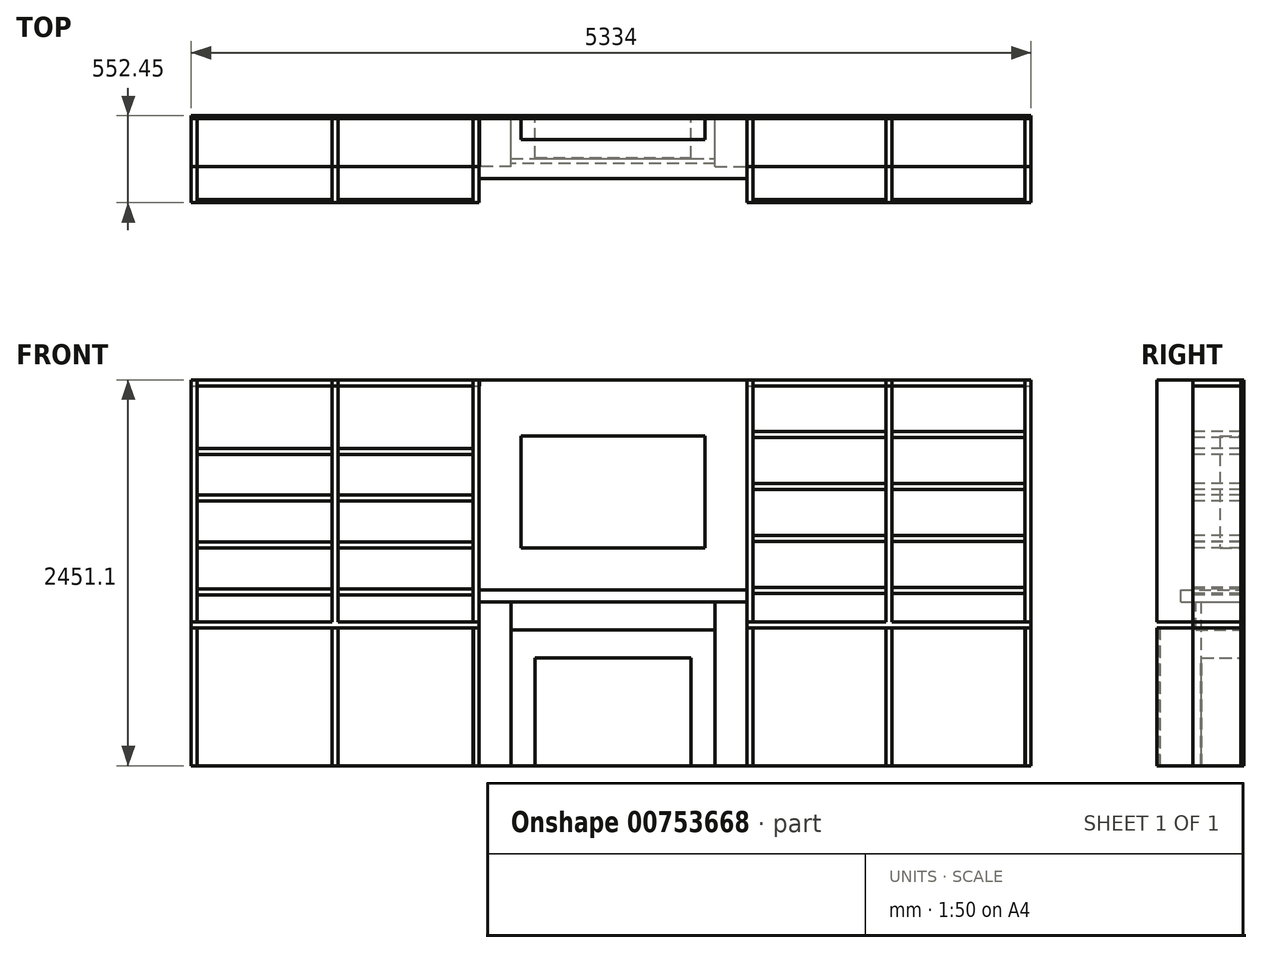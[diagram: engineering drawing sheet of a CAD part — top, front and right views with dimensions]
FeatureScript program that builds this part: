
annotation { "Feature Type Name" : "Feature", "Feature Type Description" : "" }
export const myFeature = defineFeature(function(context is Context, id is Id, definition is map)
    precondition{}
    {
        {
            var Q0;
            Q0=qCreatedBy(makeId("Front.planeOp"),FACE);
            var sketch = newSketch(context, id + "F0", { "sketchPlane" : qUnion([Q0])});
            skLineSegment(sketch, "E0.bottom", {"start": v(0, 0) * mm, "end": v(5334, 0) * mm});
            skLineSegment(sketch, "E0.top", {"start": v(0, 2451.1) * mm, "end": v(5334, 2451.1) * mm});
            skLineSegment(sketch, "E0.left", {"start": v(0, 0) * mm, "end": v(0, 2451.1) * mm});
            skLineSegment(sketch, "E0.right", {"start": v(5334, 0) * mm, "end": v(5334, 2451.1) * mm});
            skSolve(sketch);
        }
        {
            var Q0;
            Q0=makeQuery(id+"F0.imprint","IMPRINT",FACE,{"disambiguationData":[TD([[makeQuery(id+"F0.imprint","IMPRINT",EDGE,{"derivedFrom":sQuery(id+"F0.wireOp",EDGE,"E0.bottom")}),1.0]])]});
            extrude(context, id + "F1", {"entities" : qUnion([Q0]), "oppositeDirection" : true, "depth" : 19.05 * mm, "offsetDistance" : 25.4 * mm});
        }
        {
            var Q0;
            Q0=makeQuery(id+"F1.opExtrude","CAP_FACE",FACE,{"disambiguationData":[OSD([sQuery(id+"F0.wireOp",EDGE,"E0.bottom"),sQuery(id+"F0.wireOp",EDGE,"E0.top"),sQuery(id+"F0.wireOp",EDGE,"E0.left"),sQuery(id+"F0.wireOp",EDGE,"E0.right")])],"isStart":true});
            var sketch = newSketch(context, id + "F2", { "sketchPlane" : qUnion([Q0])});
            skLineSegment(sketch, "E1.bottom", {"start": v(2184.4, 0) * mm, "end": v(3175, 0) * mm});
            skLineSegment(sketch, "E1.top", {"start": v(2184.4, 685.8) * mm, "end": v(3175, 685.8) * mm});
            skLineSegment(sketch, "E1.left", {"start": v(2184.4, 0) * mm, "end": v(2184.4, 685.8) * mm});
            skLineSegment(sketch, "E1.right", {"start": v(3175, 0) * mm, "end": v(3175, 685.8) * mm});
            skSolve(sketch);
        }
        {
            var Q0;
            {var subQ0=sQuery(id+"F5.wireOp",EDGE,"E16.left");Q0=makeQuery(id+"FFi4yrvcJES0MtN_1.boolean.opBoolean","MERGE",FACE,{"derivedFrom":[makeQuery(id+"F11.boolean.opBoolean","MERGE",FACE,{"derivedFrom":[makeQuery(id+"F1.opExtrude","SWEPT_FACE",FACE,{"disambiguationData":[OSD([sQuery(id+"F0.wireOp",EDGE,"E0.left")])]}),makeQuery(id+"F11.opExtrude","SWEPT_FACE",FACE,{"disambiguationData":[OSD([subQ0])]})]}),makeQuery(id+"FFi4yrvcJES0MtN_1.opExtrude","SWEPT_FACE",FACE,{"disambiguationData":[OSD([subQ0])]})]});}
            var sketch = newSketch(context, id + "F3", { "sketchPlane" : qUnion([Q0])});
            skLineSegment(sketch, "E2", {"start": v(0, 2324.1) * mm, "end": v(-6.35, 2317.75) * mm});
            skLineSegment(sketch, "E3", {"start": v(-6.35, 2317.75) * mm, "end": v(0, 2311.4) * mm});
            skLineSegment(sketch, "E4", {"start": v(0, 2311.4) * mm, "end": v(0, 2324.1) * mm});
            skLineSegment(sketch, "E5.1.0.0", {"start": v(0, 2197.1) * mm, "end": v(-6.35, 2190.75) * mm});
            skLineSegment(sketch, "E5.1.0.1", {"start": v(0, 2184.4) * mm, "end": v(0, 2197.1) * mm});
            skLineSegment(sketch, "E5.1.0.2", {"start": v(-6.35, 2190.75) * mm, "end": v(0, 2184.4) * mm});
            skLineSegment(sketch, "E5.2.0.0", {"start": v(0, 2070.1) * mm, "end": v(-6.35, 2063.75) * mm});
            skLineSegment(sketch, "E5.2.0.1", {"start": v(0, 2057.4) * mm, "end": v(0, 2070.1) * mm});
            skLineSegment(sketch, "E5.2.0.2", {"start": v(-6.35, 2063.75) * mm, "end": v(0, 2057.4) * mm});
            skLineSegment(sketch, "E5.3.0.0", {"start": v(0, 1943.1) * mm, "end": v(-6.35, 1936.75) * mm});
            skLineSegment(sketch, "E5.3.0.1", {"start": v(0, 1930.4) * mm, "end": v(0, 1943.1) * mm});
            skLineSegment(sketch, "E5.3.0.2", {"start": v(-6.35, 1936.75) * mm, "end": v(0, 1930.4) * mm});
            skLineSegment(sketch, "E5.4.0.0", {"start": v(0, 1816.1) * mm, "end": v(-6.35, 1809.75) * mm});
            skLineSegment(sketch, "E5.4.0.1", {"start": v(0, 1803.4) * mm, "end": v(0, 1816.1) * mm});
            skLineSegment(sketch, "E5.4.0.2", {"start": v(-6.35, 1809.75) * mm, "end": v(0, 1803.4) * mm});
            skLineSegment(sketch, "E5.5.0.0", {"start": v(0, 1689.1) * mm, "end": v(-6.35, 1682.75) * mm});
            skLineSegment(sketch, "E5.5.0.1", {"start": v(0, 1676.4) * mm, "end": v(0, 1689.1) * mm});
            skLineSegment(sketch, "E5.5.0.2", {"start": v(-6.35, 1682.75) * mm, "end": v(0, 1676.4) * mm});
            skLineSegment(sketch, "E5.6.0.0", {"start": v(0, 1562.1) * mm, "end": v(-6.35, 1555.75) * mm});
            skLineSegment(sketch, "E5.6.0.1", {"start": v(0, 1549.4) * mm, "end": v(0, 1562.1) * mm});
            skLineSegment(sketch, "E5.6.0.2", {"start": v(-6.35, 1555.75) * mm, "end": v(0, 1549.4) * mm});
            skLineSegment(sketch, "E5.7.0.0", {"start": v(0, 1435.1) * mm, "end": v(-6.35, 1428.75) * mm});
            skLineSegment(sketch, "E5.7.0.1", {"start": v(0, 1422.4) * mm, "end": v(0, 1435.1) * mm});
            skLineSegment(sketch, "E5.7.0.2", {"start": v(-6.35, 1428.75) * mm, "end": v(0, 1422.4) * mm});
            skLineSegment(sketch, "E5.8.0.0", {"start": v(0, 1308.1) * mm, "end": v(-6.35, 1301.75) * mm});
            skLineSegment(sketch, "E5.8.0.1", {"start": v(0, 1295.4) * mm, "end": v(0, 1308.1) * mm});
            skLineSegment(sketch, "E5.8.0.2", {"start": v(-6.35, 1301.75) * mm, "end": v(0, 1295.4) * mm});
            skLineSegment(sketch, "E5.9.0.0", {"start": v(0, 1181.1) * mm, "end": v(-6.35, 1174.75) * mm});
            skLineSegment(sketch, "E5.9.0.1", {"start": v(0, 1168.4) * mm, "end": v(0, 1181.1) * mm});
            skLineSegment(sketch, "E5.9.0.2", {"start": v(-6.35, 1174.75) * mm, "end": v(0, 1168.4) * mm});
            skLineSegment(sketch, "E5.10.0.0", {"start": v(0, 1054.1) * mm, "end": v(-6.35, 1047.75) * mm});
            skLineSegment(sketch, "E5.10.0.1", {"start": v(0, 1041.4) * mm, "end": v(0, 1054.1) * mm});
            skLineSegment(sketch, "E5.10.0.2", {"start": v(-6.35, 1047.75) * mm, "end": v(0, 1041.4) * mm});
            skLineSegment(sketch, "E5.11.0.0", {"start": v(0, 927.1) * mm, "end": v(-6.35, 920.75) * mm});
            skLineSegment(sketch, "E5.11.0.1", {"start": v(0, 914.4) * mm, "end": v(0, 927.1) * mm});
            skLineSegment(sketch, "E5.11.0.2", {"start": v(-6.35, 920.75) * mm, "end": v(0, 914.4) * mm});
            skLineSegment(sketch, "E5.12.0.0", {"start": v(0, 800.1) * mm, "end": v(-6.35, 793.75) * mm});
            skLineSegment(sketch, "E5.12.0.1", {"start": v(0, 787.4) * mm, "end": v(0, 800.1) * mm});
            skLineSegment(sketch, "E5.12.0.2", {"start": v(-6.35, 793.75) * mm, "end": v(0, 787.4) * mm});
            skLineSegment(sketch, "E5.13.0.0", {"start": v(0, 673.1) * mm, "end": v(-6.35, 666.75) * mm});
            skLineSegment(sketch, "E5.13.0.1", {"start": v(0, 660.4) * mm, "end": v(0, 673.1) * mm});
            skLineSegment(sketch, "E5.13.0.2", {"start": v(-6.35, 666.75) * mm, "end": v(0, 660.4) * mm});
            skLineSegment(sketch, "E5.14.0.0", {"start": v(0, 546.1) * mm, "end": v(-6.35, 539.75) * mm});
            skLineSegment(sketch, "E5.14.0.1", {"start": v(0, 533.4) * mm, "end": v(0, 546.1) * mm});
            skLineSegment(sketch, "E5.14.0.2", {"start": v(-6.35, 539.75) * mm, "end": v(0, 533.4) * mm});
            skLineSegment(sketch, "E5.15.0.0", {"start": v(0, 419.1) * mm, "end": v(-6.35, 412.75) * mm});
            skLineSegment(sketch, "E5.15.0.1", {"start": v(0, 406.4) * mm, "end": v(0, 419.1) * mm});
            skLineSegment(sketch, "E5.15.0.2", {"start": v(-6.35, 412.75) * mm, "end": v(0, 406.4) * mm});
            skLineSegment(sketch, "E5.16.0.0", {"start": v(0, 292.1) * mm, "end": v(-6.35, 285.75) * mm});
            skLineSegment(sketch, "E5.16.0.1", {"start": v(0, 279.4) * mm, "end": v(0, 292.1) * mm});
            skLineSegment(sketch, "E5.16.0.2", {"start": v(-6.35, 285.75) * mm, "end": v(0, 279.4) * mm});
            skLineSegment(sketch, "E5.17.0.0", {"start": v(0, 165.1) * mm, "end": v(-6.35, 158.75) * mm});
            skLineSegment(sketch, "E5.17.0.1", {"start": v(0, 152.4) * mm, "end": v(0, 165.1) * mm});
            skLineSegment(sketch, "E5.17.0.2", {"start": v(-6.35, 158.75) * mm, "end": v(0, 152.4) * mm});
            skLineSegment(sketch, "E5.direction1", {"start": v(-6.35, 2317.75) * mm, "end": v(-6.35, 2190.75) * mm, "construction": true});
            skSolve(sketch);
        }
        {
            var Q0;
            Q0=makeQuery(id+"F2.imprint","IMPRINT",FACE,{"disambiguationData":[TD([[makeQuery(id+"F2.imprint","IMPRINT",EDGE,{"derivedFrom":sQuery(id+"F2.wireOp",EDGE,"E1.bottom")}),1.0]])]});
            extrude(context, id + "F4", {"entities" : qUnion([Q0]), "depth" : 247.65 * mm, "offsetDistance" : 25.4 * mm});
        }
        {
            var Q0;
            Q0=makeQuery(id+"F1.opExtrude","CAP_FACE",FACE,{"disambiguationData":[OSD([sQuery(id+"F0.wireOp",EDGE,"E0.bottom"),sQuery(id+"F0.wireOp",EDGE,"E0.top"),sQuery(id+"F0.wireOp",EDGE,"E0.left"),sQuery(id+"F0.wireOp",EDGE,"E0.right")])],"isStart":true});
            var sketch = newSketch(context, id + "F5", { "sketchPlane" : qUnion([Q0])});
            skLineSegment(sketch, "E6.bottom", {"start": v(2184.4, 0) * mm, "end": v(2032, 0) * mm});
            skLineSegment(sketch, "E6.top", {"start": v(2184.4, 863.6) * mm, "end": v(2032, 863.6) * mm});
            skLineSegment(sketch, "E6.left", {"start": v(2184.4, 0) * mm, "end": v(2184.4, 685.8) * mm});
            skLineSegment(sketch, "E6.right", {"start": v(2032, 0) * mm, "end": v(2032, 863.6) * mm});
            skLineSegment(sketch, "E7.bottom", {"start": v(2184.4, 863.6) * mm, "end": v(3327.4, 863.6) * mm});
            skLineSegment(sketch, "E7.top", {"start": v(2184.4, 685.8) * mm, "end": v(3175, 685.8) * mm});
            skLineSegment(sketch, "E7.right", {"start": v(3327.4, 863.6) * mm, "end": v(3327.4, 685.8) * mm});
            skLineSegment(sketch, "E8.top", {"start": v(3175, 0) * mm, "end": v(3327.4, 0) * mm});
            skLineSegment(sketch, "E8.left", {"start": v(3175, 685.8) * mm, "end": v(3175, 0) * mm});
            skLineSegment(sketch, "E8.right", {"start": v(3327.4, 685.8) * mm, "end": v(3327.4, 0) * mm});
            skLineSegment(sketch, "E9.bottom", {"start": v(2032, 0) * mm, "end": v(1828.8, 0) * mm});
            skLineSegment(sketch, "E9.top", {"start": v(2032, 1041.4) * mm, "end": v(1828.8, 1041.4) * mm});
            skLineSegment(sketch, "E9.left", {"start": v(2032, 0) * mm, "end": v(2032, 1041.4) * mm});
            skLineSegment(sketch, "E9.right", {"start": v(1828.8, 0) * mm, "end": v(1828.8, 1041.4) * mm});
            skLineSegment(sketch, "E10.bottom", {"start": v(3327.4, 0) * mm, "end": v(3530.6, 0) * mm});
            skLineSegment(sketch, "E10.top", {"start": v(3327.4, 1041.4) * mm, "end": v(3530.6, 1041.4) * mm});
            skLineSegment(sketch, "E10.left", {"start": v(3327.4, 0) * mm, "end": v(3327.4, 1041.4) * mm});
            skLineSegment(sketch, "E10.right", {"start": v(3530.6, 0) * mm, "end": v(3530.6, 1041.4) * mm});
            skLineSegment(sketch, "E11", {"start": v(2032, 1041.4) * mm, "end": v(3327.4, 1041.4) * mm});
            skLineSegment(sketch, "E12.bottom", {"start": v(1828.8, 1041.4) * mm, "end": v(3530.6, 1041.4) * mm});
            skLineSegment(sketch, "E12.top", {"start": v(1828.8, 1117.6) * mm, "end": v(3530.6, 1117.6) * mm});
            skLineSegment(sketch, "E12.left", {"start": v(1828.8, 1041.4) * mm, "end": v(1828.8, 1117.6) * mm});
            skLineSegment(sketch, "E12.right", {"start": v(3530.6, 1041.4) * mm, "end": v(3530.6, 1117.6) * mm});
            skLineSegment(sketch, "E13.bottom", {"start": v(1828.8, 0) * mm, "end": v(1790.7, 0) * mm});
            skLineSegment(sketch, "E13.top", {"start": v(1828.8, 2451.1) * mm, "end": v(1790.7, 2451.1) * mm});
            skLineSegment(sketch, "E13.left", {"start": v(1828.8, 0) * mm, "end": v(1828.8, 2451.1) * mm});
            skLineSegment(sketch, "E13.right", {"start": v(1790.7, 0) * mm, "end": v(1790.7, 876.3) * mm});
            skLineSegment(sketch, "E14.bottom", {"start": v(3530.6, 0) * mm, "end": v(3568.7, 0) * mm});
            skLineSegment(sketch, "E14.top", {"start": v(3530.6, 2451.1) * mm, "end": v(3568.7, 2451.1) * mm});
            skLineSegment(sketch, "E14.left", {"start": v(3530.6, 0) * mm, "end": v(3530.6, 2451.1) * mm});
            skLineSegment(sketch, "E14.right", {"start": v(3568.7, 0) * mm, "end": v(3568.7, 876.3) * mm});
            skLineSegment(sketch, "E15.bottom", {"start": v(5334, 0) * mm, "end": v(5295.9, 0) * mm});
            skLineSegment(sketch, "E15.top", {"start": v(5334, 2451.1) * mm, "end": v(5295.9, 2451.1) * mm});
            skLineSegment(sketch, "E15.left", {"start": v(5334, 0) * mm, "end": v(5334, 2451.1) * mm});
            skLineSegment(sketch, "E15.right", {"start": v(5295.9, 0) * mm, "end": v(5295.9, 876.3) * mm});
            skLineSegment(sketch, "E16.bottom", {"start": v(0, 0) * mm, "end": v(38.1, 0) * mm});
            skLineSegment(sketch, "E16.top", {"start": v(0, 2451.1) * mm, "end": v(38.1, 2451.1) * mm});
            skLineSegment(sketch, "E16.left", {"start": v(0, 0) * mm, "end": v(0, 2451.1) * mm});
            skLineSegment(sketch, "E16.right", {"start": v(38.1, 0) * mm, "end": v(38.1, 876.3) * mm});
            skLineSegment(sketch, "E17.bottom", {"start": v(3530.6, 914.4) * mm, "end": v(5334, 914.4) * mm});
            skLineSegment(sketch, "E17.top", {"start": v(3530.6, 876.3) * mm, "end": v(5334, 876.3) * mm});
            skLineSegment(sketch, "E18.bottom", {"start": v(0, 914.4) * mm, "end": v(1828.8, 914.4) * mm});
            skLineSegment(sketch, "E18.top", {"start": v(0, 876.3) * mm, "end": v(1828.8, 876.3) * mm});
            skLineSegment(sketch, "E19", {"start": v(895.35, 2451.1) * mm, "end": v(895.35, 914.4) * mm});
            skLineSegment(sketch, "E20", {"start": v(933.45, 2451.1) * mm, "end": v(933.45, 914.4) * mm});
            skLineSegment(sketch, "E21", {"start": v(4451.35, 2451.1) * mm, "end": v(4451.35, 914.4) * mm});
            skLineSegment(sketch, "E22", {"start": v(4413.25, 2451.1) * mm, "end": v(4413.25, 914.4) * mm});
            skPoint(sketch, "E22.endSnap0", {"position": v(4432.3, 914.4) * mm});
            skLineSegment(sketch, "E23.bottom", {"start": v(2095.5, 2095.5) * mm, "end": v(3263.9, 2095.5) * mm});
            skLineSegment(sketch, "E23.top", {"start": v(2095.5, 1384.3) * mm, "end": v(3263.9, 1384.3) * mm});
            skLineSegment(sketch, "E23.left", {"start": v(2095.5, 2095.5) * mm, "end": v(2095.5, 1384.3) * mm});
            skLineSegment(sketch, "E23.right", {"start": v(3263.9, 2095.5) * mm, "end": v(3263.9, 1384.3) * mm});
            skLineSegment(sketch, "E24.trimOffspring", {"start": v(1790.7, 914.4) * mm, "end": v(1790.7, 2451.1) * mm});
            skLineSegment(sketch, "E25.trimOffspring", {"start": v(3568.7, 914.4) * mm, "end": v(3568.7, 2451.1) * mm});
            skLineSegment(sketch, "E26.trimOffspring", {"start": v(38.1, 914.4) * mm, "end": v(38.1, 2451.1) * mm});
            skPoint(sketch, "E17.right.start.orphan", {"position": v(5295.9, 914.4) * mm});
            skLineSegment(sketch, "E27.trimOffspring", {"start": v(5295.9, 914.4) * mm, "end": v(5295.9, 2451.1) * mm});
            skLineSegment(sketch, "E28.bottom", {"start": v(895.35, 876.3) * mm, "end": v(933.45, 876.3) * mm});
            skLineSegment(sketch, "E28.top", {"start": v(895.35, 0) * mm, "end": v(933.45, 0) * mm});
            skLineSegment(sketch, "E28.left", {"start": v(895.35, 876.3) * mm, "end": v(895.35, 0) * mm});
            skLineSegment(sketch, "E28.right", {"start": v(933.45, 876.3) * mm, "end": v(933.45, 0) * mm});
            skLineSegment(sketch, "E29.bottom", {"start": v(4413.25, 876.3) * mm, "end": v(4451.35, 876.3) * mm});
            skLineSegment(sketch, "E29.top", {"start": v(4413.25, 0) * mm, "end": v(4451.35, 0) * mm});
            skLineSegment(sketch, "E29.left", {"start": v(4413.25, 876.3) * mm, "end": v(4413.25, 0) * mm});
            skLineSegment(sketch, "E29.right", {"start": v(4451.35, 876.3) * mm, "end": v(4451.35, 0) * mm});
            skSolve(sketch);
        }
        {
            var Q0;
            {var subQ4=sQuery(id+"F5.wireOp",EDGE,"E6.bottom");Q0=makeQuery(id+"F5.imprint","IMPRINT",FACE,{"disambiguationData":[TD([[makeQuery(id+"F5.imprint","IMPRINT",EDGE,{"derivedFrom":subQ4}),1.0]])]});}
            var Q1;
            {var subQ0=sQuery(id+"F5.wireOp",EDGE,"E6.left");var subQ1=sQuery(id+"F0.wireOp",EDGE,"E0.left");var subQ2=makeQuery(id+"FlHhq8AFgQTEit1_1.boolean.opBoolean","COPY",EDGE,{"derivedFrom":makeQuery(id+"FlHhq8AFgQTEit1_1.opExtrude","SWEPT_EDGE",EDGE,{"disambiguationData":[OSD([subQ1,sQuery(id+"F3.wireOp",EDGE,"E5.17.0.0"),sQuery(id+"F3.wireOp",EDGE,"E5.17.0.1")])]})});var subQ3=makeQuery(id+"F5.imprint","INTERSECT",VERTEX,{"derivedFrom":[subQ2,subQ0]});Q1=makeQuery(id+"F5.imprint","IMPRINT",FACE,{"disambiguationData":[TD([[makeQuery(id+"F5.imprint","IMPRINT",EDGE,{"disambiguationData":[TD([[subQ3,-1.0]])],"derivedFrom":subQ0}),1.0]])]});}
            var Q2;
            {var subQ0=sQuery(id+"F5.wireOp",EDGE,"E6.left");var subQ1=sQuery(id+"F3.wireOp",EDGE,"E5.17.0.1");var subQ2=sQuery(id+"F0.wireOp",EDGE,"E0.left");var subQ3=makeQuery(id+"FlHhq8AFgQTEit1_1.boolean.opBoolean","COPY",EDGE,{"derivedFrom":makeQuery(id+"FlHhq8AFgQTEit1_1.opExtrude","SWEPT_EDGE",EDGE,{"disambiguationData":[OSD([subQ2,subQ1,sQuery(id+"F3.wireOp",EDGE,"E5.17.0.2")])]})});var subQ4=makeQuery(id+"F5.imprint","INTERSECT",VERTEX,{"derivedFrom":[subQ3,subQ0]});Q2=makeQuery(id+"F5.imprint","IMPRINT",FACE,{"disambiguationData":[TD([[makeQuery(id+"F5.imprint","IMPRINT",EDGE,{"disambiguationData":[TD([[subQ4,-1.0]])],"derivedFrom":subQ0}),1.0]])]});}
            var Q3;
            {var subQ0=sQuery(id+"F5.wireOp",EDGE,"E6.left");var subQ1=sQuery(id+"F3.wireOp",EDGE,"E5.16.0.1");var subQ2=sQuery(id+"F0.wireOp",EDGE,"E0.left");var subQ3=makeQuery(id+"FlHhq8AFgQTEit1_1.boolean.opBoolean","COPY",EDGE,{"derivedFrom":makeQuery(id+"FlHhq8AFgQTEit1_1.opExtrude","SWEPT_EDGE",EDGE,{"disambiguationData":[OSD([subQ2,subQ1,sQuery(id+"F3.wireOp",EDGE,"E5.16.0.2")])]})});var subQ4=makeQuery(id+"F5.imprint","INTERSECT",VERTEX,{"derivedFrom":[subQ3,subQ0]});Q3=makeQuery(id+"F5.imprint","IMPRINT",FACE,{"disambiguationData":[TD([[makeQuery(id+"F5.imprint","IMPRINT",EDGE,{"disambiguationData":[TD([[subQ4,-1.0]])],"derivedFrom":subQ0}),1.0]])]});}
            var Q4;
            {var subQ0=sQuery(id+"F5.wireOp",EDGE,"E6.left");var subQ1=sQuery(id+"F0.wireOp",EDGE,"E0.left");var subQ2=makeQuery(id+"FlHhq8AFgQTEit1_1.boolean.opBoolean","COPY",EDGE,{"derivedFrom":makeQuery(id+"FlHhq8AFgQTEit1_1.opExtrude","SWEPT_EDGE",EDGE,{"disambiguationData":[OSD([subQ1,sQuery(id+"F3.wireOp",EDGE,"E5.16.0.0"),sQuery(id+"F3.wireOp",EDGE,"E5.16.0.1")])]})});var subQ3=makeQuery(id+"F5.imprint","INTERSECT",VERTEX,{"derivedFrom":[subQ2,subQ0]});Q4=makeQuery(id+"F5.imprint","IMPRINT",FACE,{"disambiguationData":[TD([[makeQuery(id+"F5.imprint","IMPRINT",EDGE,{"disambiguationData":[TD([[subQ3,-1.0]])],"derivedFrom":subQ0}),1.0]])]});}
            var Q5;
            {var subQ0=sQuery(id+"F5.wireOp",EDGE,"E6.left");var subQ1=sQuery(id+"F3.wireOp",EDGE,"E5.15.0.1");var subQ2=sQuery(id+"F0.wireOp",EDGE,"E0.left");var subQ3=makeQuery(id+"FlHhq8AFgQTEit1_1.boolean.opBoolean","COPY",EDGE,{"derivedFrom":makeQuery(id+"FlHhq8AFgQTEit1_1.opExtrude","SWEPT_EDGE",EDGE,{"disambiguationData":[OSD([subQ2,subQ1,sQuery(id+"F3.wireOp",EDGE,"E5.15.0.2")])]})});var subQ4=makeQuery(id+"F5.imprint","INTERSECT",VERTEX,{"derivedFrom":[subQ3,subQ0]});Q5=makeQuery(id+"F5.imprint","IMPRINT",FACE,{"disambiguationData":[TD([[makeQuery(id+"F5.imprint","IMPRINT",EDGE,{"disambiguationData":[TD([[subQ4,-1.0]])],"derivedFrom":subQ0}),1.0]])]});}
            var Q6;
            {var subQ0=sQuery(id+"F5.wireOp",EDGE,"E6.left");var subQ1=sQuery(id+"F0.wireOp",EDGE,"E0.left");var subQ2=makeQuery(id+"FlHhq8AFgQTEit1_1.boolean.opBoolean","COPY",EDGE,{"derivedFrom":makeQuery(id+"FlHhq8AFgQTEit1_1.opExtrude","SWEPT_EDGE",EDGE,{"disambiguationData":[OSD([subQ1,sQuery(id+"F3.wireOp",EDGE,"E5.15.0.0"),sQuery(id+"F3.wireOp",EDGE,"E5.15.0.1")])]})});var subQ3=makeQuery(id+"F5.imprint","INTERSECT",VERTEX,{"derivedFrom":[subQ2,subQ0]});Q6=makeQuery(id+"F5.imprint","IMPRINT",FACE,{"disambiguationData":[TD([[makeQuery(id+"F5.imprint","IMPRINT",EDGE,{"disambiguationData":[TD([[subQ3,-1.0]])],"derivedFrom":subQ0}),1.0]])]});}
            var Q7;
            {var subQ0=sQuery(id+"F5.wireOp",EDGE,"E6.left");var subQ1=sQuery(id+"F3.wireOp",EDGE,"E5.14.0.1");var subQ2=sQuery(id+"F0.wireOp",EDGE,"E0.left");var subQ3=makeQuery(id+"FlHhq8AFgQTEit1_1.boolean.opBoolean","COPY",EDGE,{"derivedFrom":makeQuery(id+"FlHhq8AFgQTEit1_1.opExtrude","SWEPT_EDGE",EDGE,{"disambiguationData":[OSD([subQ2,subQ1,sQuery(id+"F3.wireOp",EDGE,"E5.14.0.2")])]})});var subQ4=makeQuery(id+"F5.imprint","INTERSECT",VERTEX,{"derivedFrom":[subQ3,subQ0]});Q7=makeQuery(id+"F5.imprint","IMPRINT",FACE,{"disambiguationData":[TD([[makeQuery(id+"F5.imprint","IMPRINT",EDGE,{"disambiguationData":[TD([[subQ4,-1.0]])],"derivedFrom":subQ0}),1.0]])]});}
            var Q8;
            {var subQ0=sQuery(id+"F5.wireOp",EDGE,"E6.left");var subQ1=sQuery(id+"F0.wireOp",EDGE,"E0.left");var subQ2=makeQuery(id+"FlHhq8AFgQTEit1_1.boolean.opBoolean","COPY",EDGE,{"derivedFrom":makeQuery(id+"FlHhq8AFgQTEit1_1.opExtrude","SWEPT_EDGE",EDGE,{"disambiguationData":[OSD([subQ1,sQuery(id+"F3.wireOp",EDGE,"E5.14.0.0"),sQuery(id+"F3.wireOp",EDGE,"E5.14.0.1")])]})});var subQ3=makeQuery(id+"F5.imprint","INTERSECT",VERTEX,{"derivedFrom":[subQ2,subQ0]});Q8=makeQuery(id+"F5.imprint","IMPRINT",FACE,{"disambiguationData":[TD([[makeQuery(id+"F5.imprint","IMPRINT",EDGE,{"disambiguationData":[TD([[subQ3,-1.0]])],"derivedFrom":subQ0}),1.0]])]});}
            var Q9;
            {var subQ7=sQuery(id+"F5.wireOp",EDGE,"E7.top");Q9=makeQuery(id+"F5.imprint","IMPRINT",FACE,{"disambiguationData":[TD([[makeQuery(id+"F5.imprint","IMPRINT",EDGE,{"derivedFrom":subQ7}),1.0]])]});}
            var Q10;
            {var subQ5=sQuery(id+"F5.wireOp",EDGE,"E6.top");Q10=makeQuery(id+"F5.imprint","IMPRINT",FACE,{"disambiguationData":[TD([[makeQuery(id+"F5.imprint","IMPRINT",EDGE,{"derivedFrom":subQ5}),1.0]])]});}
            var Q11;
            {var subQ0=sQuery(id+"F5.wireOp",EDGE,"E8.left");var subQ1=sQuery(id+"F0.wireOp",EDGE,"E0.left");var subQ2=makeQuery(id+"FlHhq8AFgQTEit1_1.boolean.opBoolean","COPY",EDGE,{"derivedFrom":makeQuery(id+"FlHhq8AFgQTEit1_1.opExtrude","SWEPT_EDGE",EDGE,{"disambiguationData":[OSD([subQ1,sQuery(id+"F3.wireOp",EDGE,"E5.13.0.1"),sQuery(id+"F3.wireOp",EDGE,"E5.13.0.2")])]})});var subQ3=makeQuery(id+"F5.imprint","INTERSECT",VERTEX,{"derivedFrom":[subQ2,subQ0]});Q11=makeQuery(id+"F5.imprint","IMPRINT",FACE,{"disambiguationData":[TD([[makeQuery(id+"F5.imprint","IMPRINT",EDGE,{"disambiguationData":[TD([[subQ3,-1.0]])],"derivedFrom":subQ0}),1.0]])]});}
            var Q12;
            {var subQ0=sQuery(id+"F5.wireOp",EDGE,"E8.left");var subQ1=sQuery(id+"F0.wireOp",EDGE,"E0.left");var subQ2=makeQuery(id+"FlHhq8AFgQTEit1_1.boolean.opBoolean","COPY",EDGE,{"derivedFrom":makeQuery(id+"FlHhq8AFgQTEit1_1.opExtrude","SWEPT_EDGE",EDGE,{"disambiguationData":[OSD([subQ1,sQuery(id+"F3.wireOp",EDGE,"E5.14.0.1"),sQuery(id+"F3.wireOp",EDGE,"E5.14.0.2")])]})});var subQ3=makeQuery(id+"F5.imprint","INTERSECT",VERTEX,{"derivedFrom":[subQ2,subQ0]});Q12=makeQuery(id+"F5.imprint","IMPRINT",FACE,{"disambiguationData":[TD([[makeQuery(id+"F5.imprint","IMPRINT",EDGE,{"disambiguationData":[TD([[subQ3,-1.0]])],"derivedFrom":subQ0}),1.0]])]});}
            var Q13;
            {var subQ0=sQuery(id+"F5.wireOp",EDGE,"E8.left");var subQ1=sQuery(id+"F0.wireOp",EDGE,"E0.left");var subQ2=makeQuery(id+"FlHhq8AFgQTEit1_1.boolean.opBoolean","COPY",EDGE,{"derivedFrom":makeQuery(id+"FlHhq8AFgQTEit1_1.opExtrude","SWEPT_EDGE",EDGE,{"disambiguationData":[OSD([subQ1,sQuery(id+"F3.wireOp",EDGE,"E5.15.0.1"),sQuery(id+"F3.wireOp",EDGE,"E5.15.0.2")])]})});var subQ3=makeQuery(id+"F5.imprint","INTERSECT",VERTEX,{"derivedFrom":[subQ2,subQ0]});Q13=makeQuery(id+"F5.imprint","IMPRINT",FACE,{"disambiguationData":[TD([[makeQuery(id+"F5.imprint","IMPRINT",EDGE,{"disambiguationData":[TD([[subQ3,-1.0]])],"derivedFrom":subQ0}),1.0]])]});}
            var Q14;
            {var subQ0=sQuery(id+"F5.wireOp",EDGE,"E8.left");var subQ1=sQuery(id+"F0.wireOp",EDGE,"E0.left");var subQ2=makeQuery(id+"FlHhq8AFgQTEit1_1.boolean.opBoolean","COPY",EDGE,{"derivedFrom":makeQuery(id+"FlHhq8AFgQTEit1_1.opExtrude","SWEPT_EDGE",EDGE,{"disambiguationData":[OSD([subQ1,sQuery(id+"F3.wireOp",EDGE,"E5.16.0.1"),sQuery(id+"F3.wireOp",EDGE,"E5.16.0.2")])]})});var subQ3=makeQuery(id+"F5.imprint","INTERSECT",VERTEX,{"derivedFrom":[subQ2,subQ0]});Q14=makeQuery(id+"F5.imprint","IMPRINT",FACE,{"disambiguationData":[TD([[makeQuery(id+"F5.imprint","IMPRINT",EDGE,{"disambiguationData":[TD([[subQ3,-1.0]])],"derivedFrom":subQ0}),1.0]])]});}
            var Q15;
            {var subQ0=sQuery(id+"F5.wireOp",EDGE,"E8.top");Q15=makeQuery(id+"F5.imprint","IMPRINT",FACE,{"disambiguationData":[TD([[makeQuery(id+"F5.imprint","IMPRINT",EDGE,{"derivedFrom":subQ0}),1.0]])]});}
            var Q16;
            {var subQ0=sQuery(id+"F5.wireOp",EDGE,"E8.left");var subQ1=sQuery(id+"F3.wireOp",EDGE,"E5.17.0.1");var subQ2=sQuery(id+"F0.wireOp",EDGE,"E0.left");var subQ3=makeQuery(id+"FlHhq8AFgQTEit1_1.boolean.opBoolean","COPY",EDGE,{"derivedFrom":makeQuery(id+"FlHhq8AFgQTEit1_1.opExtrude","SWEPT_EDGE",EDGE,{"disambiguationData":[OSD([subQ2,sQuery(id+"F3.wireOp",EDGE,"E5.17.0.0"),subQ1])]})});var subQ4=makeQuery(id+"F5.imprint","INTERSECT",VERTEX,{"derivedFrom":[subQ3,subQ0]});Q16=makeQuery(id+"F5.imprint","IMPRINT",FACE,{"disambiguationData":[TD([[makeQuery(id+"F5.imprint","IMPRINT",EDGE,{"disambiguationData":[TD([[subQ4,-1.0]])],"derivedFrom":subQ0}),1.0]])]});}
            var Q17;
            {var subQ0=sQuery(id+"F5.wireOp",EDGE,"E8.left");var subQ1=sQuery(id+"F3.wireOp",EDGE,"E5.16.0.1");var subQ2=sQuery(id+"F0.wireOp",EDGE,"E0.left");var subQ3=makeQuery(id+"FlHhq8AFgQTEit1_1.boolean.opBoolean","COPY",EDGE,{"derivedFrom":makeQuery(id+"FlHhq8AFgQTEit1_1.opExtrude","SWEPT_EDGE",EDGE,{"disambiguationData":[OSD([subQ2,sQuery(id+"F3.wireOp",EDGE,"E5.16.0.0"),subQ1])]})});var subQ4=makeQuery(id+"F5.imprint","INTERSECT",VERTEX,{"derivedFrom":[subQ3,subQ0]});Q17=makeQuery(id+"F5.imprint","IMPRINT",FACE,{"disambiguationData":[TD([[makeQuery(id+"F5.imprint","IMPRINT",EDGE,{"disambiguationData":[TD([[subQ4,-1.0]])],"derivedFrom":subQ0}),1.0]])]});}
            var Q18;
            {var subQ0=sQuery(id+"F5.wireOp",EDGE,"E8.left");var subQ1=sQuery(id+"F3.wireOp",EDGE,"E5.15.0.1");var subQ2=sQuery(id+"F0.wireOp",EDGE,"E0.left");var subQ3=makeQuery(id+"FlHhq8AFgQTEit1_1.boolean.opBoolean","COPY",EDGE,{"derivedFrom":makeQuery(id+"FlHhq8AFgQTEit1_1.opExtrude","SWEPT_EDGE",EDGE,{"disambiguationData":[OSD([subQ2,sQuery(id+"F3.wireOp",EDGE,"E5.15.0.0"),subQ1])]})});var subQ4=makeQuery(id+"F5.imprint","INTERSECT",VERTEX,{"derivedFrom":[subQ3,subQ0]});Q18=makeQuery(id+"F5.imprint","IMPRINT",FACE,{"disambiguationData":[TD([[makeQuery(id+"F5.imprint","IMPRINT",EDGE,{"disambiguationData":[TD([[subQ4,-1.0]])],"derivedFrom":subQ0}),1.0]])]});}
            var Q19;
            {var subQ0=sQuery(id+"F5.wireOp",EDGE,"E8.left");var subQ1=sQuery(id+"F3.wireOp",EDGE,"E5.13.0.1");var subQ2=sQuery(id+"F0.wireOp",EDGE,"E0.left");var subQ3=makeQuery(id+"FlHhq8AFgQTEit1_1.boolean.opBoolean","COPY",EDGE,{"derivedFrom":makeQuery(id+"FlHhq8AFgQTEit1_1.opExtrude","SWEPT_EDGE",EDGE,{"disambiguationData":[OSD([subQ2,sQuery(id+"F3.wireOp",EDGE,"E5.13.0.0"),subQ1])]})});var subQ4=makeQuery(id+"F5.imprint","INTERSECT",VERTEX,{"derivedFrom":[subQ3,subQ0]});Q19=makeQuery(id+"F5.imprint","IMPRINT",FACE,{"disambiguationData":[TD([[makeQuery(id+"F5.imprint","IMPRINT",EDGE,{"disambiguationData":[TD([[subQ4,-1.0]])],"derivedFrom":subQ0}),1.0]])]});}
            var Q20;
            {var subQ0=sQuery(id+"F5.wireOp",EDGE,"E8.left");var subQ1=sQuery(id+"F3.wireOp",EDGE,"E5.14.0.1");var subQ2=sQuery(id+"F0.wireOp",EDGE,"E0.left");var subQ3=makeQuery(id+"FlHhq8AFgQTEit1_1.boolean.opBoolean","COPY",EDGE,{"derivedFrom":makeQuery(id+"FlHhq8AFgQTEit1_1.opExtrude","SWEPT_EDGE",EDGE,{"disambiguationData":[OSD([subQ2,sQuery(id+"F3.wireOp",EDGE,"E5.14.0.0"),subQ1])]})});var subQ4=makeQuery(id+"F5.imprint","INTERSECT",VERTEX,{"derivedFrom":[subQ3,subQ0]});Q20=makeQuery(id+"F5.imprint","IMPRINT",FACE,{"disambiguationData":[TD([[makeQuery(id+"F5.imprint","IMPRINT",EDGE,{"disambiguationData":[TD([[subQ4,-1.0]])],"derivedFrom":subQ0}),1.0]])]});}
            var Q21;
            {var subQ0=sQuery(id+"F5.wireOp",EDGE,"E6.left");var subQ1=sQuery(id+"F3.wireOp",EDGE,"E5.13.0.1");var subQ2=sQuery(id+"F0.wireOp",EDGE,"E0.left");var subQ3=makeQuery(id+"FlHhq8AFgQTEit1_1.boolean.opBoolean","COPY",EDGE,{"derivedFrom":makeQuery(id+"FlHhq8AFgQTEit1_1.opExtrude","SWEPT_EDGE",EDGE,{"disambiguationData":[OSD([subQ2,subQ1,sQuery(id+"F3.wireOp",EDGE,"E5.13.0.2")])]})});var subQ4=makeQuery(id+"F5.imprint","INTERSECT",VERTEX,{"derivedFrom":[subQ3,subQ0]});Q21=makeQuery(id+"F5.imprint","IMPRINT",FACE,{"disambiguationData":[TD([[makeQuery(id+"F5.imprint","IMPRINT",EDGE,{"disambiguationData":[TD([[subQ4,-1.0]])],"derivedFrom":subQ0}),1.0]])]});}
            var Q22;
            {var subQ0=sQuery(id+"F5.wireOp",EDGE,"E9.left");var subQ1=sQuery(id+"F3.wireOp",EDGE,"E5.12.0.1");var subQ2=sQuery(id+"F0.wireOp",EDGE,"E0.left");var subQ3=makeQuery(id+"FlHhq8AFgQTEit1_1.boolean.opBoolean","COPY",EDGE,{"derivedFrom":makeQuery(id+"FlHhq8AFgQTEit1_1.opExtrude","SWEPT_EDGE",EDGE,{"disambiguationData":[OSD([subQ2,subQ1,sQuery(id+"F3.wireOp",EDGE,"E5.12.0.2")])]})});var subQ4=makeQuery(id+"F5.imprint","INTERSECT",VERTEX,{"derivedFrom":[subQ3,subQ0]});Q22=makeQuery(id+"F5.imprint","IMPRINT",FACE,{"disambiguationData":[TD([[makeQuery(id+"F5.imprint","IMPRINT",EDGE,{"disambiguationData":[TD([[subQ4,-1.0]])],"derivedFrom":subQ0}),-1.0]])]});}
            extrude(context, id + "F6", {"entities" : qUnion([Q0, Q1, Q2, Q3, Q4, Q5, Q6, Q7, Q8, Q9, Q10, Q11, Q12, Q13, Q14, Q15, Q16, Q17, Q18, Q19, Q20, Q21, Q22]), "depth" : 254 * mm, "offsetDistance" : 25.4 * mm});
        }
        {
            var Q0;
            {var subQ1=sQuery(id+"F5.wireOp",EDGE,"E6.top");Q0=makeQuery(id+"F5.imprint","IMPRINT",FACE,{"disambiguationData":[TD([[makeQuery(id+"F5.imprint","IMPRINT",EDGE,{"derivedFrom":subQ1}),-1.0]])]});}
            var Q1;
            {var subQ0=sQuery(id+"F5.wireOp",EDGE,"E12.bottom");var subQ1=sQuery(id+"F5.wireOp",EDGE,"E9.left");var subQ2=makeQuery(id+"F5.imprint","INTERSECT",VERTEX,{"derivedFrom":[subQ1,subQ0]});Q1=makeQuery(id+"F5.imprint","IMPRINT",FACE,{"disambiguationData":[TD([[makeQuery(id+"F5.imprint","IMPRINT",EDGE,{"disambiguationData":[TD([[subQ2,1.0]])],"derivedFrom":subQ0}),1.0]])]});}
            var Q2;
            {var subQ0=sQuery(id+"F5.wireOp",EDGE,"E9.left");var subQ1=sQuery(id+"F3.wireOp",EDGE,"E5.11.0.1");var subQ2=sQuery(id+"F0.wireOp",EDGE,"E0.left");var subQ3=makeQuery(id+"FlHhq8AFgQTEit1_1.boolean.opBoolean","COPY",EDGE,{"derivedFrom":makeQuery(id+"FlHhq8AFgQTEit1_1.opExtrude","SWEPT_EDGE",EDGE,{"disambiguationData":[OSD([subQ2,subQ1,sQuery(id+"F3.wireOp",EDGE,"E5.11.0.2")])]})});var subQ4=makeQuery(id+"F5.imprint","INTERSECT",VERTEX,{"derivedFrom":[subQ3,subQ0]});Q2=makeQuery(id+"F5.imprint","IMPRINT",FACE,{"disambiguationData":[TD([[makeQuery(id+"F5.imprint","IMPRINT",EDGE,{"disambiguationData":[TD([[subQ4,-1.0]])],"derivedFrom":subQ0}),-1.0]])]});}
            extrude(context, id + "F7", {"entities" : qUnion([Q0, Q1, Q2]), "depth" : 285.75 * mm, "offsetDistance" : 25.4 * mm});
        }
        {
            var Q0;
            {var subQ0=sQuery(id+"F5.wireOp",EDGE,"E9.bottom");Q0=makeQuery(id+"F5.imprint","IMPRINT",FACE,{"disambiguationData":[TD([[makeQuery(id+"F5.imprint","IMPRINT",EDGE,{"derivedFrom":subQ0}),1.0]])]});}
            var Q1;
            {var subQ0=sQuery(id+"F5.wireOp",EDGE,"E10.bottom");Q1=makeQuery(id+"F5.imprint","IMPRINT",FACE,{"disambiguationData":[TD([[makeQuery(id+"F5.imprint","IMPRINT",EDGE,{"derivedFrom":subQ0}),1.0]])]});}
            var Q2;
            {var subQ0=sQuery(id+"F5.wireOp",EDGE,"E9.left");var subQ1=sQuery(id+"F0.wireOp",EDGE,"E0.left");var subQ2=makeQuery(id+"FlHhq8AFgQTEit1_1.boolean.opBoolean","COPY",EDGE,{"derivedFrom":makeQuery(id+"FlHhq8AFgQTEit1_1.opExtrude","SWEPT_EDGE",EDGE,{"disambiguationData":[OSD([subQ1,sQuery(id+"F3.wireOp",EDGE,"E5.17.0.0"),sQuery(id+"F3.wireOp",EDGE,"E5.17.0.1")])]})});var subQ3=makeQuery(id+"F5.imprint","INTERSECT",VERTEX,{"derivedFrom":[subQ2,subQ0]});Q2=makeQuery(id+"F5.imprint","IMPRINT",FACE,{"disambiguationData":[TD([[makeQuery(id+"F5.imprint","IMPRINT",EDGE,{"disambiguationData":[TD([[subQ3,-1.0]])],"derivedFrom":subQ0}),1.0]])]});}
            var Q3;
            {var subQ0=sQuery(id+"F5.wireOp",EDGE,"E9.left");var subQ1=sQuery(id+"F0.wireOp",EDGE,"E0.left");var subQ2=makeQuery(id+"FlHhq8AFgQTEit1_1.boolean.opBoolean","COPY",EDGE,{"derivedFrom":makeQuery(id+"FlHhq8AFgQTEit1_1.opExtrude","SWEPT_EDGE",EDGE,{"disambiguationData":[OSD([subQ1,sQuery(id+"F3.wireOp",EDGE,"E5.16.0.0"),sQuery(id+"F3.wireOp",EDGE,"E5.16.0.1")])]})});var subQ3=makeQuery(id+"F5.imprint","INTERSECT",VERTEX,{"derivedFrom":[subQ2,subQ0]});Q3=makeQuery(id+"F5.imprint","IMPRINT",FACE,{"disambiguationData":[TD([[makeQuery(id+"F5.imprint","IMPRINT",EDGE,{"disambiguationData":[TD([[subQ3,-1.0]])],"derivedFrom":subQ0}),1.0]])]});}
            var Q4;
            {var subQ0=sQuery(id+"F5.wireOp",EDGE,"E9.left");var subQ1=sQuery(id+"F0.wireOp",EDGE,"E0.left");var subQ2=makeQuery(id+"FlHhq8AFgQTEit1_1.boolean.opBoolean","COPY",EDGE,{"derivedFrom":makeQuery(id+"FlHhq8AFgQTEit1_1.opExtrude","SWEPT_EDGE",EDGE,{"disambiguationData":[OSD([subQ1,sQuery(id+"F3.wireOp",EDGE,"E5.15.0.0"),sQuery(id+"F3.wireOp",EDGE,"E5.15.0.1")])]})});var subQ3=makeQuery(id+"F5.imprint","INTERSECT",VERTEX,{"derivedFrom":[subQ2,subQ0]});Q4=makeQuery(id+"F5.imprint","IMPRINT",FACE,{"disambiguationData":[TD([[makeQuery(id+"F5.imprint","IMPRINT",EDGE,{"disambiguationData":[TD([[subQ3,-1.0]])],"derivedFrom":subQ0}),1.0]])]});}
            var Q5;
            {var subQ0=sQuery(id+"F5.wireOp",EDGE,"E9.left");var subQ1=sQuery(id+"F0.wireOp",EDGE,"E0.left");var subQ2=makeQuery(id+"FlHhq8AFgQTEit1_1.boolean.opBoolean","COPY",EDGE,{"derivedFrom":makeQuery(id+"FlHhq8AFgQTEit1_1.opExtrude","SWEPT_EDGE",EDGE,{"disambiguationData":[OSD([subQ1,sQuery(id+"F3.wireOp",EDGE,"E5.14.0.0"),sQuery(id+"F3.wireOp",EDGE,"E5.14.0.1")])]})});var subQ3=makeQuery(id+"F5.imprint","INTERSECT",VERTEX,{"derivedFrom":[subQ2,subQ0]});Q5=makeQuery(id+"F5.imprint","IMPRINT",FACE,{"disambiguationData":[TD([[makeQuery(id+"F5.imprint","IMPRINT",EDGE,{"disambiguationData":[TD([[subQ3,-1.0]])],"derivedFrom":subQ0}),1.0]])]});}
            var Q6;
            {var subQ0=sQuery(id+"F5.wireOp",EDGE,"E9.left");var subQ1=sQuery(id+"F0.wireOp",EDGE,"E0.left");var subQ2=makeQuery(id+"FlHhq8AFgQTEit1_1.boolean.opBoolean","COPY",EDGE,{"derivedFrom":makeQuery(id+"FlHhq8AFgQTEit1_1.opExtrude","SWEPT_EDGE",EDGE,{"disambiguationData":[OSD([subQ1,sQuery(id+"F3.wireOp",EDGE,"E5.13.0.0"),sQuery(id+"F3.wireOp",EDGE,"E5.13.0.1")])]})});var subQ3=makeQuery(id+"F5.imprint","INTERSECT",VERTEX,{"derivedFrom":[subQ2,subQ0]});Q6=makeQuery(id+"F5.imprint","IMPRINT",FACE,{"disambiguationData":[TD([[makeQuery(id+"F5.imprint","IMPRINT",EDGE,{"disambiguationData":[TD([[subQ3,-1.0]])],"derivedFrom":subQ0}),1.0]])]});}
            var Q7;
            {var subQ7=sQuery(id+"F5.wireOp",EDGE,"E9.left");var subQ9=makeQuery(id+"F5.imprint","INTERSECT",VERTEX,{"derivedFrom":[sQuery(id+"F5.wireOp",EDGE,"E6.top"),subQ7]});Q7=makeQuery(id+"F5.imprint","IMPRINT",FACE,{"disambiguationData":[TD([[makeQuery(id+"F5.imprint","IMPRINT",EDGE,{"disambiguationData":[TD([[subQ9,1.0]])],"derivedFrom":subQ7}),1.0]])]});}
            var Q8;
            {var subQ0=sQuery(id+"F5.wireOp",EDGE,"E12.bottom");var subQ1=sQuery(id+"F5.wireOp",EDGE,"E9.left");var subQ2=makeQuery(id+"F5.imprint","INTERSECT",VERTEX,{"derivedFrom":[subQ1,subQ0]});Q8=makeQuery(id+"F5.imprint","IMPRINT",FACE,{"disambiguationData":[TD([[makeQuery(id+"F5.imprint","IMPRINT",EDGE,{"disambiguationData":[TD([[subQ2,1.0]])],"derivedFrom":subQ1}),1.0]])]});}
            var Q9;
            {var subQ0=sQuery(id+"F5.wireOp",EDGE,"E12.bottom");var subQ1=sQuery(id+"F5.wireOp",EDGE,"E10.left");var subQ2=makeQuery(id+"F5.imprint","INTERSECT",VERTEX,{"derivedFrom":[subQ1,subQ0]});Q9=makeQuery(id+"F5.imprint","IMPRINT",FACE,{"disambiguationData":[TD([[makeQuery(id+"F5.imprint","IMPRINT",EDGE,{"disambiguationData":[TD([[subQ2,1.0]])],"derivedFrom":subQ1}),-1.0]])]});}
            var Q10;
            {var subQ5=sQuery(id+"F5.wireOp",EDGE,"E10.left");var subQ6=makeQuery(id+"F5.imprint","INTERSECT",VERTEX,{"derivedFrom":[sQuery(id+"F5.wireOp",EDGE,"E7.bottom"),subQ5]});Q10=makeQuery(id+"F5.imprint","IMPRINT",FACE,{"disambiguationData":[TD([[makeQuery(id+"F5.imprint","IMPRINT",EDGE,{"disambiguationData":[TD([[subQ6,1.0]])],"derivedFrom":subQ5}),-1.0]])]});}
            var Q11;
            {var subQ0=sQuery(id+"F5.wireOp",EDGE,"E10.left");var subQ1=sQuery(id+"F0.wireOp",EDGE,"E0.left");var subQ2=makeQuery(id+"FlHhq8AFgQTEit1_1.boolean.opBoolean","COPY",EDGE,{"derivedFrom":makeQuery(id+"FlHhq8AFgQTEit1_1.opExtrude","SWEPT_EDGE",EDGE,{"disambiguationData":[OSD([subQ1,sQuery(id+"F3.wireOp",EDGE,"E5.13.0.0"),sQuery(id+"F3.wireOp",EDGE,"E5.13.0.1")])]})});var subQ3=makeQuery(id+"F5.imprint","INTERSECT",VERTEX,{"derivedFrom":[subQ2,subQ0]});Q11=makeQuery(id+"F5.imprint","IMPRINT",FACE,{"disambiguationData":[TD([[makeQuery(id+"F5.imprint","IMPRINT",EDGE,{"disambiguationData":[TD([[subQ3,-1.0]])],"derivedFrom":subQ0}),-1.0]])]});}
            var Q12;
            {var subQ0=sQuery(id+"F5.wireOp",EDGE,"E10.left");var subQ1=sQuery(id+"F0.wireOp",EDGE,"E0.left");var subQ2=makeQuery(id+"FlHhq8AFgQTEit1_1.boolean.opBoolean","COPY",EDGE,{"derivedFrom":makeQuery(id+"FlHhq8AFgQTEit1_1.opExtrude","SWEPT_EDGE",EDGE,{"disambiguationData":[OSD([subQ1,sQuery(id+"F3.wireOp",EDGE,"E5.14.0.0"),sQuery(id+"F3.wireOp",EDGE,"E5.14.0.1")])]})});var subQ3=makeQuery(id+"F5.imprint","INTERSECT",VERTEX,{"derivedFrom":[subQ2,subQ0]});Q12=makeQuery(id+"F5.imprint","IMPRINT",FACE,{"disambiguationData":[TD([[makeQuery(id+"F5.imprint","IMPRINT",EDGE,{"disambiguationData":[TD([[subQ3,-1.0]])],"derivedFrom":subQ0}),-1.0]])]});}
            var Q13;
            {var subQ0=sQuery(id+"F5.wireOp",EDGE,"E10.left");var subQ1=sQuery(id+"F0.wireOp",EDGE,"E0.left");var subQ2=makeQuery(id+"FlHhq8AFgQTEit1_1.boolean.opBoolean","COPY",EDGE,{"derivedFrom":makeQuery(id+"FlHhq8AFgQTEit1_1.opExtrude","SWEPT_EDGE",EDGE,{"disambiguationData":[OSD([subQ1,sQuery(id+"F3.wireOp",EDGE,"E5.15.0.0"),sQuery(id+"F3.wireOp",EDGE,"E5.15.0.1")])]})});var subQ3=makeQuery(id+"F5.imprint","INTERSECT",VERTEX,{"derivedFrom":[subQ2,subQ0]});Q13=makeQuery(id+"F5.imprint","IMPRINT",FACE,{"disambiguationData":[TD([[makeQuery(id+"F5.imprint","IMPRINT",EDGE,{"disambiguationData":[TD([[subQ3,-1.0]])],"derivedFrom":subQ0}),-1.0]])]});}
            var Q14;
            {var subQ0=sQuery(id+"F5.wireOp",EDGE,"E10.left");var subQ1=sQuery(id+"F0.wireOp",EDGE,"E0.left");var subQ2=makeQuery(id+"FlHhq8AFgQTEit1_1.boolean.opBoolean","COPY",EDGE,{"derivedFrom":makeQuery(id+"FlHhq8AFgQTEit1_1.opExtrude","SWEPT_EDGE",EDGE,{"disambiguationData":[OSD([subQ1,sQuery(id+"F3.wireOp",EDGE,"E5.16.0.0"),sQuery(id+"F3.wireOp",EDGE,"E5.16.0.1")])]})});var subQ3=makeQuery(id+"F5.imprint","INTERSECT",VERTEX,{"derivedFrom":[subQ2,subQ0]});Q14=makeQuery(id+"F5.imprint","IMPRINT",FACE,{"disambiguationData":[TD([[makeQuery(id+"F5.imprint","IMPRINT",EDGE,{"disambiguationData":[TD([[subQ3,-1.0]])],"derivedFrom":subQ0}),-1.0]])]});}
            var Q15;
            {var subQ0=sQuery(id+"F5.wireOp",EDGE,"E10.left");var subQ1=sQuery(id+"F0.wireOp",EDGE,"E0.left");var subQ2=makeQuery(id+"FlHhq8AFgQTEit1_1.boolean.opBoolean","COPY",EDGE,{"derivedFrom":makeQuery(id+"FlHhq8AFgQTEit1_1.opExtrude","SWEPT_EDGE",EDGE,{"disambiguationData":[OSD([subQ1,sQuery(id+"F3.wireOp",EDGE,"E5.17.0.0"),sQuery(id+"F3.wireOp",EDGE,"E5.17.0.1")])]})});var subQ3=makeQuery(id+"F5.imprint","INTERSECT",VERTEX,{"derivedFrom":[subQ2,subQ0]});Q15=makeQuery(id+"F5.imprint","IMPRINT",FACE,{"disambiguationData":[TD([[makeQuery(id+"F5.imprint","IMPRINT",EDGE,{"disambiguationData":[TD([[subQ3,-1.0]])],"derivedFrom":subQ0}),-1.0]])]});}
            var Q16;
            {var subQ0=sQuery(id+"F5.wireOp",EDGE,"E10.left");var subQ1=sQuery(id+"F3.wireOp",EDGE,"E5.17.0.1");var subQ2=sQuery(id+"F0.wireOp",EDGE,"E0.left");var subQ3=makeQuery(id+"FlHhq8AFgQTEit1_1.boolean.opBoolean","COPY",EDGE,{"derivedFrom":makeQuery(id+"FlHhq8AFgQTEit1_1.opExtrude","SWEPT_EDGE",EDGE,{"disambiguationData":[OSD([subQ2,subQ1,sQuery(id+"F3.wireOp",EDGE,"E5.17.0.2")])]})});var subQ4=makeQuery(id+"F5.imprint","INTERSECT",VERTEX,{"derivedFrom":[subQ3,subQ0]});Q16=makeQuery(id+"F5.imprint","IMPRINT",FACE,{"disambiguationData":[TD([[makeQuery(id+"F5.imprint","IMPRINT",EDGE,{"disambiguationData":[TD([[subQ4,-1.0]])],"derivedFrom":subQ0}),-1.0]])]});}
            var Q17;
            {var subQ0=sQuery(id+"F5.wireOp",EDGE,"E10.left");var subQ1=sQuery(id+"F3.wireOp",EDGE,"E5.16.0.1");var subQ2=sQuery(id+"F0.wireOp",EDGE,"E0.left");var subQ3=makeQuery(id+"FlHhq8AFgQTEit1_1.boolean.opBoolean","COPY",EDGE,{"derivedFrom":makeQuery(id+"FlHhq8AFgQTEit1_1.opExtrude","SWEPT_EDGE",EDGE,{"disambiguationData":[OSD([subQ2,subQ1,sQuery(id+"F3.wireOp",EDGE,"E5.16.0.2")])]})});var subQ4=makeQuery(id+"F5.imprint","INTERSECT",VERTEX,{"derivedFrom":[subQ3,subQ0]});Q17=makeQuery(id+"F5.imprint","IMPRINT",FACE,{"disambiguationData":[TD([[makeQuery(id+"F5.imprint","IMPRINT",EDGE,{"disambiguationData":[TD([[subQ4,-1.0]])],"derivedFrom":subQ0}),-1.0]])]});}
            var Q18;
            {var subQ0=sQuery(id+"F5.wireOp",EDGE,"E10.left");var subQ1=sQuery(id+"F3.wireOp",EDGE,"E5.15.0.1");var subQ2=sQuery(id+"F0.wireOp",EDGE,"E0.left");var subQ3=makeQuery(id+"FlHhq8AFgQTEit1_1.boolean.opBoolean","COPY",EDGE,{"derivedFrom":makeQuery(id+"FlHhq8AFgQTEit1_1.opExtrude","SWEPT_EDGE",EDGE,{"disambiguationData":[OSD([subQ2,subQ1,sQuery(id+"F3.wireOp",EDGE,"E5.15.0.2")])]})});var subQ4=makeQuery(id+"F5.imprint","INTERSECT",VERTEX,{"derivedFrom":[subQ3,subQ0]});Q18=makeQuery(id+"F5.imprint","IMPRINT",FACE,{"disambiguationData":[TD([[makeQuery(id+"F5.imprint","IMPRINT",EDGE,{"disambiguationData":[TD([[subQ4,-1.0]])],"derivedFrom":subQ0}),-1.0]])]});}
            var Q19;
            {var subQ0=sQuery(id+"F5.wireOp",EDGE,"E10.left");var subQ1=sQuery(id+"F3.wireOp",EDGE,"E5.13.0.1");var subQ2=sQuery(id+"F0.wireOp",EDGE,"E0.left");var subQ3=makeQuery(id+"FlHhq8AFgQTEit1_1.boolean.opBoolean","COPY",EDGE,{"derivedFrom":makeQuery(id+"FlHhq8AFgQTEit1_1.opExtrude","SWEPT_EDGE",EDGE,{"disambiguationData":[OSD([subQ2,subQ1,sQuery(id+"F3.wireOp",EDGE,"E5.13.0.2")])]})});var subQ4=makeQuery(id+"F5.imprint","INTERSECT",VERTEX,{"derivedFrom":[subQ3,subQ0]});Q19=makeQuery(id+"F5.imprint","IMPRINT",FACE,{"disambiguationData":[TD([[makeQuery(id+"F5.imprint","IMPRINT",EDGE,{"disambiguationData":[TD([[subQ4,-1.0]])],"derivedFrom":subQ0}),-1.0]])]});}
            var Q20;
            {var subQ0=sQuery(id+"F5.wireOp",EDGE,"E10.left");var subQ1=sQuery(id+"F3.wireOp",EDGE,"E5.12.0.1");var subQ2=sQuery(id+"F0.wireOp",EDGE,"E0.left");var subQ3=makeQuery(id+"FlHhq8AFgQTEit1_1.boolean.opBoolean","COPY",EDGE,{"derivedFrom":makeQuery(id+"FlHhq8AFgQTEit1_1.opExtrude","SWEPT_EDGE",EDGE,{"disambiguationData":[OSD([subQ2,subQ1,sQuery(id+"F3.wireOp",EDGE,"E5.12.0.2")])]})});var subQ4=makeQuery(id+"F5.imprint","INTERSECT",VERTEX,{"derivedFrom":[subQ3,subQ0]});Q20=makeQuery(id+"F5.imprint","IMPRINT",FACE,{"disambiguationData":[TD([[makeQuery(id+"F5.imprint","IMPRINT",EDGE,{"disambiguationData":[TD([[subQ4,-1.0]])],"derivedFrom":subQ0}),-1.0]])]});}
            var Q21;
            {var subQ0=sQuery(id+"F5.wireOp",EDGE,"E10.left");var subQ1=sQuery(id+"F3.wireOp",EDGE,"E5.11.0.1");var subQ2=sQuery(id+"F0.wireOp",EDGE,"E0.left");var subQ3=makeQuery(id+"FlHhq8AFgQTEit1_1.boolean.opBoolean","COPY",EDGE,{"derivedFrom":makeQuery(id+"FlHhq8AFgQTEit1_1.opExtrude","SWEPT_EDGE",EDGE,{"disambiguationData":[OSD([subQ2,subQ1,sQuery(id+"F3.wireOp",EDGE,"E5.11.0.2")])]})});var subQ4=makeQuery(id+"F5.imprint","INTERSECT",VERTEX,{"derivedFrom":[subQ3,subQ0]});Q21=makeQuery(id+"F5.imprint","IMPRINT",FACE,{"disambiguationData":[TD([[makeQuery(id+"F5.imprint","IMPRINT",EDGE,{"disambiguationData":[TD([[subQ4,-1.0]])],"derivedFrom":subQ0}),-1.0]])]});}
            var Q22;
            {var subQ0=sQuery(id+"F5.wireOp",EDGE,"E9.left");var subQ1=sQuery(id+"F3.wireOp",EDGE,"E5.12.0.1");var subQ2=sQuery(id+"F0.wireOp",EDGE,"E0.left");var subQ3=makeQuery(id+"FlHhq8AFgQTEit1_1.boolean.opBoolean","COPY",EDGE,{"derivedFrom":makeQuery(id+"FlHhq8AFgQTEit1_1.opExtrude","SWEPT_EDGE",EDGE,{"disambiguationData":[OSD([subQ2,subQ1,sQuery(id+"F3.wireOp",EDGE,"E5.12.0.2")])]})});var subQ4=makeQuery(id+"F5.imprint","INTERSECT",VERTEX,{"derivedFrom":[subQ3,subQ0]});Q22=makeQuery(id+"F5.imprint","IMPRINT",FACE,{"disambiguationData":[TD([[makeQuery(id+"F5.imprint","IMPRINT",EDGE,{"disambiguationData":[TD([[subQ4,-1.0]])],"derivedFrom":subQ0}),1.0]])]});}
            var Q23;
            {var subQ0=sQuery(id+"F5.wireOp",EDGE,"E9.left");var subQ1=sQuery(id+"F3.wireOp",EDGE,"E5.11.0.1");var subQ2=sQuery(id+"F0.wireOp",EDGE,"E0.left");var subQ3=makeQuery(id+"FlHhq8AFgQTEit1_1.boolean.opBoolean","COPY",EDGE,{"derivedFrom":makeQuery(id+"FlHhq8AFgQTEit1_1.opExtrude","SWEPT_EDGE",EDGE,{"disambiguationData":[OSD([subQ2,subQ1,sQuery(id+"F3.wireOp",EDGE,"E5.11.0.2")])]})});var subQ4=makeQuery(id+"F5.imprint","INTERSECT",VERTEX,{"derivedFrom":[subQ3,subQ0]});Q23=makeQuery(id+"F5.imprint","IMPRINT",FACE,{"disambiguationData":[TD([[makeQuery(id+"F5.imprint","IMPRINT",EDGE,{"disambiguationData":[TD([[subQ4,-1.0]])],"derivedFrom":subQ0}),1.0]])]});}
            var Q24;
            {var subQ0=sQuery(id+"F5.wireOp",EDGE,"E9.left");var subQ1=sQuery(id+"F3.wireOp",EDGE,"E5.13.0.1");var subQ2=sQuery(id+"F0.wireOp",EDGE,"E0.left");var subQ3=makeQuery(id+"FlHhq8AFgQTEit1_1.boolean.opBoolean","COPY",EDGE,{"derivedFrom":makeQuery(id+"FlHhq8AFgQTEit1_1.opExtrude","SWEPT_EDGE",EDGE,{"disambiguationData":[OSD([subQ2,subQ1,sQuery(id+"F3.wireOp",EDGE,"E5.13.0.2")])]})});var subQ4=makeQuery(id+"F5.imprint","INTERSECT",VERTEX,{"derivedFrom":[subQ3,subQ0]});Q24=makeQuery(id+"F5.imprint","IMPRINT",FACE,{"disambiguationData":[TD([[makeQuery(id+"F5.imprint","IMPRINT",EDGE,{"disambiguationData":[TD([[subQ4,-1.0]])],"derivedFrom":subQ0}),1.0]])]});}
            var Q25;
            {var subQ0=sQuery(id+"F5.wireOp",EDGE,"E9.left");var subQ1=sQuery(id+"F3.wireOp",EDGE,"E5.15.0.1");var subQ2=sQuery(id+"F0.wireOp",EDGE,"E0.left");var subQ3=makeQuery(id+"FlHhq8AFgQTEit1_1.boolean.opBoolean","COPY",EDGE,{"derivedFrom":makeQuery(id+"FlHhq8AFgQTEit1_1.opExtrude","SWEPT_EDGE",EDGE,{"disambiguationData":[OSD([subQ2,subQ1,sQuery(id+"F3.wireOp",EDGE,"E5.15.0.2")])]})});var subQ4=makeQuery(id+"F5.imprint","INTERSECT",VERTEX,{"derivedFrom":[subQ3,subQ0]});Q25=makeQuery(id+"F5.imprint","IMPRINT",FACE,{"disambiguationData":[TD([[makeQuery(id+"F5.imprint","IMPRINT",EDGE,{"disambiguationData":[TD([[subQ4,-1.0]])],"derivedFrom":subQ0}),1.0]])]});}
            var Q26;
            {var subQ0=sQuery(id+"F5.wireOp",EDGE,"E9.left");var subQ1=sQuery(id+"F3.wireOp",EDGE,"E5.14.0.1");var subQ2=sQuery(id+"F0.wireOp",EDGE,"E0.left");var subQ3=makeQuery(id+"FlHhq8AFgQTEit1_1.boolean.opBoolean","COPY",EDGE,{"derivedFrom":makeQuery(id+"FlHhq8AFgQTEit1_1.opExtrude","SWEPT_EDGE",EDGE,{"disambiguationData":[OSD([subQ2,subQ1,sQuery(id+"F3.wireOp",EDGE,"E5.14.0.2")])]})});var subQ4=makeQuery(id+"F5.imprint","INTERSECT",VERTEX,{"derivedFrom":[subQ3,subQ0]});Q26=makeQuery(id+"F5.imprint","IMPRINT",FACE,{"disambiguationData":[TD([[makeQuery(id+"F5.imprint","IMPRINT",EDGE,{"disambiguationData":[TD([[subQ4,-1.0]])],"derivedFrom":subQ0}),1.0]])]});}
            var Q27;
            {var subQ0=sQuery(id+"F5.wireOp",EDGE,"E9.left");var subQ1=sQuery(id+"F3.wireOp",EDGE,"E5.17.0.1");var subQ2=sQuery(id+"F0.wireOp",EDGE,"E0.left");var subQ3=makeQuery(id+"FlHhq8AFgQTEit1_1.boolean.opBoolean","COPY",EDGE,{"derivedFrom":makeQuery(id+"FlHhq8AFgQTEit1_1.opExtrude","SWEPT_EDGE",EDGE,{"disambiguationData":[OSD([subQ2,subQ1,sQuery(id+"F3.wireOp",EDGE,"E5.17.0.2")])]})});var subQ4=makeQuery(id+"F5.imprint","INTERSECT",VERTEX,{"derivedFrom":[subQ3,subQ0]});Q27=makeQuery(id+"F5.imprint","IMPRINT",FACE,{"disambiguationData":[TD([[makeQuery(id+"F5.imprint","IMPRINT",EDGE,{"disambiguationData":[TD([[subQ4,-1.0]])],"derivedFrom":subQ0}),1.0]])]});}
            var Q28;
            {var subQ0=sQuery(id+"F5.wireOp",EDGE,"E9.left");var subQ1=sQuery(id+"F3.wireOp",EDGE,"E5.16.0.1");var subQ2=sQuery(id+"F0.wireOp",EDGE,"E0.left");var subQ3=makeQuery(id+"FlHhq8AFgQTEit1_1.boolean.opBoolean","COPY",EDGE,{"derivedFrom":makeQuery(id+"FlHhq8AFgQTEit1_1.opExtrude","SWEPT_EDGE",EDGE,{"disambiguationData":[OSD([subQ2,subQ1,sQuery(id+"F3.wireOp",EDGE,"E5.16.0.2")])]})});var subQ4=makeQuery(id+"F5.imprint","INTERSECT",VERTEX,{"derivedFrom":[subQ3,subQ0]});Q28=makeQuery(id+"F5.imprint","IMPRINT",FACE,{"disambiguationData":[TD([[makeQuery(id+"F5.imprint","IMPRINT",EDGE,{"disambiguationData":[TD([[subQ4,-1.0]])],"derivedFrom":subQ0}),1.0]])]});}
            var Q29;
            {var subQ0=sQuery(id+"F5.wireOp",EDGE,"E10.left");var subQ1=sQuery(id+"F3.wireOp",EDGE,"E5.14.0.1");var subQ2=sQuery(id+"F0.wireOp",EDGE,"E0.left");var subQ3=makeQuery(id+"FlHhq8AFgQTEit1_1.boolean.opBoolean","COPY",EDGE,{"derivedFrom":makeQuery(id+"FlHhq8AFgQTEit1_1.opExtrude","SWEPT_EDGE",EDGE,{"disambiguationData":[OSD([subQ2,subQ1,sQuery(id+"F3.wireOp",EDGE,"E5.14.0.2")])]})});var subQ4=makeQuery(id+"F5.imprint","INTERSECT",VERTEX,{"derivedFrom":[subQ3,subQ0]});Q29=makeQuery(id+"F5.imprint","IMPRINT",FACE,{"disambiguationData":[TD([[makeQuery(id+"F5.imprint","IMPRINT",EDGE,{"disambiguationData":[TD([[subQ4,-1.0]])],"derivedFrom":subQ0}),-1.0]])]});}
            extrude(context, id + "F8", {"entities" : qUnion([Q0, Q1, Q2, Q3, Q4, Q5, Q6, Q7, Q8, Q9, Q10, Q11, Q12, Q13, Q14, Q15, Q16, Q17, Q18, Q19, Q20, Q21, Q22, Q23, Q24, Q25, Q26, Q27, Q28, Q29]), "depth" : 304.8 * mm, "offsetDistance" : 25.4 * mm});
        }
        {
            var Q0;
            {var subQ0=sQuery(id+"F5.wireOp",EDGE,"E12.top");Q0=makeQuery(id+"F5.imprint","IMPRINT",FACE,{"disambiguationData":[TD([[makeQuery(id+"F5.imprint","IMPRINT",EDGE,{"derivedFrom":subQ0}),-1.0]])]});}
            var Q1;
            {var subQ1=sQuery(id+"F5.wireOp",EDGE,"E12.bottom");var subQ11=makeQuery(id+"F5.imprint","INTERSECT",VERTEX,{"derivedFrom":[sQuery(id+"F5.wireOp",EDGE,"E9.left"),subQ1]});Q1=makeQuery(id+"F5.imprint","IMPRINT",FACE,{"disambiguationData":[TD([[makeQuery(id+"F5.imprint","IMPRINT",EDGE,{"disambiguationData":[TD([[subQ11,1.0]])],"derivedFrom":subQ1}),-1.0]])]});}
            extrude(context, id + "F9", {"entities" : qUnion([Q0, Q1]), "depth" : 381 * mm, "offsetDistance" : 25.4 * mm});
        }
        {
            var Q0;
            Q0=makeQuery(id+"F5.imprint","IMPRINT",FACE,{"disambiguationData":[TD([[makeQuery(id+"F5.imprint","IMPRINT",EDGE,{"derivedFrom":sQuery(id+"F5.wireOp",EDGE,"E23.bottom")}),-1.0]])]});
            var Q1;
            {var subQ0=sQuery(id+"F5.wireOp",EDGE,"E23.left");var subQ1=sQuery(id+"F0.wireOp",EDGE,"E0.left");var subQ2=makeQuery(id+"FlHhq8AFgQTEit1_1.boolean.opBoolean","COPY",EDGE,{"derivedFrom":makeQuery(id+"FlHhq8AFgQTEit1_1.opExtrude","SWEPT_EDGE",EDGE,{"disambiguationData":[OSD([subQ1,sQuery(id+"F3.wireOp",EDGE,"E5.2.0.1"),sQuery(id+"F3.wireOp",EDGE,"E5.2.0.2")])]})});var subQ3=makeQuery(id+"F5.imprint","INTERSECT",VERTEX,{"derivedFrom":[subQ2,subQ0]});Q1=makeQuery(id+"F5.imprint","IMPRINT",FACE,{"disambiguationData":[TD([[makeQuery(id+"F5.imprint","IMPRINT",EDGE,{"disambiguationData":[TD([[subQ3,-1.0]])],"derivedFrom":subQ0}),1.0]])]});}
            var Q2;
            {var subQ0=sQuery(id+"F5.wireOp",EDGE,"E23.left");var subQ1=sQuery(id+"F0.wireOp",EDGE,"E0.left");var subQ2=makeQuery(id+"FlHhq8AFgQTEit1_1.boolean.opBoolean","COPY",EDGE,{"derivedFrom":makeQuery(id+"FlHhq8AFgQTEit1_1.opExtrude","SWEPT_EDGE",EDGE,{"disambiguationData":[OSD([subQ1,sQuery(id+"F3.wireOp",EDGE,"E5.3.0.1"),sQuery(id+"F3.wireOp",EDGE,"E5.3.0.2")])]})});var subQ3=makeQuery(id+"F5.imprint","INTERSECT",VERTEX,{"derivedFrom":[subQ2,subQ0]});Q2=makeQuery(id+"F5.imprint","IMPRINT",FACE,{"disambiguationData":[TD([[makeQuery(id+"F5.imprint","IMPRINT",EDGE,{"disambiguationData":[TD([[subQ3,-1.0]])],"derivedFrom":subQ0}),1.0]])]});}
            var Q3;
            {var subQ0=sQuery(id+"F5.wireOp",EDGE,"E23.left");var subQ1=sQuery(id+"F0.wireOp",EDGE,"E0.left");var subQ2=makeQuery(id+"FlHhq8AFgQTEit1_1.boolean.opBoolean","COPY",EDGE,{"derivedFrom":makeQuery(id+"FlHhq8AFgQTEit1_1.opExtrude","SWEPT_EDGE",EDGE,{"disambiguationData":[OSD([subQ1,sQuery(id+"F3.wireOp",EDGE,"E5.4.0.1"),sQuery(id+"F3.wireOp",EDGE,"E5.4.0.2")])]})});var subQ3=makeQuery(id+"F5.imprint","INTERSECT",VERTEX,{"derivedFrom":[subQ2,subQ0]});Q3=makeQuery(id+"F5.imprint","IMPRINT",FACE,{"disambiguationData":[TD([[makeQuery(id+"F5.imprint","IMPRINT",EDGE,{"disambiguationData":[TD([[subQ3,-1.0]])],"derivedFrom":subQ0}),1.0]])]});}
            var Q4;
            {var subQ0=sQuery(id+"F5.wireOp",EDGE,"E23.left");var subQ1=sQuery(id+"F0.wireOp",EDGE,"E0.left");var subQ2=makeQuery(id+"FlHhq8AFgQTEit1_1.boolean.opBoolean","COPY",EDGE,{"derivedFrom":makeQuery(id+"FlHhq8AFgQTEit1_1.opExtrude","SWEPT_EDGE",EDGE,{"disambiguationData":[OSD([subQ1,sQuery(id+"F3.wireOp",EDGE,"E5.5.0.1"),sQuery(id+"F3.wireOp",EDGE,"E5.5.0.2")])]})});var subQ3=makeQuery(id+"F5.imprint","INTERSECT",VERTEX,{"derivedFrom":[subQ2,subQ0]});Q4=makeQuery(id+"F5.imprint","IMPRINT",FACE,{"disambiguationData":[TD([[makeQuery(id+"F5.imprint","IMPRINT",EDGE,{"disambiguationData":[TD([[subQ3,-1.0]])],"derivedFrom":subQ0}),1.0]])]});}
            var Q5;
            {var subQ0=sQuery(id+"F5.wireOp",EDGE,"E23.left");var subQ1=sQuery(id+"F0.wireOp",EDGE,"E0.left");var subQ2=makeQuery(id+"FlHhq8AFgQTEit1_1.boolean.opBoolean","COPY",EDGE,{"derivedFrom":makeQuery(id+"FlHhq8AFgQTEit1_1.opExtrude","SWEPT_EDGE",EDGE,{"disambiguationData":[OSD([subQ1,sQuery(id+"F3.wireOp",EDGE,"E5.6.0.1"),sQuery(id+"F3.wireOp",EDGE,"E5.6.0.2")])]})});var subQ3=makeQuery(id+"F5.imprint","INTERSECT",VERTEX,{"derivedFrom":[subQ2,subQ0]});Q5=makeQuery(id+"F5.imprint","IMPRINT",FACE,{"disambiguationData":[TD([[makeQuery(id+"F5.imprint","IMPRINT",EDGE,{"disambiguationData":[TD([[subQ3,-1.0]])],"derivedFrom":subQ0}),1.0]])]});}
            var Q6;
            {var subQ0=sQuery(id+"F5.wireOp",EDGE,"E23.top");Q6=makeQuery(id+"F5.imprint","IMPRINT",FACE,{"disambiguationData":[TD([[makeQuery(id+"F5.imprint","IMPRINT",EDGE,{"derivedFrom":subQ0}),1.0]])]});}
            var Q7;
            {var subQ0=sQuery(id+"F5.wireOp",EDGE,"E23.left");var subQ1=sQuery(id+"F3.wireOp",EDGE,"E5.7.0.1");var subQ2=sQuery(id+"F0.wireOp",EDGE,"E0.left");var subQ3=makeQuery(id+"FlHhq8AFgQTEit1_1.boolean.opBoolean","COPY",EDGE,{"derivedFrom":makeQuery(id+"FlHhq8AFgQTEit1_1.opExtrude","SWEPT_EDGE",EDGE,{"disambiguationData":[OSD([subQ2,sQuery(id+"F3.wireOp",EDGE,"E5.7.0.0"),subQ1])]})});var subQ4=makeQuery(id+"F5.imprint","INTERSECT",VERTEX,{"derivedFrom":[subQ3,subQ0]});Q7=makeQuery(id+"F5.imprint","IMPRINT",FACE,{"disambiguationData":[TD([[makeQuery(id+"F5.imprint","IMPRINT",EDGE,{"disambiguationData":[TD([[subQ4,-1.0]])],"derivedFrom":subQ0}),1.0]])]});}
            var Q8;
            {var subQ0=sQuery(id+"F5.wireOp",EDGE,"E23.left");var subQ1=sQuery(id+"F3.wireOp",EDGE,"E5.6.0.1");var subQ2=sQuery(id+"F0.wireOp",EDGE,"E0.left");var subQ3=makeQuery(id+"FlHhq8AFgQTEit1_1.boolean.opBoolean","COPY",EDGE,{"derivedFrom":makeQuery(id+"FlHhq8AFgQTEit1_1.opExtrude","SWEPT_EDGE",EDGE,{"disambiguationData":[OSD([subQ2,sQuery(id+"F3.wireOp",EDGE,"E5.6.0.0"),subQ1])]})});var subQ4=makeQuery(id+"F5.imprint","INTERSECT",VERTEX,{"derivedFrom":[subQ3,subQ0]});Q8=makeQuery(id+"F5.imprint","IMPRINT",FACE,{"disambiguationData":[TD([[makeQuery(id+"F5.imprint","IMPRINT",EDGE,{"disambiguationData":[TD([[subQ4,-1.0]])],"derivedFrom":subQ0}),1.0]])]});}
            var Q9;
            {var subQ0=sQuery(id+"F5.wireOp",EDGE,"E23.left");var subQ1=sQuery(id+"F3.wireOp",EDGE,"E5.5.0.1");var subQ2=sQuery(id+"F0.wireOp",EDGE,"E0.left");var subQ3=makeQuery(id+"FlHhq8AFgQTEit1_1.boolean.opBoolean","COPY",EDGE,{"derivedFrom":makeQuery(id+"FlHhq8AFgQTEit1_1.opExtrude","SWEPT_EDGE",EDGE,{"disambiguationData":[OSD([subQ2,sQuery(id+"F3.wireOp",EDGE,"E5.5.0.0"),subQ1])]})});var subQ4=makeQuery(id+"F5.imprint","INTERSECT",VERTEX,{"derivedFrom":[subQ3,subQ0]});Q9=makeQuery(id+"F5.imprint","IMPRINT",FACE,{"disambiguationData":[TD([[makeQuery(id+"F5.imprint","IMPRINT",EDGE,{"disambiguationData":[TD([[subQ4,-1.0]])],"derivedFrom":subQ0}),1.0]])]});}
            var Q10;
            {var subQ0=sQuery(id+"F5.wireOp",EDGE,"E23.left");var subQ1=sQuery(id+"F3.wireOp",EDGE,"E5.4.0.1");var subQ2=sQuery(id+"F0.wireOp",EDGE,"E0.left");var subQ3=makeQuery(id+"FlHhq8AFgQTEit1_1.boolean.opBoolean","COPY",EDGE,{"derivedFrom":makeQuery(id+"FlHhq8AFgQTEit1_1.opExtrude","SWEPT_EDGE",EDGE,{"disambiguationData":[OSD([subQ2,sQuery(id+"F3.wireOp",EDGE,"E5.4.0.0"),subQ1])]})});var subQ4=makeQuery(id+"F5.imprint","INTERSECT",VERTEX,{"derivedFrom":[subQ3,subQ0]});Q10=makeQuery(id+"F5.imprint","IMPRINT",FACE,{"disambiguationData":[TD([[makeQuery(id+"F5.imprint","IMPRINT",EDGE,{"disambiguationData":[TD([[subQ4,-1.0]])],"derivedFrom":subQ0}),1.0]])]});}
            var Q11;
            {var subQ0=sQuery(id+"F5.wireOp",EDGE,"E23.left");var subQ1=sQuery(id+"F3.wireOp",EDGE,"E5.3.0.1");var subQ2=sQuery(id+"F0.wireOp",EDGE,"E0.left");var subQ3=makeQuery(id+"FlHhq8AFgQTEit1_1.boolean.opBoolean","COPY",EDGE,{"derivedFrom":makeQuery(id+"FlHhq8AFgQTEit1_1.opExtrude","SWEPT_EDGE",EDGE,{"disambiguationData":[OSD([subQ2,sQuery(id+"F3.wireOp",EDGE,"E5.3.0.0"),subQ1])]})});var subQ4=makeQuery(id+"F5.imprint","INTERSECT",VERTEX,{"derivedFrom":[subQ3,subQ0]});Q11=makeQuery(id+"F5.imprint","IMPRINT",FACE,{"disambiguationData":[TD([[makeQuery(id+"F5.imprint","IMPRINT",EDGE,{"disambiguationData":[TD([[subQ4,-1.0]])],"derivedFrom":subQ0}),1.0]])]});}
            var Q12;
            {var subQ0=sQuery(id+"F5.wireOp",EDGE,"E23.left");var subQ1=sQuery(id+"F3.wireOp",EDGE,"E5.2.0.1");var subQ2=sQuery(id+"F0.wireOp",EDGE,"E0.left");var subQ3=makeQuery(id+"FlHhq8AFgQTEit1_1.boolean.opBoolean","COPY",EDGE,{"derivedFrom":makeQuery(id+"FlHhq8AFgQTEit1_1.opExtrude","SWEPT_EDGE",EDGE,{"disambiguationData":[OSD([subQ2,sQuery(id+"F3.wireOp",EDGE,"E5.2.0.0"),subQ1])]})});var subQ4=makeQuery(id+"F5.imprint","INTERSECT",VERTEX,{"derivedFrom":[subQ3,subQ0]});Q12=makeQuery(id+"F5.imprint","IMPRINT",FACE,{"disambiguationData":[TD([[makeQuery(id+"F5.imprint","IMPRINT",EDGE,{"disambiguationData":[TD([[subQ4,-1.0]])],"derivedFrom":subQ0}),1.0]])]});}
            extrude(context, id + "F10", {"entities" : qUnion([Q0, Q1, Q2, Q3, Q4, Q5, Q6, Q7, Q8, Q9, Q10, Q11, Q12]), "depth" : 133.35 * mm, "offsetDistance" : 25.4 * mm});
        }
        {
            var Q0;
            {var subQ0=sQuery(id+"F5.wireOp",EDGE,"E15.bottom");Q0=makeQuery(id+"F5.imprint","IMPRINT",FACE,{"disambiguationData":[TD([[makeQuery(id+"F5.imprint","IMPRINT",EDGE,{"derivedFrom":subQ0}),1.0]])]});}
            var Q1;
            {var subQ2=sQuery(id+"F5.wireOp",EDGE,"E29.bottom");Q1=makeQuery(id+"F5.imprint","IMPRINT",FACE,{"disambiguationData":[TD([[makeQuery(id+"F5.imprint","IMPRINT",EDGE,{"derivedFrom":subQ2}),1.0]])]});}
            var Q2;
            {var subQ0=sQuery(id+"F5.wireOp",EDGE,"E14.bottom");Q2=makeQuery(id+"F5.imprint","IMPRINT",FACE,{"disambiguationData":[TD([[makeQuery(id+"F5.imprint","IMPRINT",EDGE,{"derivedFrom":subQ0}),1.0]])]});}
            var Q3;
            {var subQ0=sQuery(id+"F5.wireOp",EDGE,"E13.bottom");Q3=makeQuery(id+"F5.imprint","IMPRINT",FACE,{"disambiguationData":[TD([[makeQuery(id+"F5.imprint","IMPRINT",EDGE,{"derivedFrom":subQ0}),1.0]])]});}
            var Q4;
            {var subQ2=sQuery(id+"F5.wireOp",EDGE,"E28.bottom");Q4=makeQuery(id+"F5.imprint","IMPRINT",FACE,{"disambiguationData":[TD([[makeQuery(id+"F5.imprint","IMPRINT",EDGE,{"derivedFrom":subQ2}),1.0]])]});}
            var Q5;
            {var subQ0=sQuery(id+"F5.wireOp",EDGE,"E16.bottom");Q5=makeQuery(id+"F5.imprint","IMPRINT",FACE,{"disambiguationData":[TD([[makeQuery(id+"F5.imprint","IMPRINT",EDGE,{"derivedFrom":subQ0}),1.0]])]});}
            var Q6;
            {var subQ0=sQuery(id+"F5.wireOp",EDGE,"E13.left");var subQ1=sQuery(id+"F3.wireOp",EDGE,"E5.15.0.1");var subQ2=sQuery(id+"F0.wireOp",EDGE,"E0.left");var subQ3=makeQuery(id+"FlHhq8AFgQTEit1_1.boolean.opBoolean","COPY",EDGE,{"derivedFrom":makeQuery(id+"FlHhq8AFgQTEit1_1.opExtrude","SWEPT_EDGE",EDGE,{"disambiguationData":[OSD([subQ2,subQ1,sQuery(id+"F3.wireOp",EDGE,"E5.15.0.2")])]})});var subQ4=makeQuery(id+"F5.imprint","INTERSECT",VERTEX,{"derivedFrom":[subQ3,subQ0]});Q6=makeQuery(id+"F5.imprint","IMPRINT",FACE,{"disambiguationData":[TD([[makeQuery(id+"F5.imprint","IMPRINT",EDGE,{"disambiguationData":[TD([[subQ4,-1.0]])],"derivedFrom":subQ0}),1.0]])]});}
            var Q7;
            {var subQ0=sQuery(id+"F5.wireOp",EDGE,"E13.left");var subQ1=sQuery(id+"F0.wireOp",EDGE,"E0.left");var subQ2=makeQuery(id+"FlHhq8AFgQTEit1_1.boolean.opBoolean","COPY",EDGE,{"derivedFrom":makeQuery(id+"FlHhq8AFgQTEit1_1.opExtrude","SWEPT_EDGE",EDGE,{"disambiguationData":[OSD([subQ1,sQuery(id+"F3.wireOp",EDGE,"E5.17.0.0"),sQuery(id+"F3.wireOp",EDGE,"E5.17.0.1")])]})});var subQ3=makeQuery(id+"F5.imprint","INTERSECT",VERTEX,{"derivedFrom":[subQ2,subQ0]});Q7=makeQuery(id+"F5.imprint","IMPRINT",FACE,{"disambiguationData":[TD([[makeQuery(id+"F5.imprint","IMPRINT",EDGE,{"disambiguationData":[TD([[subQ3,-1.0]])],"derivedFrom":subQ0}),1.0]])]});}
            var Q8;
            {var subQ0=sQuery(id+"F5.wireOp",EDGE,"E13.left");var subQ1=sQuery(id+"F0.wireOp",EDGE,"E0.left");var subQ2=makeQuery(id+"FlHhq8AFgQTEit1_1.boolean.opBoolean","COPY",EDGE,{"derivedFrom":makeQuery(id+"FlHhq8AFgQTEit1_1.opExtrude","SWEPT_EDGE",EDGE,{"disambiguationData":[OSD([subQ1,sQuery(id+"F3.wireOp",EDGE,"E5.13.0.0"),sQuery(id+"F3.wireOp",EDGE,"E5.13.0.1")])]})});var subQ3=makeQuery(id+"F5.imprint","INTERSECT",VERTEX,{"derivedFrom":[subQ2,subQ0]});Q8=makeQuery(id+"F5.imprint","IMPRINT",FACE,{"disambiguationData":[TD([[makeQuery(id+"F5.imprint","IMPRINT",EDGE,{"disambiguationData":[TD([[subQ3,-1.0]])],"derivedFrom":subQ0}),1.0]])]});}
            var Q9;
            {var subQ0=sQuery(id+"F5.wireOp",EDGE,"E13.left");var subQ1=sQuery(id+"F3.wireOp",EDGE,"E5.17.0.1");var subQ2=sQuery(id+"F0.wireOp",EDGE,"E0.left");var subQ3=makeQuery(id+"FlHhq8AFgQTEit1_1.boolean.opBoolean","COPY",EDGE,{"derivedFrom":makeQuery(id+"FlHhq8AFgQTEit1_1.opExtrude","SWEPT_EDGE",EDGE,{"disambiguationData":[OSD([subQ2,subQ1,sQuery(id+"F3.wireOp",EDGE,"E5.17.0.2")])]})});var subQ4=makeQuery(id+"F5.imprint","INTERSECT",VERTEX,{"derivedFrom":[subQ3,subQ0]});Q9=makeQuery(id+"F5.imprint","IMPRINT",FACE,{"disambiguationData":[TD([[makeQuery(id+"F5.imprint","IMPRINT",EDGE,{"disambiguationData":[TD([[subQ4,-1.0]])],"derivedFrom":subQ0}),1.0]])]});}
            var Q10;
            {var subQ0=sQuery(id+"F5.wireOp",EDGE,"E13.left");var subQ1=sQuery(id+"F3.wireOp",EDGE,"E5.16.0.1");var subQ2=sQuery(id+"F0.wireOp",EDGE,"E0.left");var subQ3=makeQuery(id+"FlHhq8AFgQTEit1_1.boolean.opBoolean","COPY",EDGE,{"derivedFrom":makeQuery(id+"FlHhq8AFgQTEit1_1.opExtrude","SWEPT_EDGE",EDGE,{"disambiguationData":[OSD([subQ2,subQ1,sQuery(id+"F3.wireOp",EDGE,"E5.16.0.2")])]})});var subQ4=makeQuery(id+"F5.imprint","INTERSECT",VERTEX,{"derivedFrom":[subQ3,subQ0]});Q10=makeQuery(id+"F5.imprint","IMPRINT",FACE,{"disambiguationData":[TD([[makeQuery(id+"F5.imprint","IMPRINT",EDGE,{"disambiguationData":[TD([[subQ4,-1.0]])],"derivedFrom":subQ0}),1.0]])]});}
            var Q11;
            {var subQ0=sQuery(id+"F5.wireOp",EDGE,"E13.left");var subQ1=sQuery(id+"F3.wireOp",EDGE,"E5.14.0.1");var subQ2=sQuery(id+"F0.wireOp",EDGE,"E0.left");var subQ3=makeQuery(id+"FlHhq8AFgQTEit1_1.boolean.opBoolean","COPY",EDGE,{"derivedFrom":makeQuery(id+"FlHhq8AFgQTEit1_1.opExtrude","SWEPT_EDGE",EDGE,{"disambiguationData":[OSD([subQ2,subQ1,sQuery(id+"F3.wireOp",EDGE,"E5.14.0.2")])]})});var subQ4=makeQuery(id+"F5.imprint","INTERSECT",VERTEX,{"derivedFrom":[subQ3,subQ0]});Q11=makeQuery(id+"F5.imprint","IMPRINT",FACE,{"disambiguationData":[TD([[makeQuery(id+"F5.imprint","IMPRINT",EDGE,{"disambiguationData":[TD([[subQ4,-1.0]])],"derivedFrom":subQ0}),1.0]])]});}
            var Q12;
            {var subQ0=sQuery(id+"F5.wireOp",EDGE,"E13.left");var subQ1=sQuery(id+"F3.wireOp",EDGE,"E5.12.0.1");var subQ2=sQuery(id+"F0.wireOp",EDGE,"E0.left");var subQ3=makeQuery(id+"FlHhq8AFgQTEit1_1.boolean.opBoolean","COPY",EDGE,{"derivedFrom":makeQuery(id+"FlHhq8AFgQTEit1_1.opExtrude","SWEPT_EDGE",EDGE,{"disambiguationData":[OSD([subQ2,subQ1,sQuery(id+"F3.wireOp",EDGE,"E5.12.0.2")])]})});var subQ4=makeQuery(id+"F5.imprint","INTERSECT",VERTEX,{"derivedFrom":[subQ3,subQ0]});Q12=makeQuery(id+"F5.imprint","IMPRINT",FACE,{"disambiguationData":[TD([[makeQuery(id+"F5.imprint","IMPRINT",EDGE,{"disambiguationData":[TD([[subQ4,-1.0]])],"derivedFrom":subQ0}),1.0]])]});}
            var Q13;
            {var subQ0=sQuery(id+"F5.wireOp",EDGE,"E18.top");var subQ5=sQuery(id+"F5.wireOp",EDGE,"E13.right");var subQ6=makeQuery(id+"F5.imprint","INTERSECT",VERTEX,{"derivedFrom":[subQ5,subQ0]});Q13=makeQuery(id+"F5.imprint","IMPRINT",FACE,{"disambiguationData":[TD([[makeQuery(id+"F5.imprint","IMPRINT",EDGE,{"disambiguationData":[TD([[subQ6,-1.0]])],"derivedFrom":subQ0}),-1.0]])]});}
            var Q14;
            {var subQ0=sQuery(id+"F5.wireOp",EDGE,"E13.left");var subQ1=sQuery(id+"F0.wireOp",EDGE,"E0.left");var subQ2=makeQuery(id+"FlHhq8AFgQTEit1_1.boolean.opBoolean","COPY",EDGE,{"derivedFrom":makeQuery(id+"FlHhq8AFgQTEit1_1.opExtrude","SWEPT_EDGE",EDGE,{"disambiguationData":[OSD([subQ1,sQuery(id+"F3.wireOp",EDGE,"E5.14.0.0"),sQuery(id+"F3.wireOp",EDGE,"E5.14.0.1")])]})});var subQ3=makeQuery(id+"F5.imprint","INTERSECT",VERTEX,{"derivedFrom":[subQ2,subQ0]});Q14=makeQuery(id+"F5.imprint","IMPRINT",FACE,{"disambiguationData":[TD([[makeQuery(id+"F5.imprint","IMPRINT",EDGE,{"disambiguationData":[TD([[subQ3,-1.0]])],"derivedFrom":subQ0}),1.0]])]});}
            var Q15;
            {var subQ0=sQuery(id+"F5.wireOp",EDGE,"E13.left");var subQ1=sQuery(id+"F3.wireOp",EDGE,"E5.13.0.1");var subQ2=sQuery(id+"F0.wireOp",EDGE,"E0.left");var subQ3=makeQuery(id+"FlHhq8AFgQTEit1_1.boolean.opBoolean","COPY",EDGE,{"derivedFrom":makeQuery(id+"FlHhq8AFgQTEit1_1.opExtrude","SWEPT_EDGE",EDGE,{"disambiguationData":[OSD([subQ2,subQ1,sQuery(id+"F3.wireOp",EDGE,"E5.13.0.2")])]})});var subQ4=makeQuery(id+"F5.imprint","INTERSECT",VERTEX,{"derivedFrom":[subQ3,subQ0]});Q15=makeQuery(id+"F5.imprint","IMPRINT",FACE,{"disambiguationData":[TD([[makeQuery(id+"F5.imprint","IMPRINT",EDGE,{"disambiguationData":[TD([[subQ4,-1.0]])],"derivedFrom":subQ0}),1.0]])]});}
            var Q16;
            {var subQ0=sQuery(id+"F5.wireOp",EDGE,"E13.left");var subQ1=sQuery(id+"F0.wireOp",EDGE,"E0.left");var subQ2=makeQuery(id+"FlHhq8AFgQTEit1_1.boolean.opBoolean","COPY",EDGE,{"derivedFrom":makeQuery(id+"FlHhq8AFgQTEit1_1.opExtrude","SWEPT_EDGE",EDGE,{"disambiguationData":[OSD([subQ1,sQuery(id+"F3.wireOp",EDGE,"E5.16.0.0"),sQuery(id+"F3.wireOp",EDGE,"E5.16.0.1")])]})});var subQ3=makeQuery(id+"F5.imprint","INTERSECT",VERTEX,{"derivedFrom":[subQ2,subQ0]});Q16=makeQuery(id+"F5.imprint","IMPRINT",FACE,{"disambiguationData":[TD([[makeQuery(id+"F5.imprint","IMPRINT",EDGE,{"disambiguationData":[TD([[subQ3,-1.0]])],"derivedFrom":subQ0}),1.0]])]});}
            var Q17;
            {var subQ0=sQuery(id+"F5.wireOp",EDGE,"E13.left");var subQ1=sQuery(id+"F0.wireOp",EDGE,"E0.left");var subQ2=makeQuery(id+"FlHhq8AFgQTEit1_1.boolean.opBoolean","COPY",EDGE,{"derivedFrom":makeQuery(id+"FlHhq8AFgQTEit1_1.opExtrude","SWEPT_EDGE",EDGE,{"disambiguationData":[OSD([subQ1,sQuery(id+"F3.wireOp",EDGE,"E5.15.0.0"),sQuery(id+"F3.wireOp",EDGE,"E5.15.0.1")])]})});var subQ3=makeQuery(id+"F5.imprint","INTERSECT",VERTEX,{"derivedFrom":[subQ2,subQ0]});Q17=makeQuery(id+"F5.imprint","IMPRINT",FACE,{"disambiguationData":[TD([[makeQuery(id+"F5.imprint","IMPRINT",EDGE,{"disambiguationData":[TD([[subQ3,-1.0]])],"derivedFrom":subQ0}),1.0]])]});}
            var Q18;
            {var subQ0=sQuery(id+"F5.wireOp",EDGE,"E16.left");var subQ1=sQuery(id+"F3.wireOp",EDGE,"E5.14.0.1");var subQ2=sQuery(id+"F0.wireOp",EDGE,"E0.left");var subQ3=makeQuery(id+"FlHhq8AFgQTEit1_1.boolean.opBoolean","COPY",EDGE,{"derivedFrom":makeQuery(id+"FlHhq8AFgQTEit1_1.opExtrude","SWEPT_EDGE",EDGE,{"disambiguationData":[OSD([subQ2,sQuery(id+"F3.wireOp",EDGE,"E5.14.0.0"),subQ1])]})});var subQ4=makeQuery(id+"F5.imprint","INTERSECT",VERTEX,{"derivedFrom":[subQ3,subQ0]});Q18=makeQuery(id+"F5.imprint","IMPRINT",FACE,{"disambiguationData":[TD([[makeQuery(id+"F5.imprint","IMPRINT",EDGE,{"disambiguationData":[TD([[subQ4,1.0]])],"derivedFrom":subQ0}),-1.0]])]});}
            var Q19;
            {var subQ0=sQuery(id+"F5.wireOp",EDGE,"E16.left");var subQ1=sQuery(id+"F0.wireOp",EDGE,"E0.left");var subQ2=makeQuery(id+"FlHhq8AFgQTEit1_1.boolean.opBoolean","COPY",EDGE,{"derivedFrom":makeQuery(id+"FlHhq8AFgQTEit1_1.opExtrude","SWEPT_EDGE",EDGE,{"disambiguationData":[OSD([subQ1,sQuery(id+"F3.wireOp",EDGE,"E5.13.0.1"),sQuery(id+"F3.wireOp",EDGE,"E5.13.0.2")])]})});var subQ3=makeQuery(id+"F5.imprint","INTERSECT",VERTEX,{"derivedFrom":[subQ2,subQ0]});Q19=makeQuery(id+"F5.imprint","IMPRINT",FACE,{"disambiguationData":[TD([[makeQuery(id+"F5.imprint","IMPRINT",EDGE,{"disambiguationData":[TD([[subQ3,1.0]])],"derivedFrom":subQ0}),-1.0]])]});}
            var Q20;
            {var subQ3=sQuery(id+"F5.wireOp",EDGE,"E18.top");var subQ5=sQuery(id+"F5.wireOp",EDGE,"E16.right");var subQ6=makeQuery(id+"F5.imprint","INTERSECT",VERTEX,{"derivedFrom":[subQ5,subQ3]});Q20=makeQuery(id+"F5.imprint","IMPRINT",FACE,{"disambiguationData":[TD([[makeQuery(id+"F5.imprint","IMPRINT",EDGE,{"disambiguationData":[TD([[subQ6,1.0]])],"derivedFrom":subQ3}),-1.0]])]});}
            var Q21;
            {var subQ0=sQuery(id+"F5.wireOp",EDGE,"E16.left");var subQ1=sQuery(id+"F0.wireOp",EDGE,"E0.left");var subQ2=makeQuery(id+"FlHhq8AFgQTEit1_1.boolean.opBoolean","COPY",EDGE,{"derivedFrom":makeQuery(id+"FlHhq8AFgQTEit1_1.opExtrude","SWEPT_EDGE",EDGE,{"disambiguationData":[OSD([subQ1,sQuery(id+"F3.wireOp",EDGE,"E5.12.0.1"),sQuery(id+"F3.wireOp",EDGE,"E5.12.0.2")])]})});var subQ3=makeQuery(id+"F5.imprint","INTERSECT",VERTEX,{"derivedFrom":[subQ2,subQ0]});Q21=makeQuery(id+"F5.imprint","IMPRINT",FACE,{"disambiguationData":[TD([[makeQuery(id+"F5.imprint","IMPRINT",EDGE,{"disambiguationData":[TD([[subQ3,1.0]])],"derivedFrom":subQ0}),-1.0]])]});}
            var Q22;
            {var subQ0=sQuery(id+"F5.wireOp",EDGE,"E16.left");var subQ1=sQuery(id+"F0.wireOp",EDGE,"E0.left");var subQ2=makeQuery(id+"FlHhq8AFgQTEit1_1.boolean.opBoolean","COPY",EDGE,{"derivedFrom":makeQuery(id+"FlHhq8AFgQTEit1_1.opExtrude","SWEPT_EDGE",EDGE,{"disambiguationData":[OSD([subQ1,sQuery(id+"F3.wireOp",EDGE,"E5.16.0.1"),sQuery(id+"F3.wireOp",EDGE,"E5.16.0.2")])]})});var subQ3=makeQuery(id+"F5.imprint","INTERSECT",VERTEX,{"derivedFrom":[subQ2,subQ0]});Q22=makeQuery(id+"F5.imprint","IMPRINT",FACE,{"disambiguationData":[TD([[makeQuery(id+"F5.imprint","IMPRINT",EDGE,{"disambiguationData":[TD([[subQ3,1.0]])],"derivedFrom":subQ0}),-1.0]])]});}
            var Q23;
            {var subQ0=sQuery(id+"F5.wireOp",EDGE,"E16.left");var subQ1=sQuery(id+"F3.wireOp",EDGE,"E5.16.0.1");var subQ2=sQuery(id+"F0.wireOp",EDGE,"E0.left");var subQ3=makeQuery(id+"FlHhq8AFgQTEit1_1.boolean.opBoolean","COPY",EDGE,{"derivedFrom":makeQuery(id+"FlHhq8AFgQTEit1_1.opExtrude","SWEPT_EDGE",EDGE,{"disambiguationData":[OSD([subQ2,sQuery(id+"F3.wireOp",EDGE,"E5.16.0.0"),subQ1])]})});var subQ4=makeQuery(id+"F5.imprint","INTERSECT",VERTEX,{"derivedFrom":[subQ3,subQ0]});Q23=makeQuery(id+"F5.imprint","IMPRINT",FACE,{"disambiguationData":[TD([[makeQuery(id+"F5.imprint","IMPRINT",EDGE,{"disambiguationData":[TD([[subQ4,1.0]])],"derivedFrom":subQ0}),-1.0]])]});}
            var Q24;
            {var subQ0=sQuery(id+"F5.wireOp",EDGE,"E16.left");var subQ1=sQuery(id+"F3.wireOp",EDGE,"E5.13.0.1");var subQ2=sQuery(id+"F0.wireOp",EDGE,"E0.left");var subQ3=makeQuery(id+"FlHhq8AFgQTEit1_1.boolean.opBoolean","COPY",EDGE,{"derivedFrom":makeQuery(id+"FlHhq8AFgQTEit1_1.opExtrude","SWEPT_EDGE",EDGE,{"disambiguationData":[OSD([subQ2,sQuery(id+"F3.wireOp",EDGE,"E5.13.0.0"),subQ1])]})});var subQ4=makeQuery(id+"F5.imprint","INTERSECT",VERTEX,{"derivedFrom":[subQ3,subQ0]});Q24=makeQuery(id+"F5.imprint","IMPRINT",FACE,{"disambiguationData":[TD([[makeQuery(id+"F5.imprint","IMPRINT",EDGE,{"disambiguationData":[TD([[subQ4,1.0]])],"derivedFrom":subQ0}),-1.0]])]});}
            var Q25;
            {var subQ0=sQuery(id+"F5.wireOp",EDGE,"E16.left");var subQ1=sQuery(id+"F3.wireOp",EDGE,"E5.12.0.1");var subQ2=sQuery(id+"F0.wireOp",EDGE,"E0.left");var subQ3=makeQuery(id+"FlHhq8AFgQTEit1_1.boolean.opBoolean","COPY",EDGE,{"derivedFrom":makeQuery(id+"FlHhq8AFgQTEit1_1.opExtrude","SWEPT_EDGE",EDGE,{"disambiguationData":[OSD([subQ2,sQuery(id+"F3.wireOp",EDGE,"E5.12.0.0"),subQ1])]})});var subQ4=makeQuery(id+"F5.imprint","INTERSECT",VERTEX,{"derivedFrom":[subQ3,subQ0]});Q25=makeQuery(id+"F5.imprint","IMPRINT",FACE,{"disambiguationData":[TD([[makeQuery(id+"F5.imprint","IMPRINT",EDGE,{"disambiguationData":[TD([[subQ4,1.0]])],"derivedFrom":subQ0}),-1.0]])]});}
            var Q26;
            {var subQ0=sQuery(id+"F5.wireOp",EDGE,"E16.left");var subQ1=sQuery(id+"F0.wireOp",EDGE,"E0.left");var subQ2=makeQuery(id+"FlHhq8AFgQTEit1_1.boolean.opBoolean","COPY",EDGE,{"derivedFrom":makeQuery(id+"FlHhq8AFgQTEit1_1.opExtrude","SWEPT_EDGE",EDGE,{"disambiguationData":[OSD([subQ1,sQuery(id+"F3.wireOp",EDGE,"E5.15.0.1"),sQuery(id+"F3.wireOp",EDGE,"E5.15.0.2")])]})});var subQ3=makeQuery(id+"F5.imprint","INTERSECT",VERTEX,{"derivedFrom":[subQ2,subQ0]});Q26=makeQuery(id+"F5.imprint","IMPRINT",FACE,{"disambiguationData":[TD([[makeQuery(id+"F5.imprint","IMPRINT",EDGE,{"disambiguationData":[TD([[subQ3,1.0]])],"derivedFrom":subQ0}),-1.0]])]});}
            var Q27;
            {var subQ0=sQuery(id+"F5.wireOp",EDGE,"E16.left");var subQ1=sQuery(id+"F3.wireOp",EDGE,"E5.17.0.1");var subQ2=sQuery(id+"F0.wireOp",EDGE,"E0.left");var subQ3=makeQuery(id+"FlHhq8AFgQTEit1_1.boolean.opBoolean","COPY",EDGE,{"derivedFrom":makeQuery(id+"FlHhq8AFgQTEit1_1.opExtrude","SWEPT_EDGE",EDGE,{"disambiguationData":[OSD([subQ2,sQuery(id+"F3.wireOp",EDGE,"E5.17.0.0"),subQ1])]})});var subQ4=makeQuery(id+"F5.imprint","INTERSECT",VERTEX,{"derivedFrom":[subQ3,subQ0]});Q27=makeQuery(id+"F5.imprint","IMPRINT",FACE,{"disambiguationData":[TD([[makeQuery(id+"F5.imprint","IMPRINT",EDGE,{"disambiguationData":[TD([[subQ4,1.0]])],"derivedFrom":subQ0}),-1.0]])]});}
            var Q28;
            {var subQ0=sQuery(id+"F5.wireOp",EDGE,"E16.left");var subQ1=sQuery(id+"F0.wireOp",EDGE,"E0.left");var subQ2=makeQuery(id+"FlHhq8AFgQTEit1_1.boolean.opBoolean","COPY",EDGE,{"derivedFrom":makeQuery(id+"FlHhq8AFgQTEit1_1.opExtrude","SWEPT_EDGE",EDGE,{"disambiguationData":[OSD([subQ1,sQuery(id+"F3.wireOp",EDGE,"E5.14.0.1"),sQuery(id+"F3.wireOp",EDGE,"E5.14.0.2")])]})});var subQ3=makeQuery(id+"F5.imprint","INTERSECT",VERTEX,{"derivedFrom":[subQ2,subQ0]});Q28=makeQuery(id+"F5.imprint","IMPRINT",FACE,{"disambiguationData":[TD([[makeQuery(id+"F5.imprint","IMPRINT",EDGE,{"disambiguationData":[TD([[subQ3,1.0]])],"derivedFrom":subQ0}),-1.0]])]});}
            var Q29;
            {var subQ0=sQuery(id+"F5.wireOp",EDGE,"E16.left");var subQ1=sQuery(id+"F3.wireOp",EDGE,"E5.15.0.1");var subQ2=sQuery(id+"F0.wireOp",EDGE,"E0.left");var subQ3=makeQuery(id+"FlHhq8AFgQTEit1_1.boolean.opBoolean","COPY",EDGE,{"derivedFrom":makeQuery(id+"FlHhq8AFgQTEit1_1.opExtrude","SWEPT_EDGE",EDGE,{"disambiguationData":[OSD([subQ2,sQuery(id+"F3.wireOp",EDGE,"E5.15.0.0"),subQ1])]})});var subQ4=makeQuery(id+"F5.imprint","INTERSECT",VERTEX,{"derivedFrom":[subQ3,subQ0]});Q29=makeQuery(id+"F5.imprint","IMPRINT",FACE,{"disambiguationData":[TD([[makeQuery(id+"F5.imprint","IMPRINT",EDGE,{"disambiguationData":[TD([[subQ4,1.0]])],"derivedFrom":subQ0}),-1.0]])]});}
            var Q30;
            {var subQ0=sQuery(id+"F5.wireOp",EDGE,"E14.left");var subQ1=sQuery(id+"F0.wireOp",EDGE,"E0.left");var subQ2=makeQuery(id+"FlHhq8AFgQTEit1_1.boolean.opBoolean","COPY",EDGE,{"derivedFrom":makeQuery(id+"FlHhq8AFgQTEit1_1.opExtrude","SWEPT_EDGE",EDGE,{"disambiguationData":[OSD([subQ1,sQuery(id+"F3.wireOp",EDGE,"E5.17.0.0"),sQuery(id+"F3.wireOp",EDGE,"E5.17.0.1")])]})});var subQ3=makeQuery(id+"F5.imprint","INTERSECT",VERTEX,{"derivedFrom":[subQ2,subQ0]});Q30=makeQuery(id+"F5.imprint","IMPRINT",FACE,{"disambiguationData":[TD([[makeQuery(id+"F5.imprint","IMPRINT",EDGE,{"disambiguationData":[TD([[subQ3,-1.0]])],"derivedFrom":subQ0}),-1.0]])]});}
            var Q31;
            {var subQ0=sQuery(id+"F5.wireOp",EDGE,"E14.left");var subQ1=sQuery(id+"F3.wireOp",EDGE,"E5.17.0.1");var subQ2=sQuery(id+"F0.wireOp",EDGE,"E0.left");var subQ3=makeQuery(id+"FlHhq8AFgQTEit1_1.boolean.opBoolean","COPY",EDGE,{"derivedFrom":makeQuery(id+"FlHhq8AFgQTEit1_1.opExtrude","SWEPT_EDGE",EDGE,{"disambiguationData":[OSD([subQ2,subQ1,sQuery(id+"F3.wireOp",EDGE,"E5.17.0.2")])]})});var subQ4=makeQuery(id+"F5.imprint","INTERSECT",VERTEX,{"derivedFrom":[subQ3,subQ0]});Q31=makeQuery(id+"F5.imprint","IMPRINT",FACE,{"disambiguationData":[TD([[makeQuery(id+"F5.imprint","IMPRINT",EDGE,{"disambiguationData":[TD([[subQ4,-1.0]])],"derivedFrom":subQ0}),-1.0]])]});}
            var Q32;
            {var subQ0=sQuery(id+"F5.wireOp",EDGE,"E14.left");var subQ1=sQuery(id+"F0.wireOp",EDGE,"E0.left");var subQ2=makeQuery(id+"FlHhq8AFgQTEit1_1.boolean.opBoolean","COPY",EDGE,{"derivedFrom":makeQuery(id+"FlHhq8AFgQTEit1_1.opExtrude","SWEPT_EDGE",EDGE,{"disambiguationData":[OSD([subQ1,sQuery(id+"F3.wireOp",EDGE,"E5.14.0.0"),sQuery(id+"F3.wireOp",EDGE,"E5.14.0.1")])]})});var subQ3=makeQuery(id+"F5.imprint","INTERSECT",VERTEX,{"derivedFrom":[subQ2,subQ0]});Q32=makeQuery(id+"F5.imprint","IMPRINT",FACE,{"disambiguationData":[TD([[makeQuery(id+"F5.imprint","IMPRINT",EDGE,{"disambiguationData":[TD([[subQ3,-1.0]])],"derivedFrom":subQ0}),-1.0]])]});}
            var Q33;
            {var subQ0=sQuery(id+"F5.wireOp",EDGE,"E14.left");var subQ1=sQuery(id+"F3.wireOp",EDGE,"E5.14.0.1");var subQ2=sQuery(id+"F0.wireOp",EDGE,"E0.left");var subQ3=makeQuery(id+"FlHhq8AFgQTEit1_1.boolean.opBoolean","COPY",EDGE,{"derivedFrom":makeQuery(id+"FlHhq8AFgQTEit1_1.opExtrude","SWEPT_EDGE",EDGE,{"disambiguationData":[OSD([subQ2,subQ1,sQuery(id+"F3.wireOp",EDGE,"E5.14.0.2")])]})});var subQ4=makeQuery(id+"F5.imprint","INTERSECT",VERTEX,{"derivedFrom":[subQ3,subQ0]});Q33=makeQuery(id+"F5.imprint","IMPRINT",FACE,{"disambiguationData":[TD([[makeQuery(id+"F5.imprint","IMPRINT",EDGE,{"disambiguationData":[TD([[subQ4,-1.0]])],"derivedFrom":subQ0}),-1.0]])]});}
            var Q34;
            {var subQ0=sQuery(id+"F5.wireOp",EDGE,"E14.left");var subQ1=sQuery(id+"F0.wireOp",EDGE,"E0.left");var subQ2=makeQuery(id+"FlHhq8AFgQTEit1_1.boolean.opBoolean","COPY",EDGE,{"derivedFrom":makeQuery(id+"FlHhq8AFgQTEit1_1.opExtrude","SWEPT_EDGE",EDGE,{"disambiguationData":[OSD([subQ1,sQuery(id+"F3.wireOp",EDGE,"E5.13.0.0"),sQuery(id+"F3.wireOp",EDGE,"E5.13.0.1")])]})});var subQ3=makeQuery(id+"F5.imprint","INTERSECT",VERTEX,{"derivedFrom":[subQ2,subQ0]});Q34=makeQuery(id+"F5.imprint","IMPRINT",FACE,{"disambiguationData":[TD([[makeQuery(id+"F5.imprint","IMPRINT",EDGE,{"disambiguationData":[TD([[subQ3,-1.0]])],"derivedFrom":subQ0}),-1.0]])]});}
            var Q35;
            {var subQ0=sQuery(id+"F5.wireOp",EDGE,"E14.left");var subQ1=sQuery(id+"F3.wireOp",EDGE,"E5.16.0.1");var subQ2=sQuery(id+"F0.wireOp",EDGE,"E0.left");var subQ3=makeQuery(id+"FlHhq8AFgQTEit1_1.boolean.opBoolean","COPY",EDGE,{"derivedFrom":makeQuery(id+"FlHhq8AFgQTEit1_1.opExtrude","SWEPT_EDGE",EDGE,{"disambiguationData":[OSD([subQ2,subQ1,sQuery(id+"F3.wireOp",EDGE,"E5.16.0.2")])]})});var subQ4=makeQuery(id+"F5.imprint","INTERSECT",VERTEX,{"derivedFrom":[subQ3,subQ0]});Q35=makeQuery(id+"F5.imprint","IMPRINT",FACE,{"disambiguationData":[TD([[makeQuery(id+"F5.imprint","IMPRINT",EDGE,{"disambiguationData":[TD([[subQ4,-1.0]])],"derivedFrom":subQ0}),-1.0]])]});}
            var Q36;
            {var subQ0=sQuery(id+"F5.wireOp",EDGE,"E14.left");var subQ1=sQuery(id+"F0.wireOp",EDGE,"E0.left");var subQ2=makeQuery(id+"FlHhq8AFgQTEit1_1.boolean.opBoolean","COPY",EDGE,{"derivedFrom":makeQuery(id+"FlHhq8AFgQTEit1_1.opExtrude","SWEPT_EDGE",EDGE,{"disambiguationData":[OSD([subQ1,sQuery(id+"F3.wireOp",EDGE,"E5.15.0.0"),sQuery(id+"F3.wireOp",EDGE,"E5.15.0.1")])]})});var subQ3=makeQuery(id+"F5.imprint","INTERSECT",VERTEX,{"derivedFrom":[subQ2,subQ0]});Q36=makeQuery(id+"F5.imprint","IMPRINT",FACE,{"disambiguationData":[TD([[makeQuery(id+"F5.imprint","IMPRINT",EDGE,{"disambiguationData":[TD([[subQ3,-1.0]])],"derivedFrom":subQ0}),-1.0]])]});}
            var Q37;
            {var subQ0=sQuery(id+"F5.wireOp",EDGE,"E14.left");var subQ1=sQuery(id+"F3.wireOp",EDGE,"E5.12.0.1");var subQ2=sQuery(id+"F0.wireOp",EDGE,"E0.left");var subQ3=makeQuery(id+"FlHhq8AFgQTEit1_1.boolean.opBoolean","COPY",EDGE,{"derivedFrom":makeQuery(id+"FlHhq8AFgQTEit1_1.opExtrude","SWEPT_EDGE",EDGE,{"disambiguationData":[OSD([subQ2,subQ1,sQuery(id+"F3.wireOp",EDGE,"E5.12.0.2")])]})});var subQ4=makeQuery(id+"F5.imprint","INTERSECT",VERTEX,{"derivedFrom":[subQ3,subQ0]});Q37=makeQuery(id+"F5.imprint","IMPRINT",FACE,{"disambiguationData":[TD([[makeQuery(id+"F5.imprint","IMPRINT",EDGE,{"disambiguationData":[TD([[subQ4,-1.0]])],"derivedFrom":subQ0}),-1.0]])]});}
            var Q38;
            {var subQ0=sQuery(id+"F5.wireOp",EDGE,"E14.left");var subQ1=sQuery(id+"F0.wireOp",EDGE,"E0.left");var subQ2=makeQuery(id+"FlHhq8AFgQTEit1_1.boolean.opBoolean","COPY",EDGE,{"derivedFrom":makeQuery(id+"FlHhq8AFgQTEit1_1.opExtrude","SWEPT_EDGE",EDGE,{"disambiguationData":[OSD([subQ1,sQuery(id+"F3.wireOp",EDGE,"E5.16.0.0"),sQuery(id+"F3.wireOp",EDGE,"E5.16.0.1")])]})});var subQ3=makeQuery(id+"F5.imprint","INTERSECT",VERTEX,{"derivedFrom":[subQ2,subQ0]});Q38=makeQuery(id+"F5.imprint","IMPRINT",FACE,{"disambiguationData":[TD([[makeQuery(id+"F5.imprint","IMPRINT",EDGE,{"disambiguationData":[TD([[subQ3,-1.0]])],"derivedFrom":subQ0}),-1.0]])]});}
            var Q39;
            {var subQ0=sQuery(id+"F5.wireOp",EDGE,"E17.top");var subQ5=sQuery(id+"F5.wireOp",EDGE,"E14.right");var subQ6=makeQuery(id+"F5.imprint","INTERSECT",VERTEX,{"derivedFrom":[subQ5,subQ0]});Q39=makeQuery(id+"F5.imprint","IMPRINT",FACE,{"disambiguationData":[TD([[makeQuery(id+"F5.imprint","IMPRINT",EDGE,{"disambiguationData":[TD([[subQ6,1.0]])],"derivedFrom":subQ0}),-1.0]])]});}
            var Q40;
            {var subQ0=sQuery(id+"F5.wireOp",EDGE,"E14.left");var subQ1=sQuery(id+"F3.wireOp",EDGE,"E5.15.0.1");var subQ2=sQuery(id+"F0.wireOp",EDGE,"E0.left");var subQ3=makeQuery(id+"FlHhq8AFgQTEit1_1.boolean.opBoolean","COPY",EDGE,{"derivedFrom":makeQuery(id+"FlHhq8AFgQTEit1_1.opExtrude","SWEPT_EDGE",EDGE,{"disambiguationData":[OSD([subQ2,subQ1,sQuery(id+"F3.wireOp",EDGE,"E5.15.0.2")])]})});var subQ4=makeQuery(id+"F5.imprint","INTERSECT",VERTEX,{"derivedFrom":[subQ3,subQ0]});Q40=makeQuery(id+"F5.imprint","IMPRINT",FACE,{"disambiguationData":[TD([[makeQuery(id+"F5.imprint","IMPRINT",EDGE,{"disambiguationData":[TD([[subQ4,-1.0]])],"derivedFrom":subQ0}),-1.0]])]});}
            var Q41;
            {var subQ0=sQuery(id+"F5.wireOp",EDGE,"E14.left");var subQ1=sQuery(id+"F3.wireOp",EDGE,"E5.13.0.1");var subQ2=sQuery(id+"F0.wireOp",EDGE,"E0.left");var subQ3=makeQuery(id+"FlHhq8AFgQTEit1_1.boolean.opBoolean","COPY",EDGE,{"derivedFrom":makeQuery(id+"FlHhq8AFgQTEit1_1.opExtrude","SWEPT_EDGE",EDGE,{"disambiguationData":[OSD([subQ2,subQ1,sQuery(id+"F3.wireOp",EDGE,"E5.13.0.2")])]})});var subQ4=makeQuery(id+"F5.imprint","INTERSECT",VERTEX,{"derivedFrom":[subQ3,subQ0]});Q41=makeQuery(id+"F5.imprint","IMPRINT",FACE,{"disambiguationData":[TD([[makeQuery(id+"F5.imprint","IMPRINT",EDGE,{"disambiguationData":[TD([[subQ4,-1.0]])],"derivedFrom":subQ0}),-1.0]])]});}
            var Q42;
            {var subQ0=sQuery(id+"F5.wireOp",EDGE,"E15.left");var subQ1=sQuery(id+"F0.wireOp",EDGE,"E0.left");var subQ2=makeQuery(id+"FlHhq8AFgQTEit1_1.boolean.opBoolean","COPY",EDGE,{"derivedFrom":makeQuery(id+"FlHhq8AFgQTEit1_1.opExtrude","SWEPT_EDGE",EDGE,{"disambiguationData":[OSD([subQ1,sQuery(id+"F3.wireOp",EDGE,"E5.12.0.1"),sQuery(id+"F3.wireOp",EDGE,"E5.12.0.2")])]})});var subQ3=makeQuery(id+"F5.imprint","INTERSECT",VERTEX,{"derivedFrom":[subQ2,subQ0]});Q42=makeQuery(id+"F5.imprint","IMPRINT",FACE,{"disambiguationData":[TD([[makeQuery(id+"F5.imprint","IMPRINT",EDGE,{"disambiguationData":[TD([[subQ3,1.0]])],"derivedFrom":subQ0}),1.0]])]});}
            var Q43;
            {var subQ0=sQuery(id+"F5.wireOp",EDGE,"E15.left");var subQ1=sQuery(id+"F0.wireOp",EDGE,"E0.left");var subQ2=makeQuery(id+"FlHhq8AFgQTEit1_1.boolean.opBoolean","COPY",EDGE,{"derivedFrom":makeQuery(id+"FlHhq8AFgQTEit1_1.opExtrude","SWEPT_EDGE",EDGE,{"disambiguationData":[OSD([subQ1,sQuery(id+"F3.wireOp",EDGE,"E5.14.0.1"),sQuery(id+"F3.wireOp",EDGE,"E5.14.0.2")])]})});var subQ3=makeQuery(id+"F5.imprint","INTERSECT",VERTEX,{"derivedFrom":[subQ2,subQ0]});Q43=makeQuery(id+"F5.imprint","IMPRINT",FACE,{"disambiguationData":[TD([[makeQuery(id+"F5.imprint","IMPRINT",EDGE,{"disambiguationData":[TD([[subQ3,1.0]])],"derivedFrom":subQ0}),1.0]])]});}
            var Q44;
            {var subQ0=sQuery(id+"F5.wireOp",EDGE,"E15.left");var subQ1=sQuery(id+"F3.wireOp",EDGE,"E5.17.0.1");var subQ2=sQuery(id+"F0.wireOp",EDGE,"E0.left");var subQ3=makeQuery(id+"FlHhq8AFgQTEit1_1.boolean.opBoolean","COPY",EDGE,{"derivedFrom":makeQuery(id+"FlHhq8AFgQTEit1_1.opExtrude","SWEPT_EDGE",EDGE,{"disambiguationData":[OSD([subQ2,sQuery(id+"F3.wireOp",EDGE,"E5.17.0.0"),subQ1])]})});var subQ4=makeQuery(id+"F5.imprint","INTERSECT",VERTEX,{"derivedFrom":[subQ3,subQ0]});Q44=makeQuery(id+"F5.imprint","IMPRINT",FACE,{"disambiguationData":[TD([[makeQuery(id+"F5.imprint","IMPRINT",EDGE,{"disambiguationData":[TD([[subQ4,1.0]])],"derivedFrom":subQ0}),1.0]])]});}
            var Q45;
            {var subQ0=sQuery(id+"F5.wireOp",EDGE,"E15.left");var subQ1=sQuery(id+"F0.wireOp",EDGE,"E0.left");var subQ2=makeQuery(id+"FlHhq8AFgQTEit1_1.boolean.opBoolean","COPY",EDGE,{"derivedFrom":makeQuery(id+"FlHhq8AFgQTEit1_1.opExtrude","SWEPT_EDGE",EDGE,{"disambiguationData":[OSD([subQ1,sQuery(id+"F3.wireOp",EDGE,"E5.13.0.1"),sQuery(id+"F3.wireOp",EDGE,"E5.13.0.2")])]})});var subQ3=makeQuery(id+"F5.imprint","INTERSECT",VERTEX,{"derivedFrom":[subQ2,subQ0]});Q45=makeQuery(id+"F5.imprint","IMPRINT",FACE,{"disambiguationData":[TD([[makeQuery(id+"F5.imprint","IMPRINT",EDGE,{"disambiguationData":[TD([[subQ3,1.0]])],"derivedFrom":subQ0}),1.0]])]});}
            var Q46;
            {var subQ0=sQuery(id+"F5.wireOp",EDGE,"E15.left");var subQ1=sQuery(id+"F0.wireOp",EDGE,"E0.left");var subQ2=makeQuery(id+"FlHhq8AFgQTEit1_1.boolean.opBoolean","COPY",EDGE,{"derivedFrom":makeQuery(id+"FlHhq8AFgQTEit1_1.opExtrude","SWEPT_EDGE",EDGE,{"disambiguationData":[OSD([subQ1,sQuery(id+"F3.wireOp",EDGE,"E5.16.0.1"),sQuery(id+"F3.wireOp",EDGE,"E5.16.0.2")])]})});var subQ3=makeQuery(id+"F5.imprint","INTERSECT",VERTEX,{"derivedFrom":[subQ2,subQ0]});Q46=makeQuery(id+"F5.imprint","IMPRINT",FACE,{"disambiguationData":[TD([[makeQuery(id+"F5.imprint","IMPRINT",EDGE,{"disambiguationData":[TD([[subQ3,1.0]])],"derivedFrom":subQ0}),1.0]])]});}
            var Q47;
            {var subQ0=sQuery(id+"F5.wireOp",EDGE,"E15.left");var subQ1=sQuery(id+"F0.wireOp",EDGE,"E0.left");var subQ2=makeQuery(id+"FlHhq8AFgQTEit1_1.boolean.opBoolean","COPY",EDGE,{"derivedFrom":makeQuery(id+"FlHhq8AFgQTEit1_1.opExtrude","SWEPT_EDGE",EDGE,{"disambiguationData":[OSD([subQ1,sQuery(id+"F3.wireOp",EDGE,"E5.15.0.1"),sQuery(id+"F3.wireOp",EDGE,"E5.15.0.2")])]})});var subQ3=makeQuery(id+"F5.imprint","INTERSECT",VERTEX,{"derivedFrom":[subQ2,subQ0]});Q47=makeQuery(id+"F5.imprint","IMPRINT",FACE,{"disambiguationData":[TD([[makeQuery(id+"F5.imprint","IMPRINT",EDGE,{"disambiguationData":[TD([[subQ3,1.0]])],"derivedFrom":subQ0}),1.0]])]});}
            var Q48;
            {var subQ3=sQuery(id+"F5.wireOp",EDGE,"E17.top");var subQ5=sQuery(id+"F5.wireOp",EDGE,"E15.right");var subQ6=makeQuery(id+"F5.imprint","INTERSECT",VERTEX,{"derivedFrom":[subQ5,subQ3]});Q48=makeQuery(id+"F5.imprint","IMPRINT",FACE,{"disambiguationData":[TD([[makeQuery(id+"F5.imprint","IMPRINT",EDGE,{"disambiguationData":[TD([[subQ6,-1.0]])],"derivedFrom":subQ3}),-1.0]])]});}
            var Q49;
            {var subQ0=sQuery(id+"F5.wireOp",EDGE,"E15.left");var subQ1=sQuery(id+"F3.wireOp",EDGE,"E5.15.0.1");var subQ2=sQuery(id+"F0.wireOp",EDGE,"E0.left");var subQ3=makeQuery(id+"FlHhq8AFgQTEit1_1.boolean.opBoolean","COPY",EDGE,{"derivedFrom":makeQuery(id+"FlHhq8AFgQTEit1_1.opExtrude","SWEPT_EDGE",EDGE,{"disambiguationData":[OSD([subQ2,sQuery(id+"F3.wireOp",EDGE,"E5.15.0.0"),subQ1])]})});var subQ4=makeQuery(id+"F5.imprint","INTERSECT",VERTEX,{"derivedFrom":[subQ3,subQ0]});Q49=makeQuery(id+"F5.imprint","IMPRINT",FACE,{"disambiguationData":[TD([[makeQuery(id+"F5.imprint","IMPRINT",EDGE,{"disambiguationData":[TD([[subQ4,1.0]])],"derivedFrom":subQ0}),1.0]])]});}
            var Q50;
            {var subQ0=sQuery(id+"F5.wireOp",EDGE,"E15.left");var subQ1=sQuery(id+"F3.wireOp",EDGE,"E5.14.0.1");var subQ2=sQuery(id+"F0.wireOp",EDGE,"E0.left");var subQ3=makeQuery(id+"FlHhq8AFgQTEit1_1.boolean.opBoolean","COPY",EDGE,{"derivedFrom":makeQuery(id+"FlHhq8AFgQTEit1_1.opExtrude","SWEPT_EDGE",EDGE,{"disambiguationData":[OSD([subQ2,sQuery(id+"F3.wireOp",EDGE,"E5.14.0.0"),subQ1])]})});var subQ4=makeQuery(id+"F5.imprint","INTERSECT",VERTEX,{"derivedFrom":[subQ3,subQ0]});Q50=makeQuery(id+"F5.imprint","IMPRINT",FACE,{"disambiguationData":[TD([[makeQuery(id+"F5.imprint","IMPRINT",EDGE,{"disambiguationData":[TD([[subQ4,1.0]])],"derivedFrom":subQ0}),1.0]])]});}
            var Q51;
            {var subQ0=sQuery(id+"F5.wireOp",EDGE,"E15.left");var subQ1=sQuery(id+"F3.wireOp",EDGE,"E5.16.0.1");var subQ2=sQuery(id+"F0.wireOp",EDGE,"E0.left");var subQ3=makeQuery(id+"FlHhq8AFgQTEit1_1.boolean.opBoolean","COPY",EDGE,{"derivedFrom":makeQuery(id+"FlHhq8AFgQTEit1_1.opExtrude","SWEPT_EDGE",EDGE,{"disambiguationData":[OSD([subQ2,sQuery(id+"F3.wireOp",EDGE,"E5.16.0.0"),subQ1])]})});var subQ4=makeQuery(id+"F5.imprint","INTERSECT",VERTEX,{"derivedFrom":[subQ3,subQ0]});Q51=makeQuery(id+"F5.imprint","IMPRINT",FACE,{"disambiguationData":[TD([[makeQuery(id+"F5.imprint","IMPRINT",EDGE,{"disambiguationData":[TD([[subQ4,1.0]])],"derivedFrom":subQ0}),1.0]])]});}
            var Q52;
            {var subQ0=sQuery(id+"F5.wireOp",EDGE,"E15.left");var subQ1=sQuery(id+"F3.wireOp",EDGE,"E5.12.0.1");var subQ2=sQuery(id+"F0.wireOp",EDGE,"E0.left");var subQ3=makeQuery(id+"FlHhq8AFgQTEit1_1.boolean.opBoolean","COPY",EDGE,{"derivedFrom":makeQuery(id+"FlHhq8AFgQTEit1_1.opExtrude","SWEPT_EDGE",EDGE,{"disambiguationData":[OSD([subQ2,sQuery(id+"F3.wireOp",EDGE,"E5.12.0.0"),subQ1])]})});var subQ4=makeQuery(id+"F5.imprint","INTERSECT",VERTEX,{"derivedFrom":[subQ3,subQ0]});Q52=makeQuery(id+"F5.imprint","IMPRINT",FACE,{"disambiguationData":[TD([[makeQuery(id+"F5.imprint","IMPRINT",EDGE,{"disambiguationData":[TD([[subQ4,1.0]])],"derivedFrom":subQ0}),1.0]])]});}
            var Q53;
            {var subQ0=sQuery(id+"F5.wireOp",EDGE,"E15.left");var subQ1=sQuery(id+"F3.wireOp",EDGE,"E5.13.0.1");var subQ2=sQuery(id+"F0.wireOp",EDGE,"E0.left");var subQ3=makeQuery(id+"FlHhq8AFgQTEit1_1.boolean.opBoolean","COPY",EDGE,{"derivedFrom":makeQuery(id+"FlHhq8AFgQTEit1_1.opExtrude","SWEPT_EDGE",EDGE,{"disambiguationData":[OSD([subQ2,sQuery(id+"F3.wireOp",EDGE,"E5.13.0.0"),subQ1])]})});var subQ4=makeQuery(id+"F5.imprint","INTERSECT",VERTEX,{"derivedFrom":[subQ3,subQ0]});Q53=makeQuery(id+"F5.imprint","IMPRINT",FACE,{"disambiguationData":[TD([[makeQuery(id+"F5.imprint","IMPRINT",EDGE,{"disambiguationData":[TD([[subQ4,1.0]])],"derivedFrom":subQ0}),1.0]])]});}
            var Q54;
            {var subQ0=sQuery(id+"F5.wireOp",EDGE,"E28.left");var subQ1=sQuery(id+"F3.wireOp",EDGE,"E5.16.0.1");var subQ2=sQuery(id+"F0.wireOp",EDGE,"E0.left");var subQ3=makeQuery(id+"FlHhq8AFgQTEit1_1.boolean.opBoolean","COPY",EDGE,{"derivedFrom":makeQuery(id+"FlHhq8AFgQTEit1_1.opExtrude","SWEPT_EDGE",EDGE,{"disambiguationData":[OSD([subQ2,sQuery(id+"F3.wireOp",EDGE,"E5.16.0.0"),subQ1])]})});var subQ4=makeQuery(id+"F5.imprint","INTERSECT",VERTEX,{"derivedFrom":[subQ3,subQ0]});Q54=makeQuery(id+"F5.imprint","IMPRINT",FACE,{"disambiguationData":[TD([[makeQuery(id+"F5.imprint","IMPRINT",EDGE,{"disambiguationData":[TD([[subQ4,-1.0]])],"derivedFrom":subQ0}),1.0]])]});}
            var Q55;
            {var subQ0=sQuery(id+"F5.wireOp",EDGE,"E28.left");var subQ1=sQuery(id+"F3.wireOp",EDGE,"E5.17.0.1");var subQ2=sQuery(id+"F0.wireOp",EDGE,"E0.left");var subQ3=makeQuery(id+"FlHhq8AFgQTEit1_1.boolean.opBoolean","COPY",EDGE,{"derivedFrom":makeQuery(id+"FlHhq8AFgQTEit1_1.opExtrude","SWEPT_EDGE",EDGE,{"disambiguationData":[OSD([subQ2,sQuery(id+"F3.wireOp",EDGE,"E5.17.0.0"),subQ1])]})});var subQ4=makeQuery(id+"F5.imprint","INTERSECT",VERTEX,{"derivedFrom":[subQ3,subQ0]});Q55=makeQuery(id+"F5.imprint","IMPRINT",FACE,{"disambiguationData":[TD([[makeQuery(id+"F5.imprint","IMPRINT",EDGE,{"disambiguationData":[TD([[subQ4,-1.0]])],"derivedFrom":subQ0}),1.0]])]});}
            var Q56;
            {var subQ0=sQuery(id+"F5.wireOp",EDGE,"E28.left");var subQ1=sQuery(id+"F0.wireOp",EDGE,"E0.left");var subQ2=makeQuery(id+"FlHhq8AFgQTEit1_1.boolean.opBoolean","COPY",EDGE,{"derivedFrom":makeQuery(id+"FlHhq8AFgQTEit1_1.opExtrude","SWEPT_EDGE",EDGE,{"disambiguationData":[OSD([subQ1,sQuery(id+"F3.wireOp",EDGE,"E5.12.0.1"),sQuery(id+"F3.wireOp",EDGE,"E5.12.0.2")])]})});var subQ3=makeQuery(id+"F5.imprint","INTERSECT",VERTEX,{"derivedFrom":[subQ2,subQ0]});Q56=makeQuery(id+"F5.imprint","IMPRINT",FACE,{"disambiguationData":[TD([[makeQuery(id+"F5.imprint","IMPRINT",EDGE,{"disambiguationData":[TD([[subQ3,-1.0]])],"derivedFrom":subQ0}),1.0]])]});}
            var Q57;
            {var subQ0=sQuery(id+"F5.wireOp",EDGE,"E28.top");Q57=makeQuery(id+"F5.imprint","IMPRINT",FACE,{"disambiguationData":[TD([[makeQuery(id+"F5.imprint","IMPRINT",EDGE,{"derivedFrom":subQ0}),1.0]])]});}
            var Q58;
            {var subQ0=sQuery(id+"F5.wireOp",EDGE,"E28.bottom");Q58=makeQuery(id+"F5.imprint","IMPRINT",FACE,{"disambiguationData":[TD([[makeQuery(id+"F5.imprint","IMPRINT",EDGE,{"derivedFrom":subQ0}),-1.0]])]});}
            var Q59;
            {var subQ0=sQuery(id+"F5.wireOp",EDGE,"E28.left");var subQ1=sQuery(id+"F3.wireOp",EDGE,"E5.15.0.1");var subQ2=sQuery(id+"F0.wireOp",EDGE,"E0.left");var subQ3=makeQuery(id+"FlHhq8AFgQTEit1_1.boolean.opBoolean","COPY",EDGE,{"derivedFrom":makeQuery(id+"FlHhq8AFgQTEit1_1.opExtrude","SWEPT_EDGE",EDGE,{"disambiguationData":[OSD([subQ2,sQuery(id+"F3.wireOp",EDGE,"E5.15.0.0"),subQ1])]})});var subQ4=makeQuery(id+"F5.imprint","INTERSECT",VERTEX,{"derivedFrom":[subQ3,subQ0]});Q59=makeQuery(id+"F5.imprint","IMPRINT",FACE,{"disambiguationData":[TD([[makeQuery(id+"F5.imprint","IMPRINT",EDGE,{"disambiguationData":[TD([[subQ4,-1.0]])],"derivedFrom":subQ0}),1.0]])]});}
            var Q60;
            {var subQ0=sQuery(id+"F5.wireOp",EDGE,"E28.left");var subQ1=sQuery(id+"F3.wireOp",EDGE,"E5.14.0.1");var subQ2=sQuery(id+"F0.wireOp",EDGE,"E0.left");var subQ3=makeQuery(id+"FlHhq8AFgQTEit1_1.boolean.opBoolean","COPY",EDGE,{"derivedFrom":makeQuery(id+"FlHhq8AFgQTEit1_1.opExtrude","SWEPT_EDGE",EDGE,{"disambiguationData":[OSD([subQ2,sQuery(id+"F3.wireOp",EDGE,"E5.14.0.0"),subQ1])]})});var subQ4=makeQuery(id+"F5.imprint","INTERSECT",VERTEX,{"derivedFrom":[subQ3,subQ0]});Q60=makeQuery(id+"F5.imprint","IMPRINT",FACE,{"disambiguationData":[TD([[makeQuery(id+"F5.imprint","IMPRINT",EDGE,{"disambiguationData":[TD([[subQ4,-1.0]])],"derivedFrom":subQ0}),1.0]])]});}
            var Q61;
            {var subQ0=sQuery(id+"F5.wireOp",EDGE,"E28.left");var subQ1=sQuery(id+"F0.wireOp",EDGE,"E0.left");var subQ2=makeQuery(id+"FlHhq8AFgQTEit1_1.boolean.opBoolean","COPY",EDGE,{"derivedFrom":makeQuery(id+"FlHhq8AFgQTEit1_1.opExtrude","SWEPT_EDGE",EDGE,{"disambiguationData":[OSD([subQ1,sQuery(id+"F3.wireOp",EDGE,"E5.13.0.1"),sQuery(id+"F3.wireOp",EDGE,"E5.13.0.2")])]})});var subQ3=makeQuery(id+"F5.imprint","INTERSECT",VERTEX,{"derivedFrom":[subQ2,subQ0]});Q61=makeQuery(id+"F5.imprint","IMPRINT",FACE,{"disambiguationData":[TD([[makeQuery(id+"F5.imprint","IMPRINT",EDGE,{"disambiguationData":[TD([[subQ3,-1.0]])],"derivedFrom":subQ0}),1.0]])]});}
            var Q62;
            {var subQ0=sQuery(id+"F5.wireOp",EDGE,"E28.left");var subQ1=sQuery(id+"F3.wireOp",EDGE,"E5.13.0.1");var subQ2=sQuery(id+"F0.wireOp",EDGE,"E0.left");var subQ3=makeQuery(id+"FlHhq8AFgQTEit1_1.boolean.opBoolean","COPY",EDGE,{"derivedFrom":makeQuery(id+"FlHhq8AFgQTEit1_1.opExtrude","SWEPT_EDGE",EDGE,{"disambiguationData":[OSD([subQ2,sQuery(id+"F3.wireOp",EDGE,"E5.13.0.0"),subQ1])]})});var subQ4=makeQuery(id+"F5.imprint","INTERSECT",VERTEX,{"derivedFrom":[subQ3,subQ0]});Q62=makeQuery(id+"F5.imprint","IMPRINT",FACE,{"disambiguationData":[TD([[makeQuery(id+"F5.imprint","IMPRINT",EDGE,{"disambiguationData":[TD([[subQ4,-1.0]])],"derivedFrom":subQ0}),1.0]])]});}
            var Q63;
            {var subQ0=sQuery(id+"F5.wireOp",EDGE,"E28.left");var subQ1=sQuery(id+"F0.wireOp",EDGE,"E0.left");var subQ2=makeQuery(id+"FlHhq8AFgQTEit1_1.boolean.opBoolean","COPY",EDGE,{"derivedFrom":makeQuery(id+"FlHhq8AFgQTEit1_1.opExtrude","SWEPT_EDGE",EDGE,{"disambiguationData":[OSD([subQ1,sQuery(id+"F3.wireOp",EDGE,"E5.15.0.1"),sQuery(id+"F3.wireOp",EDGE,"E5.15.0.2")])]})});var subQ3=makeQuery(id+"F5.imprint","INTERSECT",VERTEX,{"derivedFrom":[subQ2,subQ0]});Q63=makeQuery(id+"F5.imprint","IMPRINT",FACE,{"disambiguationData":[TD([[makeQuery(id+"F5.imprint","IMPRINT",EDGE,{"disambiguationData":[TD([[subQ3,-1.0]])],"derivedFrom":subQ0}),1.0]])]});}
            var Q64;
            {var subQ0=sQuery(id+"F5.wireOp",EDGE,"E28.left");var subQ1=sQuery(id+"F0.wireOp",EDGE,"E0.left");var subQ2=makeQuery(id+"FlHhq8AFgQTEit1_1.boolean.opBoolean","COPY",EDGE,{"derivedFrom":makeQuery(id+"FlHhq8AFgQTEit1_1.opExtrude","SWEPT_EDGE",EDGE,{"disambiguationData":[OSD([subQ1,sQuery(id+"F3.wireOp",EDGE,"E5.16.0.1"),sQuery(id+"F3.wireOp",EDGE,"E5.16.0.2")])]})});var subQ3=makeQuery(id+"F5.imprint","INTERSECT",VERTEX,{"derivedFrom":[subQ2,subQ0]});Q64=makeQuery(id+"F5.imprint","IMPRINT",FACE,{"disambiguationData":[TD([[makeQuery(id+"F5.imprint","IMPRINT",EDGE,{"disambiguationData":[TD([[subQ3,-1.0]])],"derivedFrom":subQ0}),1.0]])]});}
            var Q65;
            {var subQ0=sQuery(id+"F5.wireOp",EDGE,"E28.left");var subQ1=sQuery(id+"F3.wireOp",EDGE,"E5.12.0.1");var subQ2=sQuery(id+"F0.wireOp",EDGE,"E0.left");var subQ3=makeQuery(id+"FlHhq8AFgQTEit1_1.boolean.opBoolean","COPY",EDGE,{"derivedFrom":makeQuery(id+"FlHhq8AFgQTEit1_1.opExtrude","SWEPT_EDGE",EDGE,{"disambiguationData":[OSD([subQ2,sQuery(id+"F3.wireOp",EDGE,"E5.12.0.0"),subQ1])]})});var subQ4=makeQuery(id+"F5.imprint","INTERSECT",VERTEX,{"derivedFrom":[subQ3,subQ0]});Q65=makeQuery(id+"F5.imprint","IMPRINT",FACE,{"disambiguationData":[TD([[makeQuery(id+"F5.imprint","IMPRINT",EDGE,{"disambiguationData":[TD([[subQ4,-1.0]])],"derivedFrom":subQ0}),1.0]])]});}
            var Q66;
            {var subQ0=sQuery(id+"F5.wireOp",EDGE,"E28.left");var subQ1=sQuery(id+"F0.wireOp",EDGE,"E0.left");var subQ2=makeQuery(id+"FlHhq8AFgQTEit1_1.boolean.opBoolean","COPY",EDGE,{"derivedFrom":makeQuery(id+"FlHhq8AFgQTEit1_1.opExtrude","SWEPT_EDGE",EDGE,{"disambiguationData":[OSD([subQ1,sQuery(id+"F3.wireOp",EDGE,"E5.14.0.1"),sQuery(id+"F3.wireOp",EDGE,"E5.14.0.2")])]})});var subQ3=makeQuery(id+"F5.imprint","INTERSECT",VERTEX,{"derivedFrom":[subQ2,subQ0]});Q66=makeQuery(id+"F5.imprint","IMPRINT",FACE,{"disambiguationData":[TD([[makeQuery(id+"F5.imprint","IMPRINT",EDGE,{"disambiguationData":[TD([[subQ3,-1.0]])],"derivedFrom":subQ0}),1.0]])]});}
            var Q67;
            {var subQ0=sQuery(id+"F5.wireOp",EDGE,"E29.left");var subQ1=sQuery(id+"F0.wireOp",EDGE,"E0.left");var subQ2=makeQuery(id+"FlHhq8AFgQTEit1_1.boolean.opBoolean","COPY",EDGE,{"derivedFrom":makeQuery(id+"FlHhq8AFgQTEit1_1.opExtrude","SWEPT_EDGE",EDGE,{"disambiguationData":[OSD([subQ1,sQuery(id+"F3.wireOp",EDGE,"E5.12.0.1"),sQuery(id+"F3.wireOp",EDGE,"E5.12.0.2")])]})});var subQ3=makeQuery(id+"F5.imprint","INTERSECT",VERTEX,{"derivedFrom":[subQ2,subQ0]});Q67=makeQuery(id+"F5.imprint","IMPRINT",FACE,{"disambiguationData":[TD([[makeQuery(id+"F5.imprint","IMPRINT",EDGE,{"disambiguationData":[TD([[subQ3,-1.0]])],"derivedFrom":subQ0}),1.0]])]});}
            var Q68;
            {var subQ0=sQuery(id+"F5.wireOp",EDGE,"E29.left");var subQ1=sQuery(id+"F0.wireOp",EDGE,"E0.left");var subQ2=makeQuery(id+"FlHhq8AFgQTEit1_1.boolean.opBoolean","COPY",EDGE,{"derivedFrom":makeQuery(id+"FlHhq8AFgQTEit1_1.opExtrude","SWEPT_EDGE",EDGE,{"disambiguationData":[OSD([subQ1,sQuery(id+"F3.wireOp",EDGE,"E5.14.0.1"),sQuery(id+"F3.wireOp",EDGE,"E5.14.0.2")])]})});var subQ3=makeQuery(id+"F5.imprint","INTERSECT",VERTEX,{"derivedFrom":[subQ2,subQ0]});Q68=makeQuery(id+"F5.imprint","IMPRINT",FACE,{"disambiguationData":[TD([[makeQuery(id+"F5.imprint","IMPRINT",EDGE,{"disambiguationData":[TD([[subQ3,-1.0]])],"derivedFrom":subQ0}),1.0]])]});}
            var Q69;
            {var subQ0=sQuery(id+"F5.wireOp",EDGE,"E29.left");var subQ1=sQuery(id+"F3.wireOp",EDGE,"E5.16.0.1");var subQ2=sQuery(id+"F0.wireOp",EDGE,"E0.left");var subQ3=makeQuery(id+"FlHhq8AFgQTEit1_1.boolean.opBoolean","COPY",EDGE,{"derivedFrom":makeQuery(id+"FlHhq8AFgQTEit1_1.opExtrude","SWEPT_EDGE",EDGE,{"disambiguationData":[OSD([subQ2,sQuery(id+"F3.wireOp",EDGE,"E5.16.0.0"),subQ1])]})});var subQ4=makeQuery(id+"F5.imprint","INTERSECT",VERTEX,{"derivedFrom":[subQ3,subQ0]});Q69=makeQuery(id+"F5.imprint","IMPRINT",FACE,{"disambiguationData":[TD([[makeQuery(id+"F5.imprint","IMPRINT",EDGE,{"disambiguationData":[TD([[subQ4,-1.0]])],"derivedFrom":subQ0}),1.0]])]});}
            var Q70;
            {var subQ0=sQuery(id+"F5.wireOp",EDGE,"E29.bottom");Q70=makeQuery(id+"F5.imprint","IMPRINT",FACE,{"disambiguationData":[TD([[makeQuery(id+"F5.imprint","IMPRINT",EDGE,{"derivedFrom":subQ0}),-1.0]])]});}
            var Q71;
            {var subQ0=sQuery(id+"F5.wireOp",EDGE,"E29.top");Q71=makeQuery(id+"F5.imprint","IMPRINT",FACE,{"disambiguationData":[TD([[makeQuery(id+"F5.imprint","IMPRINT",EDGE,{"derivedFrom":subQ0}),1.0]])]});}
            var Q72;
            {var subQ0=sQuery(id+"F5.wireOp",EDGE,"E29.left");var subQ1=sQuery(id+"F3.wireOp",EDGE,"E5.13.0.1");var subQ2=sQuery(id+"F0.wireOp",EDGE,"E0.left");var subQ3=makeQuery(id+"FlHhq8AFgQTEit1_1.boolean.opBoolean","COPY",EDGE,{"derivedFrom":makeQuery(id+"FlHhq8AFgQTEit1_1.opExtrude","SWEPT_EDGE",EDGE,{"disambiguationData":[OSD([subQ2,sQuery(id+"F3.wireOp",EDGE,"E5.13.0.0"),subQ1])]})});var subQ4=makeQuery(id+"F5.imprint","INTERSECT",VERTEX,{"derivedFrom":[subQ3,subQ0]});Q72=makeQuery(id+"F5.imprint","IMPRINT",FACE,{"disambiguationData":[TD([[makeQuery(id+"F5.imprint","IMPRINT",EDGE,{"disambiguationData":[TD([[subQ4,-1.0]])],"derivedFrom":subQ0}),1.0]])]});}
            var Q73;
            {var subQ0=sQuery(id+"F5.wireOp",EDGE,"E29.left");var subQ1=sQuery(id+"F3.wireOp",EDGE,"E5.12.0.1");var subQ2=sQuery(id+"F0.wireOp",EDGE,"E0.left");var subQ3=makeQuery(id+"FlHhq8AFgQTEit1_1.boolean.opBoolean","COPY",EDGE,{"derivedFrom":makeQuery(id+"FlHhq8AFgQTEit1_1.opExtrude","SWEPT_EDGE",EDGE,{"disambiguationData":[OSD([subQ2,sQuery(id+"F3.wireOp",EDGE,"E5.12.0.0"),subQ1])]})});var subQ4=makeQuery(id+"F5.imprint","INTERSECT",VERTEX,{"derivedFrom":[subQ3,subQ0]});Q73=makeQuery(id+"F5.imprint","IMPRINT",FACE,{"disambiguationData":[TD([[makeQuery(id+"F5.imprint","IMPRINT",EDGE,{"disambiguationData":[TD([[subQ4,-1.0]])],"derivedFrom":subQ0}),1.0]])]});}
            var Q74;
            {var subQ0=sQuery(id+"F5.wireOp",EDGE,"E29.left");var subQ1=sQuery(id+"F0.wireOp",EDGE,"E0.left");var subQ2=makeQuery(id+"FlHhq8AFgQTEit1_1.boolean.opBoolean","COPY",EDGE,{"derivedFrom":makeQuery(id+"FlHhq8AFgQTEit1_1.opExtrude","SWEPT_EDGE",EDGE,{"disambiguationData":[OSD([subQ1,sQuery(id+"F3.wireOp",EDGE,"E5.15.0.1"),sQuery(id+"F3.wireOp",EDGE,"E5.15.0.2")])]})});var subQ3=makeQuery(id+"F5.imprint","INTERSECT",VERTEX,{"derivedFrom":[subQ2,subQ0]});Q74=makeQuery(id+"F5.imprint","IMPRINT",FACE,{"disambiguationData":[TD([[makeQuery(id+"F5.imprint","IMPRINT",EDGE,{"disambiguationData":[TD([[subQ3,-1.0]])],"derivedFrom":subQ0}),1.0]])]});}
            var Q75;
            {var subQ0=sQuery(id+"F5.wireOp",EDGE,"E29.left");var subQ1=sQuery(id+"F3.wireOp",EDGE,"E5.14.0.1");var subQ2=sQuery(id+"F0.wireOp",EDGE,"E0.left");var subQ3=makeQuery(id+"FlHhq8AFgQTEit1_1.boolean.opBoolean","COPY",EDGE,{"derivedFrom":makeQuery(id+"FlHhq8AFgQTEit1_1.opExtrude","SWEPT_EDGE",EDGE,{"disambiguationData":[OSD([subQ2,sQuery(id+"F3.wireOp",EDGE,"E5.14.0.0"),subQ1])]})});var subQ4=makeQuery(id+"F5.imprint","INTERSECT",VERTEX,{"derivedFrom":[subQ3,subQ0]});Q75=makeQuery(id+"F5.imprint","IMPRINT",FACE,{"disambiguationData":[TD([[makeQuery(id+"F5.imprint","IMPRINT",EDGE,{"disambiguationData":[TD([[subQ4,-1.0]])],"derivedFrom":subQ0}),1.0]])]});}
            var Q76;
            {var subQ0=sQuery(id+"F5.wireOp",EDGE,"E29.left");var subQ1=sQuery(id+"F0.wireOp",EDGE,"E0.left");var subQ2=makeQuery(id+"FlHhq8AFgQTEit1_1.boolean.opBoolean","COPY",EDGE,{"derivedFrom":makeQuery(id+"FlHhq8AFgQTEit1_1.opExtrude","SWEPT_EDGE",EDGE,{"disambiguationData":[OSD([subQ1,sQuery(id+"F3.wireOp",EDGE,"E5.16.0.1"),sQuery(id+"F3.wireOp",EDGE,"E5.16.0.2")])]})});var subQ3=makeQuery(id+"F5.imprint","INTERSECT",VERTEX,{"derivedFrom":[subQ2,subQ0]});Q76=makeQuery(id+"F5.imprint","IMPRINT",FACE,{"disambiguationData":[TD([[makeQuery(id+"F5.imprint","IMPRINT",EDGE,{"disambiguationData":[TD([[subQ3,-1.0]])],"derivedFrom":subQ0}),1.0]])]});}
            var Q77;
            {var subQ0=sQuery(id+"F5.wireOp",EDGE,"E29.left");var subQ1=sQuery(id+"F0.wireOp",EDGE,"E0.left");var subQ2=makeQuery(id+"FlHhq8AFgQTEit1_1.boolean.opBoolean","COPY",EDGE,{"derivedFrom":makeQuery(id+"FlHhq8AFgQTEit1_1.opExtrude","SWEPT_EDGE",EDGE,{"disambiguationData":[OSD([subQ1,sQuery(id+"F3.wireOp",EDGE,"E5.13.0.1"),sQuery(id+"F3.wireOp",EDGE,"E5.13.0.2")])]})});var subQ3=makeQuery(id+"F5.imprint","INTERSECT",VERTEX,{"derivedFrom":[subQ2,subQ0]});Q77=makeQuery(id+"F5.imprint","IMPRINT",FACE,{"disambiguationData":[TD([[makeQuery(id+"F5.imprint","IMPRINT",EDGE,{"disambiguationData":[TD([[subQ3,-1.0]])],"derivedFrom":subQ0}),1.0]])]});}
            var Q78;
            {var subQ0=sQuery(id+"F5.wireOp",EDGE,"E29.left");var subQ1=sQuery(id+"F3.wireOp",EDGE,"E5.17.0.1");var subQ2=sQuery(id+"F0.wireOp",EDGE,"E0.left");var subQ3=makeQuery(id+"FlHhq8AFgQTEit1_1.boolean.opBoolean","COPY",EDGE,{"derivedFrom":makeQuery(id+"FlHhq8AFgQTEit1_1.opExtrude","SWEPT_EDGE",EDGE,{"disambiguationData":[OSD([subQ2,sQuery(id+"F3.wireOp",EDGE,"E5.17.0.0"),subQ1])]})});var subQ4=makeQuery(id+"F5.imprint","INTERSECT",VERTEX,{"derivedFrom":[subQ3,subQ0]});Q78=makeQuery(id+"F5.imprint","IMPRINT",FACE,{"disambiguationData":[TD([[makeQuery(id+"F5.imprint","IMPRINT",EDGE,{"disambiguationData":[TD([[subQ4,-1.0]])],"derivedFrom":subQ0}),1.0]])]});}
            var Q79;
            {var subQ0=sQuery(id+"F5.wireOp",EDGE,"E29.left");var subQ1=sQuery(id+"F3.wireOp",EDGE,"E5.15.0.1");var subQ2=sQuery(id+"F0.wireOp",EDGE,"E0.left");var subQ3=makeQuery(id+"FlHhq8AFgQTEit1_1.boolean.opBoolean","COPY",EDGE,{"derivedFrom":makeQuery(id+"FlHhq8AFgQTEit1_1.opExtrude","SWEPT_EDGE",EDGE,{"disambiguationData":[OSD([subQ2,sQuery(id+"F3.wireOp",EDGE,"E5.15.0.0"),subQ1])]})});var subQ4=makeQuery(id+"F5.imprint","INTERSECT",VERTEX,{"derivedFrom":[subQ3,subQ0]});Q79=makeQuery(id+"F5.imprint","IMPRINT",FACE,{"disambiguationData":[TD([[makeQuery(id+"F5.imprint","IMPRINT",EDGE,{"disambiguationData":[TD([[subQ4,-1.0]])],"derivedFrom":subQ0}),1.0]])]});}
            extrude(context, id + "F11", {"entities" : qUnion([Q0, Q1, Q2, Q3, Q4, Q5, Q6, Q7, Q8, Q9, Q10, Q11, Q12, Q13, Q14, Q15, Q16, Q17, Q18, Q19, Q20, Q21, Q22, Q23, Q24, Q25, Q26, Q27, Q28, Q29, Q30, Q31, Q32, Q33, Q34, Q35, Q36, Q37, Q38, Q39, Q40, Q41, Q42, Q43, Q44, Q45, Q46, Q47, Q48, Q49, Q50, Q51, Q52, Q53, Q54, Q55, Q56, Q57, Q58, Q59, Q60, Q61, Q62, Q63, Q64, Q65, Q66, Q67, Q68, Q69, Q70, Q71, Q72, Q73, Q74, Q75, Q76, Q77, Q78, Q79]), "depth" : 533.4 * mm, "offsetDistance" : 25.4 * mm});
        }
        {
            var Q0;
            {var subQ0=sQuery(id+"F5.wireOp",EDGE,"E13.left");var subQ1=sQuery(id+"F0.wireOp",EDGE,"E0.left");var subQ2=makeQuery(id+"FlHhq8AFgQTEit1_1.boolean.opBoolean","COPY",EDGE,{"derivedFrom":makeQuery(id+"FlHhq8AFgQTEit1_1.opExtrude","SWEPT_EDGE",EDGE,{"disambiguationData":[OSD([subQ1,sQuery(id+"F3.wireOp",EDGE,"E5.7.0.0"),sQuery(id+"F3.wireOp",EDGE,"E5.7.0.1")])]})});var subQ3=makeQuery(id+"F5.imprint","INTERSECT",VERTEX,{"derivedFrom":[subQ2,subQ0]});Q0=makeQuery(id+"F5.imprint","IMPRINT",FACE,{"disambiguationData":[TD([[makeQuery(id+"F5.imprint","IMPRINT",EDGE,{"disambiguationData":[TD([[subQ3,-1.0]])],"derivedFrom":subQ0}),1.0]])]});}
            var Q1;
            {var subQ0=sQuery(id+"F5.wireOp",EDGE,"E13.left");var subQ1=sQuery(id+"F3.wireOp",EDGE,"E5.6.0.1");var subQ2=sQuery(id+"F0.wireOp",EDGE,"E0.left");var subQ3=makeQuery(id+"FlHhq8AFgQTEit1_1.boolean.opBoolean","COPY",EDGE,{"derivedFrom":makeQuery(id+"FlHhq8AFgQTEit1_1.opExtrude","SWEPT_EDGE",EDGE,{"disambiguationData":[OSD([subQ2,subQ1,sQuery(id+"F3.wireOp",EDGE,"E5.6.0.2")])]})});var subQ4=makeQuery(id+"F5.imprint","INTERSECT",VERTEX,{"derivedFrom":[subQ3,subQ0]});Q1=makeQuery(id+"F5.imprint","IMPRINT",FACE,{"disambiguationData":[TD([[makeQuery(id+"F5.imprint","IMPRINT",EDGE,{"disambiguationData":[TD([[subQ4,-1.0]])],"derivedFrom":subQ0}),1.0]])]});}
            var Q2;
            {var subQ0=sQuery(id+"F5.wireOp",EDGE,"E13.left");var subQ1=sQuery(id+"F3.wireOp",EDGE,"E5.3.0.1");var subQ2=sQuery(id+"F0.wireOp",EDGE,"E0.left");var subQ3=makeQuery(id+"FlHhq8AFgQTEit1_1.boolean.opBoolean","COPY",EDGE,{"derivedFrom":makeQuery(id+"FlHhq8AFgQTEit1_1.opExtrude","SWEPT_EDGE",EDGE,{"disambiguationData":[OSD([subQ2,subQ1,sQuery(id+"F3.wireOp",EDGE,"E5.3.0.2")])]})});var subQ4=makeQuery(id+"F5.imprint","INTERSECT",VERTEX,{"derivedFrom":[subQ3,subQ0]});Q2=makeQuery(id+"F5.imprint","IMPRINT",FACE,{"disambiguationData":[TD([[makeQuery(id+"F5.imprint","IMPRINT",EDGE,{"disambiguationData":[TD([[subQ4,-1.0]])],"derivedFrom":subQ0}),1.0]])]});}
            var Q3;
            {var subQ0=sQuery(id+"F5.wireOp",EDGE,"E13.left");var subQ1=sQuery(id+"F3.wireOp",EDGE,"E5.2.0.1");var subQ2=sQuery(id+"F0.wireOp",EDGE,"E0.left");var subQ3=makeQuery(id+"FlHhq8AFgQTEit1_1.boolean.opBoolean","COPY",EDGE,{"derivedFrom":makeQuery(id+"FlHhq8AFgQTEit1_1.opExtrude","SWEPT_EDGE",EDGE,{"disambiguationData":[OSD([subQ2,subQ1,sQuery(id+"F3.wireOp",EDGE,"E5.2.0.2")])]})});var subQ4=makeQuery(id+"F5.imprint","INTERSECT",VERTEX,{"derivedFrom":[subQ3,subQ0]});Q3=makeQuery(id+"F5.imprint","IMPRINT",FACE,{"disambiguationData":[TD([[makeQuery(id+"F5.imprint","IMPRINT",EDGE,{"disambiguationData":[TD([[subQ4,-1.0]])],"derivedFrom":subQ0}),1.0]])]});}
            var Q4;
            {var subQ0=sQuery(id+"F5.wireOp",EDGE,"E13.left");var subQ1=sQuery(id+"F3.wireOp",EDGE,"E5.8.0.1");var subQ2=sQuery(id+"F0.wireOp",EDGE,"E0.left");var subQ3=makeQuery(id+"FlHhq8AFgQTEit1_1.boolean.opBoolean","COPY",EDGE,{"derivedFrom":makeQuery(id+"FlHhq8AFgQTEit1_1.opExtrude","SWEPT_EDGE",EDGE,{"disambiguationData":[OSD([subQ2,subQ1,sQuery(id+"F3.wireOp",EDGE,"E5.8.0.2")])]})});var subQ4=makeQuery(id+"F5.imprint","INTERSECT",VERTEX,{"derivedFrom":[subQ3,subQ0]});Q4=makeQuery(id+"F5.imprint","IMPRINT",FACE,{"disambiguationData":[TD([[makeQuery(id+"F5.imprint","IMPRINT",EDGE,{"disambiguationData":[TD([[subQ4,-1.0]])],"derivedFrom":subQ0}),1.0]])]});}
            var Q5;
            {var subQ0=sQuery(id+"F5.wireOp",EDGE,"E13.left");var subQ1=sQuery(id+"F0.wireOp",EDGE,"E0.left");var subQ2=makeQuery(id+"FlHhq8AFgQTEit1_1.boolean.opBoolean","COPY",EDGE,{"derivedFrom":makeQuery(id+"FlHhq8AFgQTEit1_1.opExtrude","SWEPT_EDGE",EDGE,{"disambiguationData":[OSD([subQ1,sQuery(id+"F3.wireOp",EDGE,"E5.3.0.0"),sQuery(id+"F3.wireOp",EDGE,"E5.3.0.1")])]})});var subQ3=makeQuery(id+"F5.imprint","INTERSECT",VERTEX,{"derivedFrom":[subQ2,subQ0]});Q5=makeQuery(id+"F5.imprint","IMPRINT",FACE,{"disambiguationData":[TD([[makeQuery(id+"F5.imprint","IMPRINT",EDGE,{"disambiguationData":[TD([[subQ3,-1.0]])],"derivedFrom":subQ0}),1.0]])]});}
            var Q6;
            {var subQ0=sQuery(id+"F5.wireOp",EDGE,"E13.left");var subQ1=sQuery(id+"F0.wireOp",EDGE,"E0.left");var subQ2=makeQuery(id+"FlHhq8AFgQTEit1_1.boolean.opBoolean","COPY",EDGE,{"derivedFrom":makeQuery(id+"FlHhq8AFgQTEit1_1.opExtrude","SWEPT_EDGE",EDGE,{"disambiguationData":[OSD([subQ1,sQuery(id+"F3.wireOp",EDGE,"E5.2.0.0"),sQuery(id+"F3.wireOp",EDGE,"E5.2.0.1")])]})});var subQ3=makeQuery(id+"F5.imprint","INTERSECT",VERTEX,{"derivedFrom":[subQ2,subQ0]});Q6=makeQuery(id+"F5.imprint","IMPRINT",FACE,{"disambiguationData":[TD([[makeQuery(id+"F5.imprint","IMPRINT",EDGE,{"disambiguationData":[TD([[subQ3,-1.0]])],"derivedFrom":subQ0}),1.0]])]});}
            var Q7;
            {var subQ0=sQuery(id+"F5.wireOp",EDGE,"E13.left");var subQ1=sQuery(id+"F0.wireOp",EDGE,"E0.left");var subQ2=makeQuery(id+"FlHhq8AFgQTEit1_1.boolean.opBoolean","COPY",EDGE,{"derivedFrom":makeQuery(id+"FlHhq8AFgQTEit1_1.opExtrude","SWEPT_EDGE",EDGE,{"disambiguationData":[OSD([subQ1,sQuery(id+"F3.wireOp",EDGE,"E5.5.0.0"),sQuery(id+"F3.wireOp",EDGE,"E5.5.0.1")])]})});var subQ3=makeQuery(id+"F5.imprint","INTERSECT",VERTEX,{"derivedFrom":[subQ2,subQ0]});Q7=makeQuery(id+"F5.imprint","IMPRINT",FACE,{"disambiguationData":[TD([[makeQuery(id+"F5.imprint","IMPRINT",EDGE,{"disambiguationData":[TD([[subQ3,-1.0]])],"derivedFrom":subQ0}),1.0]])]});}
            var Q8;
            {var subQ0=sQuery(id+"F5.wireOp",EDGE,"E13.left");var subQ1=sQuery(id+"F0.wireOp",EDGE,"E0.left");var subQ2=makeQuery(id+"FlHhq8AFgQTEit1_1.boolean.opBoolean","COPY",EDGE,{"derivedFrom":makeQuery(id+"FlHhq8AFgQTEit1_1.opExtrude","SWEPT_EDGE",EDGE,{"disambiguationData":[OSD([subQ1,sQuery(id+"F3.wireOp",EDGE,"E5.9.0.0"),sQuery(id+"F3.wireOp",EDGE,"E5.9.0.1")])]})});var subQ3=makeQuery(id+"F5.imprint","INTERSECT",VERTEX,{"derivedFrom":[subQ2,subQ0]});Q8=makeQuery(id+"F5.imprint","IMPRINT",FACE,{"disambiguationData":[TD([[makeQuery(id+"F5.imprint","IMPRINT",EDGE,{"disambiguationData":[TD([[subQ3,-1.0]])],"derivedFrom":subQ0}),1.0]])]});}
            var Q9;
            {var subQ0=sQuery(id+"F5.wireOp",EDGE,"E13.left");var subQ1=sQuery(id+"F3.wireOp",EDGE,"E5.1.0.1");var subQ2=sQuery(id+"F0.wireOp",EDGE,"E0.left");var subQ3=makeQuery(id+"FlHhq8AFgQTEit1_1.boolean.opBoolean","COPY",EDGE,{"derivedFrom":makeQuery(id+"FlHhq8AFgQTEit1_1.opExtrude","SWEPT_EDGE",EDGE,{"disambiguationData":[OSD([subQ2,subQ1,sQuery(id+"F3.wireOp",EDGE,"E5.1.0.2")])]})});var subQ4=makeQuery(id+"F5.imprint","INTERSECT",VERTEX,{"derivedFrom":[subQ3,subQ0]});Q9=makeQuery(id+"F5.imprint","IMPRINT",FACE,{"disambiguationData":[TD([[makeQuery(id+"F5.imprint","IMPRINT",EDGE,{"disambiguationData":[TD([[subQ4,-1.0]])],"derivedFrom":subQ0}),1.0]])]});}
            var Q10;
            {var subQ0=sQuery(id+"F5.wireOp",EDGE,"E13.left");var subQ1=sQuery(id+"F3.wireOp",EDGE,"E5.7.0.1");var subQ2=sQuery(id+"F0.wireOp",EDGE,"E0.left");var subQ3=makeQuery(id+"FlHhq8AFgQTEit1_1.boolean.opBoolean","COPY",EDGE,{"derivedFrom":makeQuery(id+"FlHhq8AFgQTEit1_1.opExtrude","SWEPT_EDGE",EDGE,{"disambiguationData":[OSD([subQ2,subQ1,sQuery(id+"F3.wireOp",EDGE,"E5.7.0.2")])]})});var subQ4=makeQuery(id+"F5.imprint","INTERSECT",VERTEX,{"derivedFrom":[subQ3,subQ0]});Q10=makeQuery(id+"F5.imprint","IMPRINT",FACE,{"disambiguationData":[TD([[makeQuery(id+"F5.imprint","IMPRINT",EDGE,{"disambiguationData":[TD([[subQ4,-1.0]])],"derivedFrom":subQ0}),1.0]])]});}
            var Q11;
            {var subQ0=sQuery(id+"F5.wireOp",EDGE,"E13.left");var subQ1=sQuery(id+"F3.wireOp",EDGE,"E4");var subQ2=sQuery(id+"F0.wireOp",EDGE,"E0.left");var subQ3=makeQuery(id+"FlHhq8AFgQTEit1_1.boolean.opBoolean","COPY",EDGE,{"derivedFrom":makeQuery(id+"FlHhq8AFgQTEit1_1.opExtrude","SWEPT_EDGE",EDGE,{"disambiguationData":[OSD([subQ2,sQuery(id+"F3.wireOp",EDGE,"E3"),subQ1])]})});var subQ4=makeQuery(id+"F5.imprint","INTERSECT",VERTEX,{"derivedFrom":[subQ3,subQ0]});Q11=makeQuery(id+"F5.imprint","IMPRINT",FACE,{"disambiguationData":[TD([[makeQuery(id+"F5.imprint","IMPRINT",EDGE,{"disambiguationData":[TD([[subQ4,-1.0]])],"derivedFrom":subQ0}),1.0]])]});}
            var Q12;
            {var subQ0=sQuery(id+"F5.wireOp",EDGE,"E13.left");var subQ1=sQuery(id+"F0.wireOp",EDGE,"E0.left");var subQ2=makeQuery(id+"FlHhq8AFgQTEit1_1.boolean.opBoolean","COPY",EDGE,{"derivedFrom":makeQuery(id+"FlHhq8AFgQTEit1_1.opExtrude","SWEPT_EDGE",EDGE,{"disambiguationData":[OSD([subQ1,sQuery(id+"F3.wireOp",EDGE,"E5.6.0.0"),sQuery(id+"F3.wireOp",EDGE,"E5.6.0.1")])]})});var subQ3=makeQuery(id+"F5.imprint","INTERSECT",VERTEX,{"derivedFrom":[subQ2,subQ0]});Q12=makeQuery(id+"F5.imprint","IMPRINT",FACE,{"disambiguationData":[TD([[makeQuery(id+"F5.imprint","IMPRINT",EDGE,{"disambiguationData":[TD([[subQ3,-1.0]])],"derivedFrom":subQ0}),1.0]])]});}
            var Q13;
            {var subQ0=sQuery(id+"F5.wireOp",EDGE,"E13.left");var subQ1=sQuery(id+"F3.wireOp",EDGE,"E5.9.0.1");var subQ2=sQuery(id+"F0.wireOp",EDGE,"E0.left");var subQ3=makeQuery(id+"FlHhq8AFgQTEit1_1.boolean.opBoolean","COPY",EDGE,{"derivedFrom":makeQuery(id+"FlHhq8AFgQTEit1_1.opExtrude","SWEPT_EDGE",EDGE,{"disambiguationData":[OSD([subQ2,subQ1,sQuery(id+"F3.wireOp",EDGE,"E5.9.0.2")])]})});var subQ4=makeQuery(id+"F5.imprint","INTERSECT",VERTEX,{"derivedFrom":[subQ3,subQ0]});Q13=makeQuery(id+"F5.imprint","IMPRINT",FACE,{"disambiguationData":[TD([[makeQuery(id+"F5.imprint","IMPRINT",EDGE,{"disambiguationData":[TD([[subQ4,-1.0]])],"derivedFrom":subQ0}),1.0]])]});}
            var Q14;
            {var subQ0=sQuery(id+"F5.wireOp",EDGE,"E13.left");var subQ1=sQuery(id+"F3.wireOp",EDGE,"E5.4.0.1");var subQ2=sQuery(id+"F0.wireOp",EDGE,"E0.left");var subQ3=makeQuery(id+"FlHhq8AFgQTEit1_1.boolean.opBoolean","COPY",EDGE,{"derivedFrom":makeQuery(id+"FlHhq8AFgQTEit1_1.opExtrude","SWEPT_EDGE",EDGE,{"disambiguationData":[OSD([subQ2,subQ1,sQuery(id+"F3.wireOp",EDGE,"E5.4.0.2")])]})});var subQ4=makeQuery(id+"F5.imprint","INTERSECT",VERTEX,{"derivedFrom":[subQ3,subQ0]});Q14=makeQuery(id+"F5.imprint","IMPRINT",FACE,{"disambiguationData":[TD([[makeQuery(id+"F5.imprint","IMPRINT",EDGE,{"disambiguationData":[TD([[subQ4,-1.0]])],"derivedFrom":subQ0}),1.0]])]});}
            var Q15;
            {var subQ0=sQuery(id+"F5.wireOp",EDGE,"E13.left");var subQ1=sQuery(id+"F3.wireOp",EDGE,"E5.5.0.1");var subQ2=sQuery(id+"F0.wireOp",EDGE,"E0.left");var subQ3=makeQuery(id+"FlHhq8AFgQTEit1_1.boolean.opBoolean","COPY",EDGE,{"derivedFrom":makeQuery(id+"FlHhq8AFgQTEit1_1.opExtrude","SWEPT_EDGE",EDGE,{"disambiguationData":[OSD([subQ2,subQ1,sQuery(id+"F3.wireOp",EDGE,"E5.5.0.2")])]})});var subQ4=makeQuery(id+"F5.imprint","INTERSECT",VERTEX,{"derivedFrom":[subQ3,subQ0]});Q15=makeQuery(id+"F5.imprint","IMPRINT",FACE,{"disambiguationData":[TD([[makeQuery(id+"F5.imprint","IMPRINT",EDGE,{"disambiguationData":[TD([[subQ4,-1.0]])],"derivedFrom":subQ0}),1.0]])]});}
            var Q16;
            {var subQ0=sQuery(id+"F5.wireOp",EDGE,"E13.left");var subQ1=sQuery(id+"F0.wireOp",EDGE,"E0.left");var subQ2=makeQuery(id+"FlHhq8AFgQTEit1_1.boolean.opBoolean","COPY",EDGE,{"derivedFrom":makeQuery(id+"FlHhq8AFgQTEit1_1.opExtrude","SWEPT_EDGE",EDGE,{"disambiguationData":[OSD([subQ1,sQuery(id+"F3.wireOp",EDGE,"E5.4.0.0"),sQuery(id+"F3.wireOp",EDGE,"E5.4.0.1")])]})});var subQ3=makeQuery(id+"F5.imprint","INTERSECT",VERTEX,{"derivedFrom":[subQ2,subQ0]});Q16=makeQuery(id+"F5.imprint","IMPRINT",FACE,{"disambiguationData":[TD([[makeQuery(id+"F5.imprint","IMPRINT",EDGE,{"disambiguationData":[TD([[subQ3,-1.0]])],"derivedFrom":subQ0}),1.0]])]});}
            var Q17;
            {var subQ0=sQuery(id+"F5.wireOp",EDGE,"E13.left");var subQ1=sQuery(id+"F0.wireOp",EDGE,"E0.left");var subQ2=makeQuery(id+"FlHhq8AFgQTEit1_1.boolean.opBoolean","COPY",EDGE,{"derivedFrom":makeQuery(id+"FlHhq8AFgQTEit1_1.opExtrude","SWEPT_EDGE",EDGE,{"disambiguationData":[OSD([subQ1,sQuery(id+"F3.wireOp",EDGE,"E5.8.0.0"),sQuery(id+"F3.wireOp",EDGE,"E5.8.0.1")])]})});var subQ3=makeQuery(id+"F5.imprint","INTERSECT",VERTEX,{"derivedFrom":[subQ2,subQ0]});Q17=makeQuery(id+"F5.imprint","IMPRINT",FACE,{"disambiguationData":[TD([[makeQuery(id+"F5.imprint","IMPRINT",EDGE,{"disambiguationData":[TD([[subQ3,-1.0]])],"derivedFrom":subQ0}),1.0]])]});}
            var Q18;
            {var subQ0=sQuery(id+"F5.wireOp",EDGE,"E13.left");var subQ1=sQuery(id+"F0.wireOp",EDGE,"E0.left");var subQ2=makeQuery(id+"FlHhq8AFgQTEit1_1.boolean.opBoolean","COPY",EDGE,{"derivedFrom":makeQuery(id+"FlHhq8AFgQTEit1_1.opExtrude","SWEPT_EDGE",EDGE,{"disambiguationData":[OSD([subQ1,sQuery(id+"F3.wireOp",EDGE,"E5.1.0.0"),sQuery(id+"F3.wireOp",EDGE,"E5.1.0.1")])]})});var subQ3=makeQuery(id+"F5.imprint","INTERSECT",VERTEX,{"derivedFrom":[subQ2,subQ0]});Q18=makeQuery(id+"F5.imprint","IMPRINT",FACE,{"disambiguationData":[TD([[makeQuery(id+"F5.imprint","IMPRINT",EDGE,{"disambiguationData":[TD([[subQ3,-1.0]])],"derivedFrom":subQ0}),1.0]])]});}
            var Q19;
            {var subQ0=sQuery(id+"F5.wireOp",EDGE,"E13.top");Q19=makeQuery(id+"F5.imprint","IMPRINT",FACE,{"disambiguationData":[TD([[makeQuery(id+"F5.imprint","IMPRINT",EDGE,{"derivedFrom":subQ0}),-1.0]])]});}
            var Q20;
            {var subQ0=sQuery(id+"F5.wireOp",EDGE,"E13.left");var subQ8=makeQuery(id+"F5.imprint","INTERSECT",VERTEX,{"derivedFrom":[sQuery(id+"F5.wireOp",EDGE,"E12.top"),subQ0]});Q20=makeQuery(id+"F5.imprint","IMPRINT",FACE,{"disambiguationData":[TD([[makeQuery(id+"F5.imprint","IMPRINT",EDGE,{"disambiguationData":[TD([[subQ8,1.0]])],"derivedFrom":subQ0}),1.0]])]});}
            var Q21;
            {var subQ1=sQuery(id+"F3.wireOp",EDGE,"E5.10.0.1");var subQ2=sQuery(id+"F0.wireOp",EDGE,"E0.left");var subQ3=makeQuery(id+"FlHhq8AFgQTEit1_1.boolean.opBoolean","COPY",EDGE,{"derivedFrom":makeQuery(id+"FlHhq8AFgQTEit1_1.opExtrude","SWEPT_EDGE",EDGE,{"disambiguationData":[OSD([subQ2,subQ1,sQuery(id+"F3.wireOp",EDGE,"E5.10.0.2")])]})});var subQ7=sQuery(id+"F5.wireOp",EDGE,"E24.trimOffspring");var subQ8=makeQuery(id+"F5.imprint","INTERSECT",VERTEX,{"derivedFrom":[subQ3,subQ7]});Q21=makeQuery(id+"F5.imprint","IMPRINT",FACE,{"disambiguationData":[TD([[makeQuery(id+"F5.imprint","IMPRINT",EDGE,{"disambiguationData":[TD([[subQ8,-1.0]])],"derivedFrom":subQ7}),-1.0]])]});}
            var Q22;
            {var subQ1=sQuery(id+"F0.wireOp",EDGE,"E0.left");var subQ4=makeQuery(id+"FlHhq8AFgQTEit1_1.boolean.opBoolean","COPY",EDGE,{"derivedFrom":makeQuery(id+"FlHhq8AFgQTEit1_1.opExtrude","SWEPT_EDGE",EDGE,{"disambiguationData":[OSD([subQ1,sQuery(id+"F3.wireOp",EDGE,"E5.11.0.0"),sQuery(id+"F3.wireOp",EDGE,"E5.11.0.1")])]})});var subQ6=sQuery(id+"F5.wireOp",EDGE,"E24.trimOffspring");var subQ7=makeQuery(id+"F5.imprint","INTERSECT",VERTEX,{"derivedFrom":[subQ4,subQ6]});Q22=makeQuery(id+"F5.imprint","IMPRINT",FACE,{"disambiguationData":[TD([[makeQuery(id+"F5.imprint","IMPRINT",EDGE,{"disambiguationData":[TD([[subQ7,-1.0]])],"derivedFrom":subQ6}),-1.0]])]});}
            var Q23;
            {var subQ0=sQuery(id+"F5.wireOp",EDGE,"E18.bottom");var subQ7=sQuery(id+"F5.wireOp",EDGE,"E24.trimOffspring");var subQ8=makeQuery(id+"F5.imprint","INTERSECT",VERTEX,{"derivedFrom":[subQ0,subQ7]});Q23=makeQuery(id+"F5.imprint","IMPRINT",FACE,{"disambiguationData":[TD([[makeQuery(id+"F5.imprint","IMPRINT",EDGE,{"disambiguationData":[TD([[subQ8,-1.0]])],"derivedFrom":subQ7}),-1.0]])]});}
            var Q24;
            {var subQ0=sQuery(id+"F5.wireOp",EDGE,"E19");var subQ1=sQuery(id+"F0.wireOp",EDGE,"E0.left");var subQ2=makeQuery(id+"FlHhq8AFgQTEit1_1.boolean.opBoolean","COPY",EDGE,{"derivedFrom":makeQuery(id+"FlHhq8AFgQTEit1_1.opExtrude","SWEPT_EDGE",EDGE,{"disambiguationData":[OSD([subQ1,sQuery(id+"F3.wireOp",EDGE,"E5.4.0.1"),sQuery(id+"F3.wireOp",EDGE,"E5.4.0.2")])]})});var subQ3=makeQuery(id+"F5.imprint","INTERSECT",VERTEX,{"derivedFrom":[subQ2,subQ0]});Q24=makeQuery(id+"F5.imprint","IMPRINT",FACE,{"disambiguationData":[TD([[makeQuery(id+"F5.imprint","IMPRINT",EDGE,{"disambiguationData":[TD([[subQ3,-1.0]])],"derivedFrom":subQ0}),1.0]])]});}
            var Q25;
            {var subQ0=sQuery(id+"F5.wireOp",EDGE,"E19");var subQ1=sQuery(id+"F0.wireOp",EDGE,"E0.left");var subQ2=makeQuery(id+"FlHhq8AFgQTEit1_1.boolean.opBoolean","COPY",EDGE,{"derivedFrom":makeQuery(id+"FlHhq8AFgQTEit1_1.opExtrude","SWEPT_EDGE",EDGE,{"disambiguationData":[OSD([subQ1,sQuery(id+"F3.wireOp",EDGE,"E5.1.0.1"),sQuery(id+"F3.wireOp",EDGE,"E5.1.0.2")])]})});var subQ3=makeQuery(id+"F5.imprint","INTERSECT",VERTEX,{"derivedFrom":[subQ2,subQ0]});Q25=makeQuery(id+"F5.imprint","IMPRINT",FACE,{"disambiguationData":[TD([[makeQuery(id+"F5.imprint","IMPRINT",EDGE,{"disambiguationData":[TD([[subQ3,-1.0]])],"derivedFrom":subQ0}),1.0]])]});}
            var Q26;
            {var subQ0=sQuery(id+"F5.wireOp",EDGE,"E19");var subQ1=sQuery(id+"F3.wireOp",EDGE,"E5.8.0.1");var subQ2=sQuery(id+"F0.wireOp",EDGE,"E0.left");var subQ3=makeQuery(id+"FlHhq8AFgQTEit1_1.boolean.opBoolean","COPY",EDGE,{"derivedFrom":makeQuery(id+"FlHhq8AFgQTEit1_1.opExtrude","SWEPT_EDGE",EDGE,{"disambiguationData":[OSD([subQ2,sQuery(id+"F3.wireOp",EDGE,"E5.8.0.0"),subQ1])]})});var subQ4=makeQuery(id+"F5.imprint","INTERSECT",VERTEX,{"derivedFrom":[subQ3,subQ0]});Q26=makeQuery(id+"F5.imprint","IMPRINT",FACE,{"disambiguationData":[TD([[makeQuery(id+"F5.imprint","IMPRINT",EDGE,{"disambiguationData":[TD([[subQ4,-1.0]])],"derivedFrom":subQ0}),1.0]])]});}
            var Q27;
            {var subQ0=sQuery(id+"F5.wireOp",EDGE,"E19");var subQ1=makeQuery(id+"F1.opExtrude","CAP_EDGE",EDGE,{"disambiguationData":[OSD([sQuery(id+"F0.wireOp",EDGE,"E0.top")])],"isStart":true});var subQ2=makeQuery(id+"F5.imprint","INTERSECT",VERTEX,{"derivedFrom":[subQ1,subQ0]});Q27=makeQuery(id+"F5.imprint","IMPRINT",FACE,{"disambiguationData":[TD([[makeQuery(id+"F5.imprint","IMPRINT",EDGE,{"disambiguationData":[TD([[subQ2,-1.0]])],"derivedFrom":subQ1}),-1.0]])]});}
            var Q28;
            {var subQ0=sQuery(id+"F5.wireOp",EDGE,"E19");var subQ1=sQuery(id+"F0.wireOp",EDGE,"E0.left");var subQ2=makeQuery(id+"FlHhq8AFgQTEit1_1.boolean.opBoolean","COPY",EDGE,{"derivedFrom":makeQuery(id+"FlHhq8AFgQTEit1_1.opExtrude","SWEPT_EDGE",EDGE,{"disambiguationData":[OSD([subQ1,sQuery(id+"F3.wireOp",EDGE,"E5.10.0.1"),sQuery(id+"F3.wireOp",EDGE,"E5.10.0.2")])]})});var subQ3=makeQuery(id+"F5.imprint","INTERSECT",VERTEX,{"derivedFrom":[subQ2,subQ0]});Q28=makeQuery(id+"F5.imprint","IMPRINT",FACE,{"disambiguationData":[TD([[makeQuery(id+"F5.imprint","IMPRINT",EDGE,{"disambiguationData":[TD([[subQ3,-1.0]])],"derivedFrom":subQ0}),1.0]])]});}
            var Q29;
            {var subQ0=sQuery(id+"F5.wireOp",EDGE,"E19");var subQ1=sQuery(id+"F0.wireOp",EDGE,"E0.left");var subQ2=makeQuery(id+"FlHhq8AFgQTEit1_1.boolean.opBoolean","COPY",EDGE,{"derivedFrom":makeQuery(id+"FlHhq8AFgQTEit1_1.opExtrude","SWEPT_EDGE",EDGE,{"disambiguationData":[OSD([subQ1,sQuery(id+"F3.wireOp",EDGE,"E5.7.0.1"),sQuery(id+"F3.wireOp",EDGE,"E5.7.0.2")])]})});var subQ3=makeQuery(id+"F5.imprint","INTERSECT",VERTEX,{"derivedFrom":[subQ2,subQ0]});Q29=makeQuery(id+"F5.imprint","IMPRINT",FACE,{"disambiguationData":[TD([[makeQuery(id+"F5.imprint","IMPRINT",EDGE,{"disambiguationData":[TD([[subQ3,-1.0]])],"derivedFrom":subQ0}),1.0]])]});}
            var Q30;
            {var subQ0=sQuery(id+"F5.wireOp",EDGE,"E19");var subQ1=sQuery(id+"F3.wireOp",EDGE,"E5.5.0.1");var subQ2=sQuery(id+"F0.wireOp",EDGE,"E0.left");var subQ3=makeQuery(id+"FlHhq8AFgQTEit1_1.boolean.opBoolean","COPY",EDGE,{"derivedFrom":makeQuery(id+"FlHhq8AFgQTEit1_1.opExtrude","SWEPT_EDGE",EDGE,{"disambiguationData":[OSD([subQ2,sQuery(id+"F3.wireOp",EDGE,"E5.5.0.0"),subQ1])]})});var subQ4=makeQuery(id+"F5.imprint","INTERSECT",VERTEX,{"derivedFrom":[subQ3,subQ0]});Q30=makeQuery(id+"F5.imprint","IMPRINT",FACE,{"disambiguationData":[TD([[makeQuery(id+"F5.imprint","IMPRINT",EDGE,{"disambiguationData":[TD([[subQ4,-1.0]])],"derivedFrom":subQ0}),1.0]])]});}
            var Q31;
            {var subQ0=sQuery(id+"F5.wireOp",EDGE,"E19");var subQ1=sQuery(id+"F3.wireOp",EDGE,"E5.1.0.1");var subQ2=sQuery(id+"F0.wireOp",EDGE,"E0.left");var subQ3=makeQuery(id+"FlHhq8AFgQTEit1_1.boolean.opBoolean","COPY",EDGE,{"derivedFrom":makeQuery(id+"FlHhq8AFgQTEit1_1.opExtrude","SWEPT_EDGE",EDGE,{"disambiguationData":[OSD([subQ2,sQuery(id+"F3.wireOp",EDGE,"E5.1.0.0"),subQ1])]})});var subQ4=makeQuery(id+"F5.imprint","INTERSECT",VERTEX,{"derivedFrom":[subQ3,subQ0]});Q31=makeQuery(id+"F5.imprint","IMPRINT",FACE,{"disambiguationData":[TD([[makeQuery(id+"F5.imprint","IMPRINT",EDGE,{"disambiguationData":[TD([[subQ4,-1.0]])],"derivedFrom":subQ0}),1.0]])]});}
            var Q32;
            {var subQ0=sQuery(id+"F5.wireOp",EDGE,"E19");var subQ1=sQuery(id+"F0.wireOp",EDGE,"E0.left");var subQ2=makeQuery(id+"FlHhq8AFgQTEit1_1.boolean.opBoolean","COPY",EDGE,{"derivedFrom":makeQuery(id+"FlHhq8AFgQTEit1_1.opExtrude","SWEPT_EDGE",EDGE,{"disambiguationData":[OSD([subQ1,sQuery(id+"F3.wireOp",EDGE,"E5.5.0.1"),sQuery(id+"F3.wireOp",EDGE,"E5.5.0.2")])]})});var subQ3=makeQuery(id+"F5.imprint","INTERSECT",VERTEX,{"derivedFrom":[subQ2,subQ0]});Q32=makeQuery(id+"F5.imprint","IMPRINT",FACE,{"disambiguationData":[TD([[makeQuery(id+"F5.imprint","IMPRINT",EDGE,{"disambiguationData":[TD([[subQ3,-1.0]])],"derivedFrom":subQ0}),1.0]])]});}
            var Q33;
            {var subQ0=sQuery(id+"F5.wireOp",EDGE,"E19");var subQ1=sQuery(id+"F3.wireOp",EDGE,"E5.4.0.1");var subQ2=sQuery(id+"F0.wireOp",EDGE,"E0.left");var subQ3=makeQuery(id+"FlHhq8AFgQTEit1_1.boolean.opBoolean","COPY",EDGE,{"derivedFrom":makeQuery(id+"FlHhq8AFgQTEit1_1.opExtrude","SWEPT_EDGE",EDGE,{"disambiguationData":[OSD([subQ2,sQuery(id+"F3.wireOp",EDGE,"E5.4.0.0"),subQ1])]})});var subQ4=makeQuery(id+"F5.imprint","INTERSECT",VERTEX,{"derivedFrom":[subQ3,subQ0]});Q33=makeQuery(id+"F5.imprint","IMPRINT",FACE,{"disambiguationData":[TD([[makeQuery(id+"F5.imprint","IMPRINT",EDGE,{"disambiguationData":[TD([[subQ4,-1.0]])],"derivedFrom":subQ0}),1.0]])]});}
            var Q34;
            {var subQ0=sQuery(id+"F5.wireOp",EDGE,"E19");var subQ1=sQuery(id+"F0.wireOp",EDGE,"E0.left");var subQ2=makeQuery(id+"FlHhq8AFgQTEit1_1.boolean.opBoolean","COPY",EDGE,{"derivedFrom":makeQuery(id+"FlHhq8AFgQTEit1_1.opExtrude","SWEPT_EDGE",EDGE,{"disambiguationData":[OSD([subQ1,sQuery(id+"F3.wireOp",EDGE,"E5.8.0.1"),sQuery(id+"F3.wireOp",EDGE,"E5.8.0.2")])]})});var subQ3=makeQuery(id+"F5.imprint","INTERSECT",VERTEX,{"derivedFrom":[subQ2,subQ0]});Q34=makeQuery(id+"F5.imprint","IMPRINT",FACE,{"disambiguationData":[TD([[makeQuery(id+"F5.imprint","IMPRINT",EDGE,{"disambiguationData":[TD([[subQ3,-1.0]])],"derivedFrom":subQ0}),1.0]])]});}
            var Q35;
            {var subQ0=sQuery(id+"F5.wireOp",EDGE,"E19");var subQ1=sQuery(id+"F0.wireOp",EDGE,"E0.left");var subQ2=makeQuery(id+"FlHhq8AFgQTEit1_1.boolean.opBoolean","COPY",EDGE,{"derivedFrom":makeQuery(id+"FlHhq8AFgQTEit1_1.opExtrude","SWEPT_EDGE",EDGE,{"disambiguationData":[OSD([subQ1,sQuery(id+"F3.wireOp",EDGE,"E5.9.0.1"),sQuery(id+"F3.wireOp",EDGE,"E5.9.0.2")])]})});var subQ3=makeQuery(id+"F5.imprint","INTERSECT",VERTEX,{"derivedFrom":[subQ2,subQ0]});Q35=makeQuery(id+"F5.imprint","IMPRINT",FACE,{"disambiguationData":[TD([[makeQuery(id+"F5.imprint","IMPRINT",EDGE,{"disambiguationData":[TD([[subQ3,-1.0]])],"derivedFrom":subQ0}),1.0]])]});}
            var Q36;
            {var subQ0=sQuery(id+"F5.wireOp",EDGE,"E19");var subQ1=sQuery(id+"F3.wireOp",EDGE,"E5.9.0.1");var subQ2=sQuery(id+"F0.wireOp",EDGE,"E0.left");var subQ3=makeQuery(id+"FlHhq8AFgQTEit1_1.boolean.opBoolean","COPY",EDGE,{"derivedFrom":makeQuery(id+"FlHhq8AFgQTEit1_1.opExtrude","SWEPT_EDGE",EDGE,{"disambiguationData":[OSD([subQ2,sQuery(id+"F3.wireOp",EDGE,"E5.9.0.0"),subQ1])]})});var subQ4=makeQuery(id+"F5.imprint","INTERSECT",VERTEX,{"derivedFrom":[subQ3,subQ0]});Q36=makeQuery(id+"F5.imprint","IMPRINT",FACE,{"disambiguationData":[TD([[makeQuery(id+"F5.imprint","IMPRINT",EDGE,{"disambiguationData":[TD([[subQ4,-1.0]])],"derivedFrom":subQ0}),1.0]])]});}
            var Q37;
            {var subQ0=sQuery(id+"F5.wireOp",EDGE,"E19");var subQ1=sQuery(id+"F3.wireOp",EDGE,"E5.2.0.1");var subQ2=sQuery(id+"F0.wireOp",EDGE,"E0.left");var subQ3=makeQuery(id+"FlHhq8AFgQTEit1_1.boolean.opBoolean","COPY",EDGE,{"derivedFrom":makeQuery(id+"FlHhq8AFgQTEit1_1.opExtrude","SWEPT_EDGE",EDGE,{"disambiguationData":[OSD([subQ2,sQuery(id+"F3.wireOp",EDGE,"E5.2.0.0"),subQ1])]})});var subQ4=makeQuery(id+"F5.imprint","INTERSECT",VERTEX,{"derivedFrom":[subQ3,subQ0]});Q37=makeQuery(id+"F5.imprint","IMPRINT",FACE,{"disambiguationData":[TD([[makeQuery(id+"F5.imprint","IMPRINT",EDGE,{"disambiguationData":[TD([[subQ4,-1.0]])],"derivedFrom":subQ0}),1.0]])]});}
            var Q38;
            {var subQ0=sQuery(id+"F5.wireOp",EDGE,"E19");var subQ1=sQuery(id+"F0.wireOp",EDGE,"E0.left");var subQ2=makeQuery(id+"FlHhq8AFgQTEit1_1.boolean.opBoolean","COPY",EDGE,{"derivedFrom":makeQuery(id+"FlHhq8AFgQTEit1_1.opExtrude","SWEPT_EDGE",EDGE,{"disambiguationData":[OSD([subQ1,sQuery(id+"F3.wireOp",EDGE,"E5.2.0.1"),sQuery(id+"F3.wireOp",EDGE,"E5.2.0.2")])]})});var subQ3=makeQuery(id+"F5.imprint","INTERSECT",VERTEX,{"derivedFrom":[subQ2,subQ0]});Q38=makeQuery(id+"F5.imprint","IMPRINT",FACE,{"disambiguationData":[TD([[makeQuery(id+"F5.imprint","IMPRINT",EDGE,{"disambiguationData":[TD([[subQ3,-1.0]])],"derivedFrom":subQ0}),1.0]])]});}
            var Q39;
            {var subQ0=sQuery(id+"F5.wireOp",EDGE,"E19");var subQ1=sQuery(id+"F3.wireOp",EDGE,"E5.6.0.1");var subQ2=sQuery(id+"F0.wireOp",EDGE,"E0.left");var subQ3=makeQuery(id+"FlHhq8AFgQTEit1_1.boolean.opBoolean","COPY",EDGE,{"derivedFrom":makeQuery(id+"FlHhq8AFgQTEit1_1.opExtrude","SWEPT_EDGE",EDGE,{"disambiguationData":[OSD([subQ2,sQuery(id+"F3.wireOp",EDGE,"E5.6.0.0"),subQ1])]})});var subQ4=makeQuery(id+"F5.imprint","INTERSECT",VERTEX,{"derivedFrom":[subQ3,subQ0]});Q39=makeQuery(id+"F5.imprint","IMPRINT",FACE,{"disambiguationData":[TD([[makeQuery(id+"F5.imprint","IMPRINT",EDGE,{"disambiguationData":[TD([[subQ4,-1.0]])],"derivedFrom":subQ0}),1.0]])]});}
            var Q40;
            {var subQ0=sQuery(id+"F5.wireOp",EDGE,"E19");var subQ1=sQuery(id+"F3.wireOp",EDGE,"E5.3.0.1");var subQ2=sQuery(id+"F0.wireOp",EDGE,"E0.left");var subQ3=makeQuery(id+"FlHhq8AFgQTEit1_1.boolean.opBoolean","COPY",EDGE,{"derivedFrom":makeQuery(id+"FlHhq8AFgQTEit1_1.opExtrude","SWEPT_EDGE",EDGE,{"disambiguationData":[OSD([subQ2,sQuery(id+"F3.wireOp",EDGE,"E5.3.0.0"),subQ1])]})});var subQ4=makeQuery(id+"F5.imprint","INTERSECT",VERTEX,{"derivedFrom":[subQ3,subQ0]});Q40=makeQuery(id+"F5.imprint","IMPRINT",FACE,{"disambiguationData":[TD([[makeQuery(id+"F5.imprint","IMPRINT",EDGE,{"disambiguationData":[TD([[subQ4,-1.0]])],"derivedFrom":subQ0}),1.0]])]});}
            var Q41;
            {var subQ0=sQuery(id+"F5.wireOp",EDGE,"E19");var subQ1=sQuery(id+"F0.wireOp",EDGE,"E0.left");var subQ2=makeQuery(id+"FlHhq8AFgQTEit1_1.boolean.opBoolean","COPY",EDGE,{"derivedFrom":makeQuery(id+"FlHhq8AFgQTEit1_1.opExtrude","SWEPT_EDGE",EDGE,{"disambiguationData":[OSD([subQ1,sQuery(id+"F3.wireOp",EDGE,"E3"),sQuery(id+"F3.wireOp",EDGE,"E4")])]})});var subQ3=makeQuery(id+"F5.imprint","INTERSECT",VERTEX,{"derivedFrom":[subQ2,subQ0]});Q41=makeQuery(id+"F5.imprint","IMPRINT",FACE,{"disambiguationData":[TD([[makeQuery(id+"F5.imprint","IMPRINT",EDGE,{"disambiguationData":[TD([[subQ3,-1.0]])],"derivedFrom":subQ0}),1.0]])]});}
            var Q42;
            {var subQ0=sQuery(id+"F5.wireOp",EDGE,"E19");var subQ1=sQuery(id+"F0.wireOp",EDGE,"E0.left");var subQ2=makeQuery(id+"FlHhq8AFgQTEit1_1.boolean.opBoolean","COPY",EDGE,{"derivedFrom":makeQuery(id+"FlHhq8AFgQTEit1_1.opExtrude","SWEPT_EDGE",EDGE,{"disambiguationData":[OSD([subQ1,sQuery(id+"F3.wireOp",EDGE,"E5.3.0.1"),sQuery(id+"F3.wireOp",EDGE,"E5.3.0.2")])]})});var subQ3=makeQuery(id+"F5.imprint","INTERSECT",VERTEX,{"derivedFrom":[subQ2,subQ0]});Q42=makeQuery(id+"F5.imprint","IMPRINT",FACE,{"disambiguationData":[TD([[makeQuery(id+"F5.imprint","IMPRINT",EDGE,{"disambiguationData":[TD([[subQ3,-1.0]])],"derivedFrom":subQ0}),1.0]])]});}
            var Q43;
            {var subQ0=sQuery(id+"F5.wireOp",EDGE,"E19");var subQ1=sQuery(id+"F3.wireOp",EDGE,"E5.10.0.1");var subQ2=sQuery(id+"F0.wireOp",EDGE,"E0.left");var subQ3=makeQuery(id+"FlHhq8AFgQTEit1_1.boolean.opBoolean","COPY",EDGE,{"derivedFrom":makeQuery(id+"FlHhq8AFgQTEit1_1.opExtrude","SWEPT_EDGE",EDGE,{"disambiguationData":[OSD([subQ2,sQuery(id+"F3.wireOp",EDGE,"E5.10.0.0"),subQ1])]})});var subQ4=makeQuery(id+"F5.imprint","INTERSECT",VERTEX,{"derivedFrom":[subQ3,subQ0]});Q43=makeQuery(id+"F5.imprint","IMPRINT",FACE,{"disambiguationData":[TD([[makeQuery(id+"F5.imprint","IMPRINT",EDGE,{"disambiguationData":[TD([[subQ4,-1.0]])],"derivedFrom":subQ0}),1.0]])]});}
            var Q44;
            {var subQ0=sQuery(id+"F5.wireOp",EDGE,"E19");var subQ1=sQuery(id+"F3.wireOp",EDGE,"E5.7.0.1");var subQ2=sQuery(id+"F0.wireOp",EDGE,"E0.left");var subQ3=makeQuery(id+"FlHhq8AFgQTEit1_1.boolean.opBoolean","COPY",EDGE,{"derivedFrom":makeQuery(id+"FlHhq8AFgQTEit1_1.opExtrude","SWEPT_EDGE",EDGE,{"disambiguationData":[OSD([subQ2,sQuery(id+"F3.wireOp",EDGE,"E5.7.0.0"),subQ1])]})});var subQ4=makeQuery(id+"F5.imprint","INTERSECT",VERTEX,{"derivedFrom":[subQ3,subQ0]});Q44=makeQuery(id+"F5.imprint","IMPRINT",FACE,{"disambiguationData":[TD([[makeQuery(id+"F5.imprint","IMPRINT",EDGE,{"disambiguationData":[TD([[subQ4,-1.0]])],"derivedFrom":subQ0}),1.0]])]});}
            var Q45;
            {var subQ0=sQuery(id+"F5.wireOp",EDGE,"E19");var subQ1=sQuery(id+"F0.wireOp",EDGE,"E0.left");var subQ2=makeQuery(id+"FlHhq8AFgQTEit1_1.boolean.opBoolean","COPY",EDGE,{"derivedFrom":makeQuery(id+"FlHhq8AFgQTEit1_1.opExtrude","SWEPT_EDGE",EDGE,{"disambiguationData":[OSD([subQ1,sQuery(id+"F3.wireOp",EDGE,"E5.6.0.1"),sQuery(id+"F3.wireOp",EDGE,"E5.6.0.2")])]})});var subQ3=makeQuery(id+"F5.imprint","INTERSECT",VERTEX,{"derivedFrom":[subQ2,subQ0]});Q45=makeQuery(id+"F5.imprint","IMPRINT",FACE,{"disambiguationData":[TD([[makeQuery(id+"F5.imprint","IMPRINT",EDGE,{"disambiguationData":[TD([[subQ3,-1.0]])],"derivedFrom":subQ0}),1.0]])]});}
            var Q46;
            {var subQ0=sQuery(id+"F5.wireOp",EDGE,"E19");var subQ1=sQuery(id+"F3.wireOp",EDGE,"E4");var subQ2=sQuery(id+"F0.wireOp",EDGE,"E0.left");var subQ3=makeQuery(id+"FlHhq8AFgQTEit1_1.boolean.opBoolean","COPY",EDGE,{"derivedFrom":makeQuery(id+"FlHhq8AFgQTEit1_1.opExtrude","SWEPT_EDGE",EDGE,{"disambiguationData":[OSD([subQ2,sQuery(id+"F3.wireOp",EDGE,"E2"),subQ1])]})});var subQ4=makeQuery(id+"F5.imprint","INTERSECT",VERTEX,{"derivedFrom":[subQ3,subQ0]});Q46=makeQuery(id+"F5.imprint","IMPRINT",FACE,{"disambiguationData":[TD([[makeQuery(id+"F5.imprint","IMPRINT",EDGE,{"disambiguationData":[TD([[subQ4,-1.0]])],"derivedFrom":subQ0}),1.0]])]});}
            var Q47;
            {var subQ0=sQuery(id+"F5.wireOp",EDGE,"E19");var subQ1=sQuery(id+"F5.wireOp",EDGE,"E18.bottom");var subQ2=makeQuery(id+"F5.imprint","INTERSECT",VERTEX,{"derivedFrom":[subQ1,subQ0]});Q47=makeQuery(id+"F5.imprint","IMPRINT",FACE,{"disambiguationData":[TD([[makeQuery(id+"F5.imprint","IMPRINT",EDGE,{"disambiguationData":[TD([[subQ2,1.0]])],"derivedFrom":subQ1}),-1.0]])]});}
            var Q48;
            {var subQ0=sQuery(id+"F5.wireOp",EDGE,"E16.left");var subQ1=sQuery(id+"F0.wireOp",EDGE,"E0.left");var subQ2=makeQuery(id+"FlHhq8AFgQTEit1_1.boolean.opBoolean","COPY",EDGE,{"derivedFrom":makeQuery(id+"FlHhq8AFgQTEit1_1.opExtrude","SWEPT_EDGE",EDGE,{"disambiguationData":[OSD([subQ1,sQuery(id+"F3.wireOp",EDGE,"E5.7.0.1"),sQuery(id+"F3.wireOp",EDGE,"E5.7.0.2")])]})});var subQ3=makeQuery(id+"F5.imprint","INTERSECT",VERTEX,{"derivedFrom":[subQ2,subQ0]});Q48=makeQuery(id+"F5.imprint","IMPRINT",FACE,{"disambiguationData":[TD([[makeQuery(id+"F5.imprint","IMPRINT",EDGE,{"disambiguationData":[TD([[subQ3,1.0]])],"derivedFrom":subQ0}),-1.0]])]});}
            var Q49;
            {var subQ0=sQuery(id+"F5.wireOp",EDGE,"E16.left");var subQ1=sQuery(id+"F0.wireOp",EDGE,"E0.left");var subQ2=makeQuery(id+"FlHhq8AFgQTEit1_1.boolean.opBoolean","COPY",EDGE,{"derivedFrom":makeQuery(id+"FlHhq8AFgQTEit1_1.opExtrude","SWEPT_EDGE",EDGE,{"disambiguationData":[OSD([subQ1,sQuery(id+"F3.wireOp",EDGE,"E5.2.0.1"),sQuery(id+"F3.wireOp",EDGE,"E5.2.0.2")])]})});var subQ3=makeQuery(id+"F5.imprint","INTERSECT",VERTEX,{"derivedFrom":[subQ2,subQ0]});Q49=makeQuery(id+"F5.imprint","IMPRINT",FACE,{"disambiguationData":[TD([[makeQuery(id+"F5.imprint","IMPRINT",EDGE,{"disambiguationData":[TD([[subQ3,1.0]])],"derivedFrom":subQ0}),-1.0]])]});}
            var Q50;
            {var subQ0=sQuery(id+"F5.wireOp",EDGE,"E16.left");var subQ1=sQuery(id+"F0.wireOp",EDGE,"E0.left");var subQ2=makeQuery(id+"FlHhq8AFgQTEit1_1.boolean.opBoolean","COPY",EDGE,{"derivedFrom":makeQuery(id+"FlHhq8AFgQTEit1_1.opExtrude","SWEPT_EDGE",EDGE,{"disambiguationData":[OSD([subQ1,sQuery(id+"F3.wireOp",EDGE,"E5.5.0.1"),sQuery(id+"F3.wireOp",EDGE,"E5.5.0.2")])]})});var subQ3=makeQuery(id+"F5.imprint","INTERSECT",VERTEX,{"derivedFrom":[subQ2,subQ0]});Q50=makeQuery(id+"F5.imprint","IMPRINT",FACE,{"disambiguationData":[TD([[makeQuery(id+"F5.imprint","IMPRINT",EDGE,{"disambiguationData":[TD([[subQ3,1.0]])],"derivedFrom":subQ0}),-1.0]])]});}
            var Q51;
            {var subQ0=sQuery(id+"F5.wireOp",EDGE,"E16.left");var subQ1=sQuery(id+"F3.wireOp",EDGE,"E5.7.0.1");var subQ2=sQuery(id+"F0.wireOp",EDGE,"E0.left");var subQ3=makeQuery(id+"FlHhq8AFgQTEit1_1.boolean.opBoolean","COPY",EDGE,{"derivedFrom":makeQuery(id+"FlHhq8AFgQTEit1_1.opExtrude","SWEPT_EDGE",EDGE,{"disambiguationData":[OSD([subQ2,sQuery(id+"F3.wireOp",EDGE,"E5.7.0.0"),subQ1])]})});var subQ4=makeQuery(id+"F5.imprint","INTERSECT",VERTEX,{"derivedFrom":[subQ3,subQ0]});Q51=makeQuery(id+"F5.imprint","IMPRINT",FACE,{"disambiguationData":[TD([[makeQuery(id+"F5.imprint","IMPRINT",EDGE,{"disambiguationData":[TD([[subQ4,1.0]])],"derivedFrom":subQ0}),-1.0]])]});}
            var Q52;
            {var subQ0=sQuery(id+"F5.wireOp",EDGE,"E16.left");var subQ1=sQuery(id+"F3.wireOp",EDGE,"E5.1.0.1");var subQ2=sQuery(id+"F0.wireOp",EDGE,"E0.left");var subQ3=makeQuery(id+"FlHhq8AFgQTEit1_1.boolean.opBoolean","COPY",EDGE,{"derivedFrom":makeQuery(id+"FlHhq8AFgQTEit1_1.opExtrude","SWEPT_EDGE",EDGE,{"disambiguationData":[OSD([subQ2,sQuery(id+"F3.wireOp",EDGE,"E5.1.0.0"),subQ1])]})});var subQ4=makeQuery(id+"F5.imprint","INTERSECT",VERTEX,{"derivedFrom":[subQ3,subQ0]});Q52=makeQuery(id+"F5.imprint","IMPRINT",FACE,{"disambiguationData":[TD([[makeQuery(id+"F5.imprint","IMPRINT",EDGE,{"disambiguationData":[TD([[subQ4,1.0]])],"derivedFrom":subQ0}),-1.0]])]});}
            var Q53;
            {var subQ0=sQuery(id+"F5.wireOp",EDGE,"E16.left");var subQ1=sQuery(id+"F0.wireOp",EDGE,"E0.left");var subQ2=makeQuery(id+"FlHhq8AFgQTEit1_1.boolean.opBoolean","COPY",EDGE,{"derivedFrom":makeQuery(id+"FlHhq8AFgQTEit1_1.opExtrude","SWEPT_EDGE",EDGE,{"disambiguationData":[OSD([subQ1,sQuery(id+"F3.wireOp",EDGE,"E5.9.0.1"),sQuery(id+"F3.wireOp",EDGE,"E5.9.0.2")])]})});var subQ3=makeQuery(id+"F5.imprint","INTERSECT",VERTEX,{"derivedFrom":[subQ2,subQ0]});Q53=makeQuery(id+"F5.imprint","IMPRINT",FACE,{"disambiguationData":[TD([[makeQuery(id+"F5.imprint","IMPRINT",EDGE,{"disambiguationData":[TD([[subQ3,1.0]])],"derivedFrom":subQ0}),-1.0]])]});}
            var Q54;
            {var subQ0=sQuery(id+"F5.wireOp",EDGE,"E16.left");var subQ1=sQuery(id+"F0.wireOp",EDGE,"E0.left");var subQ2=makeQuery(id+"FlHhq8AFgQTEit1_1.boolean.opBoolean","COPY",EDGE,{"derivedFrom":makeQuery(id+"FlHhq8AFgQTEit1_1.opExtrude","SWEPT_EDGE",EDGE,{"disambiguationData":[OSD([subQ1,sQuery(id+"F3.wireOp",EDGE,"E5.1.0.1"),sQuery(id+"F3.wireOp",EDGE,"E5.1.0.2")])]})});var subQ3=makeQuery(id+"F5.imprint","INTERSECT",VERTEX,{"derivedFrom":[subQ2,subQ0]});Q54=makeQuery(id+"F5.imprint","IMPRINT",FACE,{"disambiguationData":[TD([[makeQuery(id+"F5.imprint","IMPRINT",EDGE,{"disambiguationData":[TD([[subQ3,1.0]])],"derivedFrom":subQ0}),-1.0]])]});}
            var Q55;
            {var subQ0=sQuery(id+"F5.wireOp",EDGE,"E16.top");Q55=makeQuery(id+"F5.imprint","IMPRINT",FACE,{"disambiguationData":[TD([[makeQuery(id+"F5.imprint","IMPRINT",EDGE,{"derivedFrom":subQ0}),-1.0]])]});}
            var Q56;
            {var subQ0=sQuery(id+"F5.wireOp",EDGE,"E16.left");var subQ1=sQuery(id+"F0.wireOp",EDGE,"E0.left");var subQ2=makeQuery(id+"FlHhq8AFgQTEit1_1.boolean.opBoolean","COPY",EDGE,{"derivedFrom":makeQuery(id+"FlHhq8AFgQTEit1_1.opExtrude","SWEPT_EDGE",EDGE,{"disambiguationData":[OSD([subQ1,sQuery(id+"F3.wireOp",EDGE,"E5.10.0.1"),sQuery(id+"F3.wireOp",EDGE,"E5.10.0.2")])]})});var subQ3=makeQuery(id+"F5.imprint","INTERSECT",VERTEX,{"derivedFrom":[subQ2,subQ0]});Q56=makeQuery(id+"F5.imprint","IMPRINT",FACE,{"disambiguationData":[TD([[makeQuery(id+"F5.imprint","IMPRINT",EDGE,{"disambiguationData":[TD([[subQ3,1.0]])],"derivedFrom":subQ0}),-1.0]])]});}
            var Q57;
            {var subQ0=sQuery(id+"F5.wireOp",EDGE,"E16.left");var subQ1=sQuery(id+"F3.wireOp",EDGE,"E5.10.0.1");var subQ2=sQuery(id+"F0.wireOp",EDGE,"E0.left");var subQ3=makeQuery(id+"FlHhq8AFgQTEit1_1.boolean.opBoolean","COPY",EDGE,{"derivedFrom":makeQuery(id+"FlHhq8AFgQTEit1_1.opExtrude","SWEPT_EDGE",EDGE,{"disambiguationData":[OSD([subQ2,sQuery(id+"F3.wireOp",EDGE,"E5.10.0.0"),subQ1])]})});var subQ4=makeQuery(id+"F5.imprint","INTERSECT",VERTEX,{"derivedFrom":[subQ3,subQ0]});Q57=makeQuery(id+"F5.imprint","IMPRINT",FACE,{"disambiguationData":[TD([[makeQuery(id+"F5.imprint","IMPRINT",EDGE,{"disambiguationData":[TD([[subQ4,1.0]])],"derivedFrom":subQ0}),-1.0]])]});}
            var Q58;
            {var subQ0=sQuery(id+"F5.wireOp",EDGE,"E16.left");var subQ1=sQuery(id+"F3.wireOp",EDGE,"E5.3.0.1");var subQ2=sQuery(id+"F0.wireOp",EDGE,"E0.left");var subQ3=makeQuery(id+"FlHhq8AFgQTEit1_1.boolean.opBoolean","COPY",EDGE,{"derivedFrom":makeQuery(id+"FlHhq8AFgQTEit1_1.opExtrude","SWEPT_EDGE",EDGE,{"disambiguationData":[OSD([subQ2,sQuery(id+"F3.wireOp",EDGE,"E5.3.0.0"),subQ1])]})});var subQ4=makeQuery(id+"F5.imprint","INTERSECT",VERTEX,{"derivedFrom":[subQ3,subQ0]});Q58=makeQuery(id+"F5.imprint","IMPRINT",FACE,{"disambiguationData":[TD([[makeQuery(id+"F5.imprint","IMPRINT",EDGE,{"disambiguationData":[TD([[subQ4,1.0]])],"derivedFrom":subQ0}),-1.0]])]});}
            var Q59;
            {var subQ0=sQuery(id+"F5.wireOp",EDGE,"E16.left");var subQ1=sQuery(id+"F0.wireOp",EDGE,"E0.left");var subQ2=makeQuery(id+"FlHhq8AFgQTEit1_1.boolean.opBoolean","COPY",EDGE,{"derivedFrom":makeQuery(id+"FlHhq8AFgQTEit1_1.opExtrude","SWEPT_EDGE",EDGE,{"disambiguationData":[OSD([subQ1,sQuery(id+"F3.wireOp",EDGE,"E3"),sQuery(id+"F3.wireOp",EDGE,"E4")])]})});var subQ3=makeQuery(id+"F5.imprint","INTERSECT",VERTEX,{"derivedFrom":[subQ2,subQ0]});Q59=makeQuery(id+"F5.imprint","IMPRINT",FACE,{"disambiguationData":[TD([[makeQuery(id+"F5.imprint","IMPRINT",EDGE,{"disambiguationData":[TD([[subQ3,1.0]])],"derivedFrom":subQ0}),-1.0]])]});}
            var Q60;
            {var subQ0=sQuery(id+"F5.wireOp",EDGE,"E16.left");var subQ1=sQuery(id+"F3.wireOp",EDGE,"E5.4.0.1");var subQ2=sQuery(id+"F0.wireOp",EDGE,"E0.left");var subQ3=makeQuery(id+"FlHhq8AFgQTEit1_1.boolean.opBoolean","COPY",EDGE,{"derivedFrom":makeQuery(id+"FlHhq8AFgQTEit1_1.opExtrude","SWEPT_EDGE",EDGE,{"disambiguationData":[OSD([subQ2,sQuery(id+"F3.wireOp",EDGE,"E5.4.0.0"),subQ1])]})});var subQ4=makeQuery(id+"F5.imprint","INTERSECT",VERTEX,{"derivedFrom":[subQ3,subQ0]});Q60=makeQuery(id+"F5.imprint","IMPRINT",FACE,{"disambiguationData":[TD([[makeQuery(id+"F5.imprint","IMPRINT",EDGE,{"disambiguationData":[TD([[subQ4,1.0]])],"derivedFrom":subQ0}),-1.0]])]});}
            var Q61;
            {var subQ0=sQuery(id+"F5.wireOp",EDGE,"E16.left");var subQ1=sQuery(id+"F3.wireOp",EDGE,"E5.6.0.1");var subQ2=sQuery(id+"F0.wireOp",EDGE,"E0.left");var subQ3=makeQuery(id+"FlHhq8AFgQTEit1_1.boolean.opBoolean","COPY",EDGE,{"derivedFrom":makeQuery(id+"FlHhq8AFgQTEit1_1.opExtrude","SWEPT_EDGE",EDGE,{"disambiguationData":[OSD([subQ2,sQuery(id+"F3.wireOp",EDGE,"E5.6.0.0"),subQ1])]})});var subQ4=makeQuery(id+"F5.imprint","INTERSECT",VERTEX,{"derivedFrom":[subQ3,subQ0]});Q61=makeQuery(id+"F5.imprint","IMPRINT",FACE,{"disambiguationData":[TD([[makeQuery(id+"F5.imprint","IMPRINT",EDGE,{"disambiguationData":[TD([[subQ4,1.0]])],"derivedFrom":subQ0}),-1.0]])]});}
            var Q62;
            {var subQ0=sQuery(id+"F5.wireOp",EDGE,"E16.left");var subQ1=sQuery(id+"F0.wireOp",EDGE,"E0.left");var subQ2=makeQuery(id+"FlHhq8AFgQTEit1_1.boolean.opBoolean","COPY",EDGE,{"derivedFrom":makeQuery(id+"FlHhq8AFgQTEit1_1.opExtrude","SWEPT_EDGE",EDGE,{"disambiguationData":[OSD([subQ1,sQuery(id+"F3.wireOp",EDGE,"E5.4.0.1"),sQuery(id+"F3.wireOp",EDGE,"E5.4.0.2")])]})});var subQ3=makeQuery(id+"F5.imprint","INTERSECT",VERTEX,{"derivedFrom":[subQ2,subQ0]});Q62=makeQuery(id+"F5.imprint","IMPRINT",FACE,{"disambiguationData":[TD([[makeQuery(id+"F5.imprint","IMPRINT",EDGE,{"disambiguationData":[TD([[subQ3,1.0]])],"derivedFrom":subQ0}),-1.0]])]});}
            var Q63;
            {var subQ0=sQuery(id+"F5.wireOp",EDGE,"E16.left");var subQ1=sQuery(id+"F0.wireOp",EDGE,"E0.left");var subQ2=makeQuery(id+"FlHhq8AFgQTEit1_1.boolean.opBoolean","COPY",EDGE,{"derivedFrom":makeQuery(id+"FlHhq8AFgQTEit1_1.opExtrude","SWEPT_EDGE",EDGE,{"disambiguationData":[OSD([subQ1,sQuery(id+"F3.wireOp",EDGE,"E5.8.0.1"),sQuery(id+"F3.wireOp",EDGE,"E5.8.0.2")])]})});var subQ3=makeQuery(id+"F5.imprint","INTERSECT",VERTEX,{"derivedFrom":[subQ2,subQ0]});Q63=makeQuery(id+"F5.imprint","IMPRINT",FACE,{"disambiguationData":[TD([[makeQuery(id+"F5.imprint","IMPRINT",EDGE,{"disambiguationData":[TD([[subQ3,1.0]])],"derivedFrom":subQ0}),-1.0]])]});}
            var Q64;
            {var subQ0=sQuery(id+"F5.wireOp",EDGE,"E16.left");var subQ1=sQuery(id+"F0.wireOp",EDGE,"E0.left");var subQ2=makeQuery(id+"FlHhq8AFgQTEit1_1.boolean.opBoolean","COPY",EDGE,{"derivedFrom":makeQuery(id+"FlHhq8AFgQTEit1_1.opExtrude","SWEPT_EDGE",EDGE,{"disambiguationData":[OSD([subQ1,sQuery(id+"F3.wireOp",EDGE,"E5.6.0.1"),sQuery(id+"F3.wireOp",EDGE,"E5.6.0.2")])]})});var subQ3=makeQuery(id+"F5.imprint","INTERSECT",VERTEX,{"derivedFrom":[subQ2,subQ0]});Q64=makeQuery(id+"F5.imprint","IMPRINT",FACE,{"disambiguationData":[TD([[makeQuery(id+"F5.imprint","IMPRINT",EDGE,{"disambiguationData":[TD([[subQ3,1.0]])],"derivedFrom":subQ0}),-1.0]])]});}
            var Q65;
            {var subQ0=sQuery(id+"F5.wireOp",EDGE,"E16.left");var subQ1=sQuery(id+"F3.wireOp",EDGE,"E5.2.0.1");var subQ2=sQuery(id+"F0.wireOp",EDGE,"E0.left");var subQ3=makeQuery(id+"FlHhq8AFgQTEit1_1.boolean.opBoolean","COPY",EDGE,{"derivedFrom":makeQuery(id+"FlHhq8AFgQTEit1_1.opExtrude","SWEPT_EDGE",EDGE,{"disambiguationData":[OSD([subQ2,sQuery(id+"F3.wireOp",EDGE,"E5.2.0.0"),subQ1])]})});var subQ4=makeQuery(id+"F5.imprint","INTERSECT",VERTEX,{"derivedFrom":[subQ3,subQ0]});Q65=makeQuery(id+"F5.imprint","IMPRINT",FACE,{"disambiguationData":[TD([[makeQuery(id+"F5.imprint","IMPRINT",EDGE,{"disambiguationData":[TD([[subQ4,1.0]])],"derivedFrom":subQ0}),-1.0]])]});}
            var Q66;
            {var subQ0=sQuery(id+"F5.wireOp",EDGE,"E16.left");var subQ1=sQuery(id+"F0.wireOp",EDGE,"E0.left");var subQ2=makeQuery(id+"FlHhq8AFgQTEit1_1.boolean.opBoolean","COPY",EDGE,{"derivedFrom":makeQuery(id+"FlHhq8AFgQTEit1_1.opExtrude","SWEPT_EDGE",EDGE,{"disambiguationData":[OSD([subQ1,sQuery(id+"F3.wireOp",EDGE,"E5.3.0.1"),sQuery(id+"F3.wireOp",EDGE,"E5.3.0.2")])]})});var subQ3=makeQuery(id+"F5.imprint","INTERSECT",VERTEX,{"derivedFrom":[subQ2,subQ0]});Q66=makeQuery(id+"F5.imprint","IMPRINT",FACE,{"disambiguationData":[TD([[makeQuery(id+"F5.imprint","IMPRINT",EDGE,{"disambiguationData":[TD([[subQ3,1.0]])],"derivedFrom":subQ0}),-1.0]])]});}
            var Q67;
            {var subQ0=sQuery(id+"F5.wireOp",EDGE,"E16.left");var subQ1=sQuery(id+"F3.wireOp",EDGE,"E5.9.0.1");var subQ2=sQuery(id+"F0.wireOp",EDGE,"E0.left");var subQ3=makeQuery(id+"FlHhq8AFgQTEit1_1.boolean.opBoolean","COPY",EDGE,{"derivedFrom":makeQuery(id+"FlHhq8AFgQTEit1_1.opExtrude","SWEPT_EDGE",EDGE,{"disambiguationData":[OSD([subQ2,sQuery(id+"F3.wireOp",EDGE,"E5.9.0.0"),subQ1])]})});var subQ4=makeQuery(id+"F5.imprint","INTERSECT",VERTEX,{"derivedFrom":[subQ3,subQ0]});Q67=makeQuery(id+"F5.imprint","IMPRINT",FACE,{"disambiguationData":[TD([[makeQuery(id+"F5.imprint","IMPRINT",EDGE,{"disambiguationData":[TD([[subQ4,1.0]])],"derivedFrom":subQ0}),-1.0]])]});}
            var Q68;
            {var subQ0=sQuery(id+"F5.wireOp",EDGE,"E16.left");var subQ1=sQuery(id+"F3.wireOp",EDGE,"E4");var subQ2=sQuery(id+"F0.wireOp",EDGE,"E0.left");var subQ3=makeQuery(id+"FlHhq8AFgQTEit1_1.boolean.opBoolean","COPY",EDGE,{"derivedFrom":makeQuery(id+"FlHhq8AFgQTEit1_1.opExtrude","SWEPT_EDGE",EDGE,{"disambiguationData":[OSD([subQ2,sQuery(id+"F3.wireOp",EDGE,"E2"),subQ1])]})});var subQ4=makeQuery(id+"F5.imprint","INTERSECT",VERTEX,{"derivedFrom":[subQ3,subQ0]});Q68=makeQuery(id+"F5.imprint","IMPRINT",FACE,{"disambiguationData":[TD([[makeQuery(id+"F5.imprint","IMPRINT",EDGE,{"disambiguationData":[TD([[subQ4,1.0]])],"derivedFrom":subQ0}),-1.0]])]});}
            var Q69;
            {var subQ0=sQuery(id+"F5.wireOp",EDGE,"E16.left");var subQ1=sQuery(id+"F3.wireOp",EDGE,"E5.5.0.1");var subQ2=sQuery(id+"F0.wireOp",EDGE,"E0.left");var subQ3=makeQuery(id+"FlHhq8AFgQTEit1_1.boolean.opBoolean","COPY",EDGE,{"derivedFrom":makeQuery(id+"FlHhq8AFgQTEit1_1.opExtrude","SWEPT_EDGE",EDGE,{"disambiguationData":[OSD([subQ2,sQuery(id+"F3.wireOp",EDGE,"E5.5.0.0"),subQ1])]})});var subQ4=makeQuery(id+"F5.imprint","INTERSECT",VERTEX,{"derivedFrom":[subQ3,subQ0]});Q69=makeQuery(id+"F5.imprint","IMPRINT",FACE,{"disambiguationData":[TD([[makeQuery(id+"F5.imprint","IMPRINT",EDGE,{"disambiguationData":[TD([[subQ4,1.0]])],"derivedFrom":subQ0}),-1.0]])]});}
            var Q70;
            {var subQ0=sQuery(id+"F5.wireOp",EDGE,"E16.left");var subQ3=sQuery(id+"F5.wireOp",EDGE,"E18.bottom");var subQ4=makeQuery(id+"F5.imprint","INTERSECT",VERTEX,{"derivedFrom":[subQ0,subQ3]});Q70=makeQuery(id+"F5.imprint","IMPRINT",FACE,{"disambiguationData":[TD([[makeQuery(id+"F5.imprint","IMPRINT",EDGE,{"disambiguationData":[TD([[subQ4,1.0]])],"derivedFrom":subQ3}),-1.0]])]});}
            var Q71;
            {var subQ0=sQuery(id+"F5.wireOp",EDGE,"E16.left");var subQ1=sQuery(id+"F3.wireOp",EDGE,"E5.8.0.1");var subQ2=sQuery(id+"F0.wireOp",EDGE,"E0.left");var subQ3=makeQuery(id+"FlHhq8AFgQTEit1_1.boolean.opBoolean","COPY",EDGE,{"derivedFrom":makeQuery(id+"FlHhq8AFgQTEit1_1.opExtrude","SWEPT_EDGE",EDGE,{"disambiguationData":[OSD([subQ2,sQuery(id+"F3.wireOp",EDGE,"E5.8.0.0"),subQ1])]})});var subQ4=makeQuery(id+"F5.imprint","INTERSECT",VERTEX,{"derivedFrom":[subQ3,subQ0]});Q71=makeQuery(id+"F5.imprint","IMPRINT",FACE,{"disambiguationData":[TD([[makeQuery(id+"F5.imprint","IMPRINT",EDGE,{"disambiguationData":[TD([[subQ4,1.0]])],"derivedFrom":subQ0}),-1.0]])]});}
            var Q72;
            {var subQ0=sQuery(id+"F5.wireOp",EDGE,"E14.left");var subQ1=sQuery(id+"F0.wireOp",EDGE,"E0.left");var subQ2=makeQuery(id+"FlHhq8AFgQTEit1_1.boolean.opBoolean","COPY",EDGE,{"derivedFrom":makeQuery(id+"FlHhq8AFgQTEit1_1.opExtrude","SWEPT_EDGE",EDGE,{"disambiguationData":[OSD([subQ1,sQuery(id+"F3.wireOp",EDGE,"E5.5.0.0"),sQuery(id+"F3.wireOp",EDGE,"E5.5.0.1")])]})});var subQ3=makeQuery(id+"F5.imprint","INTERSECT",VERTEX,{"derivedFrom":[subQ2,subQ0]});Q72=makeQuery(id+"F5.imprint","IMPRINT",FACE,{"disambiguationData":[TD([[makeQuery(id+"F5.imprint","IMPRINT",EDGE,{"disambiguationData":[TD([[subQ3,-1.0]])],"derivedFrom":subQ0}),-1.0]])]});}
            var Q73;
            {var subQ0=sQuery(id+"F5.wireOp",EDGE,"E14.left");var subQ1=sQuery(id+"F0.wireOp",EDGE,"E0.left");var subQ2=makeQuery(id+"FlHhq8AFgQTEit1_1.boolean.opBoolean","COPY",EDGE,{"derivedFrom":makeQuery(id+"FlHhq8AFgQTEit1_1.opExtrude","SWEPT_EDGE",EDGE,{"disambiguationData":[OSD([subQ1,sQuery(id+"F3.wireOp",EDGE,"E5.4.0.0"),sQuery(id+"F3.wireOp",EDGE,"E5.4.0.1")])]})});var subQ3=makeQuery(id+"F5.imprint","INTERSECT",VERTEX,{"derivedFrom":[subQ2,subQ0]});Q73=makeQuery(id+"F5.imprint","IMPRINT",FACE,{"disambiguationData":[TD([[makeQuery(id+"F5.imprint","IMPRINT",EDGE,{"disambiguationData":[TD([[subQ3,-1.0]])],"derivedFrom":subQ0}),-1.0]])]});}
            var Q74;
            {var subQ0=sQuery(id+"F5.wireOp",EDGE,"E14.left");var subQ1=sQuery(id+"F3.wireOp",EDGE,"E5.8.0.1");var subQ2=sQuery(id+"F0.wireOp",EDGE,"E0.left");var subQ3=makeQuery(id+"FlHhq8AFgQTEit1_1.boolean.opBoolean","COPY",EDGE,{"derivedFrom":makeQuery(id+"FlHhq8AFgQTEit1_1.opExtrude","SWEPT_EDGE",EDGE,{"disambiguationData":[OSD([subQ2,subQ1,sQuery(id+"F3.wireOp",EDGE,"E5.8.0.2")])]})});var subQ4=makeQuery(id+"F5.imprint","INTERSECT",VERTEX,{"derivedFrom":[subQ3,subQ0]});Q74=makeQuery(id+"F5.imprint","IMPRINT",FACE,{"disambiguationData":[TD([[makeQuery(id+"F5.imprint","IMPRINT",EDGE,{"disambiguationData":[TD([[subQ4,-1.0]])],"derivedFrom":subQ0}),-1.0]])]});}
            var Q75;
            {var subQ0=sQuery(id+"F5.wireOp",EDGE,"E14.left");var subQ1=sQuery(id+"F0.wireOp",EDGE,"E0.left");var subQ2=makeQuery(id+"FlHhq8AFgQTEit1_1.boolean.opBoolean","COPY",EDGE,{"derivedFrom":makeQuery(id+"FlHhq8AFgQTEit1_1.opExtrude","SWEPT_EDGE",EDGE,{"disambiguationData":[OSD([subQ1,sQuery(id+"F3.wireOp",EDGE,"E5.3.0.0"),sQuery(id+"F3.wireOp",EDGE,"E5.3.0.1")])]})});var subQ3=makeQuery(id+"F5.imprint","INTERSECT",VERTEX,{"derivedFrom":[subQ2,subQ0]});Q75=makeQuery(id+"F5.imprint","IMPRINT",FACE,{"disambiguationData":[TD([[makeQuery(id+"F5.imprint","IMPRINT",EDGE,{"disambiguationData":[TD([[subQ3,-1.0]])],"derivedFrom":subQ0}),-1.0]])]});}
            var Q76;
            {var subQ0=sQuery(id+"F5.wireOp",EDGE,"E14.left");var subQ1=sQuery(id+"F3.wireOp",EDGE,"E4");var subQ2=sQuery(id+"F0.wireOp",EDGE,"E0.left");var subQ3=makeQuery(id+"FlHhq8AFgQTEit1_1.boolean.opBoolean","COPY",EDGE,{"derivedFrom":makeQuery(id+"FlHhq8AFgQTEit1_1.opExtrude","SWEPT_EDGE",EDGE,{"disambiguationData":[OSD([subQ2,sQuery(id+"F3.wireOp",EDGE,"E3"),subQ1])]})});var subQ4=makeQuery(id+"F5.imprint","INTERSECT",VERTEX,{"derivedFrom":[subQ3,subQ0]});Q76=makeQuery(id+"F5.imprint","IMPRINT",FACE,{"disambiguationData":[TD([[makeQuery(id+"F5.imprint","IMPRINT",EDGE,{"disambiguationData":[TD([[subQ4,-1.0]])],"derivedFrom":subQ0}),-1.0]])]});}
            var Q77;
            {var subQ0=sQuery(id+"F5.wireOp",EDGE,"E14.left");var subQ1=sQuery(id+"F0.wireOp",EDGE,"E0.left");var subQ2=makeQuery(id+"FlHhq8AFgQTEit1_1.boolean.opBoolean","COPY",EDGE,{"derivedFrom":makeQuery(id+"FlHhq8AFgQTEit1_1.opExtrude","SWEPT_EDGE",EDGE,{"disambiguationData":[OSD([subQ1,sQuery(id+"F3.wireOp",EDGE,"E5.7.0.0"),sQuery(id+"F3.wireOp",EDGE,"E5.7.0.1")])]})});var subQ3=makeQuery(id+"F5.imprint","INTERSECT",VERTEX,{"derivedFrom":[subQ2,subQ0]});Q77=makeQuery(id+"F5.imprint","IMPRINT",FACE,{"disambiguationData":[TD([[makeQuery(id+"F5.imprint","IMPRINT",EDGE,{"disambiguationData":[TD([[subQ3,-1.0]])],"derivedFrom":subQ0}),-1.0]])]});}
            var Q78;
            {var subQ0=sQuery(id+"F5.wireOp",EDGE,"E14.left");var subQ1=sQuery(id+"F0.wireOp",EDGE,"E0.left");var subQ2=makeQuery(id+"FlHhq8AFgQTEit1_1.boolean.opBoolean","COPY",EDGE,{"derivedFrom":makeQuery(id+"FlHhq8AFgQTEit1_1.opExtrude","SWEPT_EDGE",EDGE,{"disambiguationData":[OSD([subQ1,sQuery(id+"F3.wireOp",EDGE,"E5.8.0.0"),sQuery(id+"F3.wireOp",EDGE,"E5.8.0.1")])]})});var subQ3=makeQuery(id+"F5.imprint","INTERSECT",VERTEX,{"derivedFrom":[subQ2,subQ0]});Q78=makeQuery(id+"F5.imprint","IMPRINT",FACE,{"disambiguationData":[TD([[makeQuery(id+"F5.imprint","IMPRINT",EDGE,{"disambiguationData":[TD([[subQ3,-1.0]])],"derivedFrom":subQ0}),-1.0]])]});}
            var Q79;
            {var subQ0=sQuery(id+"F5.wireOp",EDGE,"E14.left");var subQ1=sQuery(id+"F3.wireOp",EDGE,"E5.4.0.1");var subQ2=sQuery(id+"F0.wireOp",EDGE,"E0.left");var subQ3=makeQuery(id+"FlHhq8AFgQTEit1_1.boolean.opBoolean","COPY",EDGE,{"derivedFrom":makeQuery(id+"FlHhq8AFgQTEit1_1.opExtrude","SWEPT_EDGE",EDGE,{"disambiguationData":[OSD([subQ2,subQ1,sQuery(id+"F3.wireOp",EDGE,"E5.4.0.2")])]})});var subQ4=makeQuery(id+"F5.imprint","INTERSECT",VERTEX,{"derivedFrom":[subQ3,subQ0]});Q79=makeQuery(id+"F5.imprint","IMPRINT",FACE,{"disambiguationData":[TD([[makeQuery(id+"F5.imprint","IMPRINT",EDGE,{"disambiguationData":[TD([[subQ4,-1.0]])],"derivedFrom":subQ0}),-1.0]])]});}
            var Q80;
            {var subQ0=sQuery(id+"F5.wireOp",EDGE,"E14.left");var subQ1=sQuery(id+"F3.wireOp",EDGE,"E5.3.0.1");var subQ2=sQuery(id+"F0.wireOp",EDGE,"E0.left");var subQ3=makeQuery(id+"FlHhq8AFgQTEit1_1.boolean.opBoolean","COPY",EDGE,{"derivedFrom":makeQuery(id+"FlHhq8AFgQTEit1_1.opExtrude","SWEPT_EDGE",EDGE,{"disambiguationData":[OSD([subQ2,subQ1,sQuery(id+"F3.wireOp",EDGE,"E5.3.0.2")])]})});var subQ4=makeQuery(id+"F5.imprint","INTERSECT",VERTEX,{"derivedFrom":[subQ3,subQ0]});Q80=makeQuery(id+"F5.imprint","IMPRINT",FACE,{"disambiguationData":[TD([[makeQuery(id+"F5.imprint","IMPRINT",EDGE,{"disambiguationData":[TD([[subQ4,-1.0]])],"derivedFrom":subQ0}),-1.0]])]});}
            var Q81;
            {var subQ0=sQuery(id+"F5.wireOp",EDGE,"E14.left");var subQ1=sQuery(id+"F0.wireOp",EDGE,"E0.left");var subQ2=makeQuery(id+"FlHhq8AFgQTEit1_1.boolean.opBoolean","COPY",EDGE,{"derivedFrom":makeQuery(id+"FlHhq8AFgQTEit1_1.opExtrude","SWEPT_EDGE",EDGE,{"disambiguationData":[OSD([subQ1,sQuery(id+"F3.wireOp",EDGE,"E5.6.0.0"),sQuery(id+"F3.wireOp",EDGE,"E5.6.0.1")])]})});var subQ3=makeQuery(id+"F5.imprint","INTERSECT",VERTEX,{"derivedFrom":[subQ2,subQ0]});Q81=makeQuery(id+"F5.imprint","IMPRINT",FACE,{"disambiguationData":[TD([[makeQuery(id+"F5.imprint","IMPRINT",EDGE,{"disambiguationData":[TD([[subQ3,-1.0]])],"derivedFrom":subQ0}),-1.0]])]});}
            var Q82;
            {var subQ0=sQuery(id+"F5.wireOp",EDGE,"E14.left");var subQ1=sQuery(id+"F3.wireOp",EDGE,"E5.7.0.1");var subQ2=sQuery(id+"F0.wireOp",EDGE,"E0.left");var subQ3=makeQuery(id+"FlHhq8AFgQTEit1_1.boolean.opBoolean","COPY",EDGE,{"derivedFrom":makeQuery(id+"FlHhq8AFgQTEit1_1.opExtrude","SWEPT_EDGE",EDGE,{"disambiguationData":[OSD([subQ2,subQ1,sQuery(id+"F3.wireOp",EDGE,"E5.7.0.2")])]})});var subQ4=makeQuery(id+"F5.imprint","INTERSECT",VERTEX,{"derivedFrom":[subQ3,subQ0]});Q82=makeQuery(id+"F5.imprint","IMPRINT",FACE,{"disambiguationData":[TD([[makeQuery(id+"F5.imprint","IMPRINT",EDGE,{"disambiguationData":[TD([[subQ4,-1.0]])],"derivedFrom":subQ0}),-1.0]])]});}
            var Q83;
            {var subQ0=sQuery(id+"F5.wireOp",EDGE,"E14.left");var subQ1=sQuery(id+"F3.wireOp",EDGE,"E5.5.0.1");var subQ2=sQuery(id+"F0.wireOp",EDGE,"E0.left");var subQ3=makeQuery(id+"FlHhq8AFgQTEit1_1.boolean.opBoolean","COPY",EDGE,{"derivedFrom":makeQuery(id+"FlHhq8AFgQTEit1_1.opExtrude","SWEPT_EDGE",EDGE,{"disambiguationData":[OSD([subQ2,subQ1,sQuery(id+"F3.wireOp",EDGE,"E5.5.0.2")])]})});var subQ4=makeQuery(id+"F5.imprint","INTERSECT",VERTEX,{"derivedFrom":[subQ3,subQ0]});Q83=makeQuery(id+"F5.imprint","IMPRINT",FACE,{"disambiguationData":[TD([[makeQuery(id+"F5.imprint","IMPRINT",EDGE,{"disambiguationData":[TD([[subQ4,-1.0]])],"derivedFrom":subQ0}),-1.0]])]});}
            var Q84;
            {var subQ0=sQuery(id+"F5.wireOp",EDGE,"E14.top");Q84=makeQuery(id+"F5.imprint","IMPRINT",FACE,{"disambiguationData":[TD([[makeQuery(id+"F5.imprint","IMPRINT",EDGE,{"derivedFrom":subQ0}),-1.0]])]});}
            var Q85;
            {var subQ0=sQuery(id+"F5.wireOp",EDGE,"E14.left");var subQ1=sQuery(id+"F0.wireOp",EDGE,"E0.left");var subQ2=makeQuery(id+"FlHhq8AFgQTEit1_1.boolean.opBoolean","COPY",EDGE,{"derivedFrom":makeQuery(id+"FlHhq8AFgQTEit1_1.opExtrude","SWEPT_EDGE",EDGE,{"disambiguationData":[OSD([subQ1,sQuery(id+"F3.wireOp",EDGE,"E5.1.0.0"),sQuery(id+"F3.wireOp",EDGE,"E5.1.0.1")])]})});var subQ3=makeQuery(id+"F5.imprint","INTERSECT",VERTEX,{"derivedFrom":[subQ2,subQ0]});Q85=makeQuery(id+"F5.imprint","IMPRINT",FACE,{"disambiguationData":[TD([[makeQuery(id+"F5.imprint","IMPRINT",EDGE,{"disambiguationData":[TD([[subQ3,-1.0]])],"derivedFrom":subQ0}),-1.0]])]});}
            var Q86;
            {var subQ0=sQuery(id+"F5.wireOp",EDGE,"E14.left");var subQ1=sQuery(id+"F3.wireOp",EDGE,"E5.2.0.1");var subQ2=sQuery(id+"F0.wireOp",EDGE,"E0.left");var subQ3=makeQuery(id+"FlHhq8AFgQTEit1_1.boolean.opBoolean","COPY",EDGE,{"derivedFrom":makeQuery(id+"FlHhq8AFgQTEit1_1.opExtrude","SWEPT_EDGE",EDGE,{"disambiguationData":[OSD([subQ2,subQ1,sQuery(id+"F3.wireOp",EDGE,"E5.2.0.2")])]})});var subQ4=makeQuery(id+"F5.imprint","INTERSECT",VERTEX,{"derivedFrom":[subQ3,subQ0]});Q86=makeQuery(id+"F5.imprint","IMPRINT",FACE,{"disambiguationData":[TD([[makeQuery(id+"F5.imprint","IMPRINT",EDGE,{"disambiguationData":[TD([[subQ4,-1.0]])],"derivedFrom":subQ0}),-1.0]])]});}
            var Q87;
            {var subQ0=sQuery(id+"F5.wireOp",EDGE,"E14.left");var subQ1=sQuery(id+"F3.wireOp",EDGE,"E5.6.0.1");var subQ2=sQuery(id+"F0.wireOp",EDGE,"E0.left");var subQ3=makeQuery(id+"FlHhq8AFgQTEit1_1.boolean.opBoolean","COPY",EDGE,{"derivedFrom":makeQuery(id+"FlHhq8AFgQTEit1_1.opExtrude","SWEPT_EDGE",EDGE,{"disambiguationData":[OSD([subQ2,subQ1,sQuery(id+"F3.wireOp",EDGE,"E5.6.0.2")])]})});var subQ4=makeQuery(id+"F5.imprint","INTERSECT",VERTEX,{"derivedFrom":[subQ3,subQ0]});Q87=makeQuery(id+"F5.imprint","IMPRINT",FACE,{"disambiguationData":[TD([[makeQuery(id+"F5.imprint","IMPRINT",EDGE,{"disambiguationData":[TD([[subQ4,-1.0]])],"derivedFrom":subQ0}),-1.0]])]});}
            var Q88;
            {var subQ0=sQuery(id+"F5.wireOp",EDGE,"E14.left");var subQ1=sQuery(id+"F0.wireOp",EDGE,"E0.left");var subQ2=makeQuery(id+"FlHhq8AFgQTEit1_1.boolean.opBoolean","COPY",EDGE,{"derivedFrom":makeQuery(id+"FlHhq8AFgQTEit1_1.opExtrude","SWEPT_EDGE",EDGE,{"disambiguationData":[OSD([subQ1,sQuery(id+"F3.wireOp",EDGE,"E5.2.0.0"),sQuery(id+"F3.wireOp",EDGE,"E5.2.0.1")])]})});var subQ3=makeQuery(id+"F5.imprint","INTERSECT",VERTEX,{"derivedFrom":[subQ2,subQ0]});Q88=makeQuery(id+"F5.imprint","IMPRINT",FACE,{"disambiguationData":[TD([[makeQuery(id+"F5.imprint","IMPRINT",EDGE,{"disambiguationData":[TD([[subQ3,-1.0]])],"derivedFrom":subQ0}),-1.0]])]});}
            var Q89;
            {var subQ0=sQuery(id+"F5.wireOp",EDGE,"E14.left");var subQ1=sQuery(id+"F3.wireOp",EDGE,"E5.1.0.1");var subQ2=sQuery(id+"F0.wireOp",EDGE,"E0.left");var subQ3=makeQuery(id+"FlHhq8AFgQTEit1_1.boolean.opBoolean","COPY",EDGE,{"derivedFrom":makeQuery(id+"FlHhq8AFgQTEit1_1.opExtrude","SWEPT_EDGE",EDGE,{"disambiguationData":[OSD([subQ2,subQ1,sQuery(id+"F3.wireOp",EDGE,"E5.1.0.2")])]})});var subQ4=makeQuery(id+"F5.imprint","INTERSECT",VERTEX,{"derivedFrom":[subQ3,subQ0]});Q89=makeQuery(id+"F5.imprint","IMPRINT",FACE,{"disambiguationData":[TD([[makeQuery(id+"F5.imprint","IMPRINT",EDGE,{"disambiguationData":[TD([[subQ4,-1.0]])],"derivedFrom":subQ0}),-1.0]])]});}
            var Q90;
            {var subQ0=sQuery(id+"F5.wireOp",EDGE,"E21");var subQ1=sQuery(id+"F0.wireOp",EDGE,"E0.left");var subQ2=makeQuery(id+"FlHhq8AFgQTEit1_1.boolean.opBoolean","COPY",EDGE,{"derivedFrom":makeQuery(id+"FlHhq8AFgQTEit1_1.opExtrude","SWEPT_EDGE",EDGE,{"disambiguationData":[OSD([subQ1,sQuery(id+"F3.wireOp",EDGE,"E5.4.0.1"),sQuery(id+"F3.wireOp",EDGE,"E5.4.0.2")])]})});var subQ3=makeQuery(id+"F5.imprint","INTERSECT",VERTEX,{"derivedFrom":[subQ2,subQ0]});Q90=makeQuery(id+"F5.imprint","IMPRINT",FACE,{"disambiguationData":[TD([[makeQuery(id+"F5.imprint","IMPRINT",EDGE,{"disambiguationData":[TD([[subQ3,-1.0]])],"derivedFrom":subQ0}),-1.0]])]});}
            var Q91;
            {var subQ0=sQuery(id+"F5.wireOp",EDGE,"E21");var subQ1=sQuery(id+"F0.wireOp",EDGE,"E0.left");var subQ2=makeQuery(id+"FlHhq8AFgQTEit1_1.boolean.opBoolean","COPY",EDGE,{"derivedFrom":makeQuery(id+"FlHhq8AFgQTEit1_1.opExtrude","SWEPT_EDGE",EDGE,{"disambiguationData":[OSD([subQ1,sQuery(id+"F3.wireOp",EDGE,"E5.9.0.1"),sQuery(id+"F3.wireOp",EDGE,"E5.9.0.2")])]})});var subQ3=makeQuery(id+"F5.imprint","INTERSECT",VERTEX,{"derivedFrom":[subQ2,subQ0]});Q91=makeQuery(id+"F5.imprint","IMPRINT",FACE,{"disambiguationData":[TD([[makeQuery(id+"F5.imprint","IMPRINT",EDGE,{"disambiguationData":[TD([[subQ3,-1.0]])],"derivedFrom":subQ0}),-1.0]])]});}
            var Q92;
            {var subQ0=sQuery(id+"F5.wireOp",EDGE,"E21");var subQ1=sQuery(id+"F3.wireOp",EDGE,"E5.5.0.1");var subQ2=sQuery(id+"F0.wireOp",EDGE,"E0.left");var subQ3=makeQuery(id+"FlHhq8AFgQTEit1_1.boolean.opBoolean","COPY",EDGE,{"derivedFrom":makeQuery(id+"FlHhq8AFgQTEit1_1.opExtrude","SWEPT_EDGE",EDGE,{"disambiguationData":[OSD([subQ2,sQuery(id+"F3.wireOp",EDGE,"E5.5.0.0"),subQ1])]})});var subQ4=makeQuery(id+"F5.imprint","INTERSECT",VERTEX,{"derivedFrom":[subQ3,subQ0]});Q92=makeQuery(id+"F5.imprint","IMPRINT",FACE,{"disambiguationData":[TD([[makeQuery(id+"F5.imprint","IMPRINT",EDGE,{"disambiguationData":[TD([[subQ4,-1.0]])],"derivedFrom":subQ0}),-1.0]])]});}
            var Q93;
            {var subQ0=sQuery(id+"F5.wireOp",EDGE,"E21");var subQ1=sQuery(id+"F3.wireOp",EDGE,"E5.6.0.1");var subQ2=sQuery(id+"F0.wireOp",EDGE,"E0.left");var subQ3=makeQuery(id+"FlHhq8AFgQTEit1_1.boolean.opBoolean","COPY",EDGE,{"derivedFrom":makeQuery(id+"FlHhq8AFgQTEit1_1.opExtrude","SWEPT_EDGE",EDGE,{"disambiguationData":[OSD([subQ2,sQuery(id+"F3.wireOp",EDGE,"E5.6.0.0"),subQ1])]})});var subQ4=makeQuery(id+"F5.imprint","INTERSECT",VERTEX,{"derivedFrom":[subQ3,subQ0]});Q93=makeQuery(id+"F5.imprint","IMPRINT",FACE,{"disambiguationData":[TD([[makeQuery(id+"F5.imprint","IMPRINT",EDGE,{"disambiguationData":[TD([[subQ4,-1.0]])],"derivedFrom":subQ0}),-1.0]])]});}
            var Q94;
            {var subQ0=sQuery(id+"F5.wireOp",EDGE,"E21");var subQ1=makeQuery(id+"F1.opExtrude","CAP_EDGE",EDGE,{"disambiguationData":[OSD([sQuery(id+"F0.wireOp",EDGE,"E0.top")])],"isStart":true});var subQ2=makeQuery(id+"F5.imprint","INTERSECT",VERTEX,{"derivedFrom":[subQ1,subQ0]});Q94=makeQuery(id+"F5.imprint","IMPRINT",FACE,{"disambiguationData":[TD([[makeQuery(id+"F5.imprint","IMPRINT",EDGE,{"disambiguationData":[TD([[subQ2,1.0]])],"derivedFrom":subQ1}),-1.0]])]});}
            var Q95;
            {var subQ0=sQuery(id+"F5.wireOp",EDGE,"E21");var subQ1=sQuery(id+"F3.wireOp",EDGE,"E5.3.0.1");var subQ2=sQuery(id+"F0.wireOp",EDGE,"E0.left");var subQ3=makeQuery(id+"FlHhq8AFgQTEit1_1.boolean.opBoolean","COPY",EDGE,{"derivedFrom":makeQuery(id+"FlHhq8AFgQTEit1_1.opExtrude","SWEPT_EDGE",EDGE,{"disambiguationData":[OSD([subQ2,sQuery(id+"F3.wireOp",EDGE,"E5.3.0.0"),subQ1])]})});var subQ4=makeQuery(id+"F5.imprint","INTERSECT",VERTEX,{"derivedFrom":[subQ3,subQ0]});Q95=makeQuery(id+"F5.imprint","IMPRINT",FACE,{"disambiguationData":[TD([[makeQuery(id+"F5.imprint","IMPRINT",EDGE,{"disambiguationData":[TD([[subQ4,-1.0]])],"derivedFrom":subQ0}),-1.0]])]});}
            var Q96;
            {var subQ0=sQuery(id+"F5.wireOp",EDGE,"E21");var subQ1=sQuery(id+"F3.wireOp",EDGE,"E5.8.0.1");var subQ2=sQuery(id+"F0.wireOp",EDGE,"E0.left");var subQ3=makeQuery(id+"FlHhq8AFgQTEit1_1.boolean.opBoolean","COPY",EDGE,{"derivedFrom":makeQuery(id+"FlHhq8AFgQTEit1_1.opExtrude","SWEPT_EDGE",EDGE,{"disambiguationData":[OSD([subQ2,sQuery(id+"F3.wireOp",EDGE,"E5.8.0.0"),subQ1])]})});var subQ4=makeQuery(id+"F5.imprint","INTERSECT",VERTEX,{"derivedFrom":[subQ3,subQ0]});Q96=makeQuery(id+"F5.imprint","IMPRINT",FACE,{"disambiguationData":[TD([[makeQuery(id+"F5.imprint","IMPRINT",EDGE,{"disambiguationData":[TD([[subQ4,-1.0]])],"derivedFrom":subQ0}),-1.0]])]});}
            var Q97;
            {var subQ0=sQuery(id+"F5.wireOp",EDGE,"E21");var subQ1=sQuery(id+"F0.wireOp",EDGE,"E0.left");var subQ2=makeQuery(id+"FlHhq8AFgQTEit1_1.boolean.opBoolean","COPY",EDGE,{"derivedFrom":makeQuery(id+"FlHhq8AFgQTEit1_1.opExtrude","SWEPT_EDGE",EDGE,{"disambiguationData":[OSD([subQ1,sQuery(id+"F3.wireOp",EDGE,"E5.5.0.1"),sQuery(id+"F3.wireOp",EDGE,"E5.5.0.2")])]})});var subQ3=makeQuery(id+"F5.imprint","INTERSECT",VERTEX,{"derivedFrom":[subQ2,subQ0]});Q97=makeQuery(id+"F5.imprint","IMPRINT",FACE,{"disambiguationData":[TD([[makeQuery(id+"F5.imprint","IMPRINT",EDGE,{"disambiguationData":[TD([[subQ3,-1.0]])],"derivedFrom":subQ0}),-1.0]])]});}
            var Q98;
            {var subQ0=sQuery(id+"F5.wireOp",EDGE,"E21");var subQ1=sQuery(id+"F0.wireOp",EDGE,"E0.left");var subQ2=makeQuery(id+"FlHhq8AFgQTEit1_1.boolean.opBoolean","COPY",EDGE,{"derivedFrom":makeQuery(id+"FlHhq8AFgQTEit1_1.opExtrude","SWEPT_EDGE",EDGE,{"disambiguationData":[OSD([subQ1,sQuery(id+"F3.wireOp",EDGE,"E5.2.0.1"),sQuery(id+"F3.wireOp",EDGE,"E5.2.0.2")])]})});var subQ3=makeQuery(id+"F5.imprint","INTERSECT",VERTEX,{"derivedFrom":[subQ2,subQ0]});Q98=makeQuery(id+"F5.imprint","IMPRINT",FACE,{"disambiguationData":[TD([[makeQuery(id+"F5.imprint","IMPRINT",EDGE,{"disambiguationData":[TD([[subQ3,-1.0]])],"derivedFrom":subQ0}),-1.0]])]});}
            var Q99;
            {var subQ0=sQuery(id+"F5.wireOp",EDGE,"E21");var subQ1=sQuery(id+"F0.wireOp",EDGE,"E0.left");var subQ2=makeQuery(id+"FlHhq8AFgQTEit1_1.boolean.opBoolean","COPY",EDGE,{"derivedFrom":makeQuery(id+"FlHhq8AFgQTEit1_1.opExtrude","SWEPT_EDGE",EDGE,{"disambiguationData":[OSD([subQ1,sQuery(id+"F3.wireOp",EDGE,"E5.3.0.1"),sQuery(id+"F3.wireOp",EDGE,"E5.3.0.2")])]})});var subQ3=makeQuery(id+"F5.imprint","INTERSECT",VERTEX,{"derivedFrom":[subQ2,subQ0]});Q99=makeQuery(id+"F5.imprint","IMPRINT",FACE,{"disambiguationData":[TD([[makeQuery(id+"F5.imprint","IMPRINT",EDGE,{"disambiguationData":[TD([[subQ3,-1.0]])],"derivedFrom":subQ0}),-1.0]])]});}
            var Q100;
            {var subQ0=sQuery(id+"F5.wireOp",EDGE,"E21");var subQ1=sQuery(id+"F0.wireOp",EDGE,"E0.left");var subQ2=makeQuery(id+"FlHhq8AFgQTEit1_1.boolean.opBoolean","COPY",EDGE,{"derivedFrom":makeQuery(id+"FlHhq8AFgQTEit1_1.opExtrude","SWEPT_EDGE",EDGE,{"disambiguationData":[OSD([subQ1,sQuery(id+"F3.wireOp",EDGE,"E5.10.0.1"),sQuery(id+"F3.wireOp",EDGE,"E5.10.0.2")])]})});var subQ3=makeQuery(id+"F5.imprint","INTERSECT",VERTEX,{"derivedFrom":[subQ2,subQ0]});Q100=makeQuery(id+"F5.imprint","IMPRINT",FACE,{"disambiguationData":[TD([[makeQuery(id+"F5.imprint","IMPRINT",EDGE,{"disambiguationData":[TD([[subQ3,-1.0]])],"derivedFrom":subQ0}),-1.0]])]});}
            var Q101;
            {var subQ0=sQuery(id+"F5.wireOp",EDGE,"E21");var subQ1=sQuery(id+"F3.wireOp",EDGE,"E5.1.0.1");var subQ2=sQuery(id+"F0.wireOp",EDGE,"E0.left");var subQ3=makeQuery(id+"FlHhq8AFgQTEit1_1.boolean.opBoolean","COPY",EDGE,{"derivedFrom":makeQuery(id+"FlHhq8AFgQTEit1_1.opExtrude","SWEPT_EDGE",EDGE,{"disambiguationData":[OSD([subQ2,sQuery(id+"F3.wireOp",EDGE,"E5.1.0.0"),subQ1])]})});var subQ4=makeQuery(id+"F5.imprint","INTERSECT",VERTEX,{"derivedFrom":[subQ3,subQ0]});Q101=makeQuery(id+"F5.imprint","IMPRINT",FACE,{"disambiguationData":[TD([[makeQuery(id+"F5.imprint","IMPRINT",EDGE,{"disambiguationData":[TD([[subQ4,-1.0]])],"derivedFrom":subQ0}),-1.0]])]});}
            var Q102;
            {var subQ0=sQuery(id+"F5.wireOp",EDGE,"E21");var subQ1=sQuery(id+"F3.wireOp",EDGE,"E5.10.0.1");var subQ2=sQuery(id+"F0.wireOp",EDGE,"E0.left");var subQ3=makeQuery(id+"FlHhq8AFgQTEit1_1.boolean.opBoolean","COPY",EDGE,{"derivedFrom":makeQuery(id+"FlHhq8AFgQTEit1_1.opExtrude","SWEPT_EDGE",EDGE,{"disambiguationData":[OSD([subQ2,sQuery(id+"F3.wireOp",EDGE,"E5.10.0.0"),subQ1])]})});var subQ4=makeQuery(id+"F5.imprint","INTERSECT",VERTEX,{"derivedFrom":[subQ3,subQ0]});Q102=makeQuery(id+"F5.imprint","IMPRINT",FACE,{"disambiguationData":[TD([[makeQuery(id+"F5.imprint","IMPRINT",EDGE,{"disambiguationData":[TD([[subQ4,-1.0]])],"derivedFrom":subQ0}),-1.0]])]});}
            var Q103;
            {var subQ0=sQuery(id+"F5.wireOp",EDGE,"E21");var subQ1=sQuery(id+"F0.wireOp",EDGE,"E0.left");var subQ2=makeQuery(id+"FlHhq8AFgQTEit1_1.boolean.opBoolean","COPY",EDGE,{"derivedFrom":makeQuery(id+"FlHhq8AFgQTEit1_1.opExtrude","SWEPT_EDGE",EDGE,{"disambiguationData":[OSD([subQ1,sQuery(id+"F3.wireOp",EDGE,"E5.7.0.1"),sQuery(id+"F3.wireOp",EDGE,"E5.7.0.2")])]})});var subQ3=makeQuery(id+"F5.imprint","INTERSECT",VERTEX,{"derivedFrom":[subQ2,subQ0]});Q103=makeQuery(id+"F5.imprint","IMPRINT",FACE,{"disambiguationData":[TD([[makeQuery(id+"F5.imprint","IMPRINT",EDGE,{"disambiguationData":[TD([[subQ3,-1.0]])],"derivedFrom":subQ0}),-1.0]])]});}
            var Q104;
            {var subQ0=sQuery(id+"F5.wireOp",EDGE,"E21");var subQ1=sQuery(id+"F3.wireOp",EDGE,"E5.7.0.1");var subQ2=sQuery(id+"F0.wireOp",EDGE,"E0.left");var subQ3=makeQuery(id+"FlHhq8AFgQTEit1_1.boolean.opBoolean","COPY",EDGE,{"derivedFrom":makeQuery(id+"FlHhq8AFgQTEit1_1.opExtrude","SWEPT_EDGE",EDGE,{"disambiguationData":[OSD([subQ2,sQuery(id+"F3.wireOp",EDGE,"E5.7.0.0"),subQ1])]})});var subQ4=makeQuery(id+"F5.imprint","INTERSECT",VERTEX,{"derivedFrom":[subQ3,subQ0]});Q104=makeQuery(id+"F5.imprint","IMPRINT",FACE,{"disambiguationData":[TD([[makeQuery(id+"F5.imprint","IMPRINT",EDGE,{"disambiguationData":[TD([[subQ4,-1.0]])],"derivedFrom":subQ0}),-1.0]])]});}
            var Q105;
            {var subQ0=sQuery(id+"F5.wireOp",EDGE,"E21");var subQ1=sQuery(id+"F0.wireOp",EDGE,"E0.left");var subQ2=makeQuery(id+"FlHhq8AFgQTEit1_1.boolean.opBoolean","COPY",EDGE,{"derivedFrom":makeQuery(id+"FlHhq8AFgQTEit1_1.opExtrude","SWEPT_EDGE",EDGE,{"disambiguationData":[OSD([subQ1,sQuery(id+"F3.wireOp",EDGE,"E3"),sQuery(id+"F3.wireOp",EDGE,"E4")])]})});var subQ3=makeQuery(id+"F5.imprint","INTERSECT",VERTEX,{"derivedFrom":[subQ2,subQ0]});Q105=makeQuery(id+"F5.imprint","IMPRINT",FACE,{"disambiguationData":[TD([[makeQuery(id+"F5.imprint","IMPRINT",EDGE,{"disambiguationData":[TD([[subQ3,-1.0]])],"derivedFrom":subQ0}),-1.0]])]});}
            var Q106;
            {var subQ0=sQuery(id+"F5.wireOp",EDGE,"E21");var subQ1=sQuery(id+"F3.wireOp",EDGE,"E5.9.0.1");var subQ2=sQuery(id+"F0.wireOp",EDGE,"E0.left");var subQ3=makeQuery(id+"FlHhq8AFgQTEit1_1.boolean.opBoolean","COPY",EDGE,{"derivedFrom":makeQuery(id+"FlHhq8AFgQTEit1_1.opExtrude","SWEPT_EDGE",EDGE,{"disambiguationData":[OSD([subQ2,sQuery(id+"F3.wireOp",EDGE,"E5.9.0.0"),subQ1])]})});var subQ4=makeQuery(id+"F5.imprint","INTERSECT",VERTEX,{"derivedFrom":[subQ3,subQ0]});Q106=makeQuery(id+"F5.imprint","IMPRINT",FACE,{"disambiguationData":[TD([[makeQuery(id+"F5.imprint","IMPRINT",EDGE,{"disambiguationData":[TD([[subQ4,-1.0]])],"derivedFrom":subQ0}),-1.0]])]});}
            var Q107;
            {var subQ0=sQuery(id+"F5.wireOp",EDGE,"E21");var subQ1=sQuery(id+"F0.wireOp",EDGE,"E0.left");var subQ2=makeQuery(id+"FlHhq8AFgQTEit1_1.boolean.opBoolean","COPY",EDGE,{"derivedFrom":makeQuery(id+"FlHhq8AFgQTEit1_1.opExtrude","SWEPT_EDGE",EDGE,{"disambiguationData":[OSD([subQ1,sQuery(id+"F3.wireOp",EDGE,"E5.1.0.1"),sQuery(id+"F3.wireOp",EDGE,"E5.1.0.2")])]})});var subQ3=makeQuery(id+"F5.imprint","INTERSECT",VERTEX,{"derivedFrom":[subQ2,subQ0]});Q107=makeQuery(id+"F5.imprint","IMPRINT",FACE,{"disambiguationData":[TD([[makeQuery(id+"F5.imprint","IMPRINT",EDGE,{"disambiguationData":[TD([[subQ3,-1.0]])],"derivedFrom":subQ0}),-1.0]])]});}
            var Q108;
            {var subQ0=sQuery(id+"F5.wireOp",EDGE,"E21");var subQ1=sQuery(id+"F3.wireOp",EDGE,"E5.2.0.1");var subQ2=sQuery(id+"F0.wireOp",EDGE,"E0.left");var subQ3=makeQuery(id+"FlHhq8AFgQTEit1_1.boolean.opBoolean","COPY",EDGE,{"derivedFrom":makeQuery(id+"FlHhq8AFgQTEit1_1.opExtrude","SWEPT_EDGE",EDGE,{"disambiguationData":[OSD([subQ2,sQuery(id+"F3.wireOp",EDGE,"E5.2.0.0"),subQ1])]})});var subQ4=makeQuery(id+"F5.imprint","INTERSECT",VERTEX,{"derivedFrom":[subQ3,subQ0]});Q108=makeQuery(id+"F5.imprint","IMPRINT",FACE,{"disambiguationData":[TD([[makeQuery(id+"F5.imprint","IMPRINT",EDGE,{"disambiguationData":[TD([[subQ4,-1.0]])],"derivedFrom":subQ0}),-1.0]])]});}
            var Q109;
            {var subQ0=sQuery(id+"F5.wireOp",EDGE,"E21");var subQ1=sQuery(id+"F0.wireOp",EDGE,"E0.left");var subQ2=makeQuery(id+"FlHhq8AFgQTEit1_1.boolean.opBoolean","COPY",EDGE,{"derivedFrom":makeQuery(id+"FlHhq8AFgQTEit1_1.opExtrude","SWEPT_EDGE",EDGE,{"disambiguationData":[OSD([subQ1,sQuery(id+"F3.wireOp",EDGE,"E5.6.0.1"),sQuery(id+"F3.wireOp",EDGE,"E5.6.0.2")])]})});var subQ3=makeQuery(id+"F5.imprint","INTERSECT",VERTEX,{"derivedFrom":[subQ2,subQ0]});Q109=makeQuery(id+"F5.imprint","IMPRINT",FACE,{"disambiguationData":[TD([[makeQuery(id+"F5.imprint","IMPRINT",EDGE,{"disambiguationData":[TD([[subQ3,-1.0]])],"derivedFrom":subQ0}),-1.0]])]});}
            var Q110;
            {var subQ0=sQuery(id+"F5.wireOp",EDGE,"E21");var subQ1=sQuery(id+"F0.wireOp",EDGE,"E0.left");var subQ2=makeQuery(id+"FlHhq8AFgQTEit1_1.boolean.opBoolean","COPY",EDGE,{"derivedFrom":makeQuery(id+"FlHhq8AFgQTEit1_1.opExtrude","SWEPT_EDGE",EDGE,{"disambiguationData":[OSD([subQ1,sQuery(id+"F3.wireOp",EDGE,"E5.8.0.1"),sQuery(id+"F3.wireOp",EDGE,"E5.8.0.2")])]})});var subQ3=makeQuery(id+"F5.imprint","INTERSECT",VERTEX,{"derivedFrom":[subQ2,subQ0]});Q110=makeQuery(id+"F5.imprint","IMPRINT",FACE,{"disambiguationData":[TD([[makeQuery(id+"F5.imprint","IMPRINT",EDGE,{"disambiguationData":[TD([[subQ3,-1.0]])],"derivedFrom":subQ0}),-1.0]])]});}
            var Q111;
            {var subQ0=sQuery(id+"F5.wireOp",EDGE,"E21");var subQ1=sQuery(id+"F3.wireOp",EDGE,"E5.4.0.1");var subQ2=sQuery(id+"F0.wireOp",EDGE,"E0.left");var subQ3=makeQuery(id+"FlHhq8AFgQTEit1_1.boolean.opBoolean","COPY",EDGE,{"derivedFrom":makeQuery(id+"FlHhq8AFgQTEit1_1.opExtrude","SWEPT_EDGE",EDGE,{"disambiguationData":[OSD([subQ2,sQuery(id+"F3.wireOp",EDGE,"E5.4.0.0"),subQ1])]})});var subQ4=makeQuery(id+"F5.imprint","INTERSECT",VERTEX,{"derivedFrom":[subQ3,subQ0]});Q111=makeQuery(id+"F5.imprint","IMPRINT",FACE,{"disambiguationData":[TD([[makeQuery(id+"F5.imprint","IMPRINT",EDGE,{"disambiguationData":[TD([[subQ4,-1.0]])],"derivedFrom":subQ0}),-1.0]])]});}
            var Q112;
            {var subQ0=sQuery(id+"F5.wireOp",EDGE,"E21");var subQ1=sQuery(id+"F3.wireOp",EDGE,"E4");var subQ2=sQuery(id+"F0.wireOp",EDGE,"E0.left");var subQ3=makeQuery(id+"FlHhq8AFgQTEit1_1.boolean.opBoolean","COPY",EDGE,{"derivedFrom":makeQuery(id+"FlHhq8AFgQTEit1_1.opExtrude","SWEPT_EDGE",EDGE,{"disambiguationData":[OSD([subQ2,sQuery(id+"F3.wireOp",EDGE,"E2"),subQ1])]})});var subQ4=makeQuery(id+"F5.imprint","INTERSECT",VERTEX,{"derivedFrom":[subQ3,subQ0]});Q112=makeQuery(id+"F5.imprint","IMPRINT",FACE,{"disambiguationData":[TD([[makeQuery(id+"F5.imprint","IMPRINT",EDGE,{"disambiguationData":[TD([[subQ4,-1.0]])],"derivedFrom":subQ0}),-1.0]])]});}
            var Q113;
            {var subQ0=sQuery(id+"F5.wireOp",EDGE,"E21");var subQ1=sQuery(id+"F5.wireOp",EDGE,"E17.bottom");var subQ2=makeQuery(id+"F5.imprint","INTERSECT",VERTEX,{"derivedFrom":[subQ1,subQ0]});Q113=makeQuery(id+"F5.imprint","IMPRINT",FACE,{"disambiguationData":[TD([[makeQuery(id+"F5.imprint","IMPRINT",EDGE,{"disambiguationData":[TD([[subQ2,-1.0]])],"derivedFrom":subQ1}),-1.0]])]});}
            var Q114;
            {var subQ0=sQuery(id+"F5.wireOp",EDGE,"E15.left");var subQ1=sQuery(id+"F3.wireOp",EDGE,"E4");var subQ2=sQuery(id+"F0.wireOp",EDGE,"E0.left");var subQ3=makeQuery(id+"FlHhq8AFgQTEit1_1.boolean.opBoolean","COPY",EDGE,{"derivedFrom":makeQuery(id+"FlHhq8AFgQTEit1_1.opExtrude","SWEPT_EDGE",EDGE,{"disambiguationData":[OSD([subQ2,sQuery(id+"F3.wireOp",EDGE,"E2"),subQ1])]})});var subQ4=makeQuery(id+"F5.imprint","INTERSECT",VERTEX,{"derivedFrom":[subQ3,subQ0]});Q114=makeQuery(id+"F5.imprint","IMPRINT",FACE,{"disambiguationData":[TD([[makeQuery(id+"F5.imprint","IMPRINT",EDGE,{"disambiguationData":[TD([[subQ4,1.0]])],"derivedFrom":subQ0}),1.0]])]});}
            var Q115;
            {var subQ0=sQuery(id+"F5.wireOp",EDGE,"E15.left");var subQ1=sQuery(id+"F3.wireOp",EDGE,"E5.1.0.1");var subQ2=sQuery(id+"F0.wireOp",EDGE,"E0.left");var subQ3=makeQuery(id+"FlHhq8AFgQTEit1_1.boolean.opBoolean","COPY",EDGE,{"derivedFrom":makeQuery(id+"FlHhq8AFgQTEit1_1.opExtrude","SWEPT_EDGE",EDGE,{"disambiguationData":[OSD([subQ2,sQuery(id+"F3.wireOp",EDGE,"E5.1.0.0"),subQ1])]})});var subQ4=makeQuery(id+"F5.imprint","INTERSECT",VERTEX,{"derivedFrom":[subQ3,subQ0]});Q115=makeQuery(id+"F5.imprint","IMPRINT",FACE,{"disambiguationData":[TD([[makeQuery(id+"F5.imprint","IMPRINT",EDGE,{"disambiguationData":[TD([[subQ4,1.0]])],"derivedFrom":subQ0}),1.0]])]});}
            var Q116;
            {var subQ0=sQuery(id+"F5.wireOp",EDGE,"E15.left");var subQ1=sQuery(id+"F0.wireOp",EDGE,"E0.left");var subQ2=makeQuery(id+"FlHhq8AFgQTEit1_1.boolean.opBoolean","COPY",EDGE,{"derivedFrom":makeQuery(id+"FlHhq8AFgQTEit1_1.opExtrude","SWEPT_EDGE",EDGE,{"disambiguationData":[OSD([subQ1,sQuery(id+"F3.wireOp",EDGE,"E3"),sQuery(id+"F3.wireOp",EDGE,"E4")])]})});var subQ3=makeQuery(id+"F5.imprint","INTERSECT",VERTEX,{"derivedFrom":[subQ2,subQ0]});Q116=makeQuery(id+"F5.imprint","IMPRINT",FACE,{"disambiguationData":[TD([[makeQuery(id+"F5.imprint","IMPRINT",EDGE,{"disambiguationData":[TD([[subQ3,1.0]])],"derivedFrom":subQ0}),1.0]])]});}
            var Q117;
            {var subQ0=sQuery(id+"F5.wireOp",EDGE,"E15.left");var subQ1=sQuery(id+"F0.wireOp",EDGE,"E0.left");var subQ2=makeQuery(id+"FlHhq8AFgQTEit1_1.boolean.opBoolean","COPY",EDGE,{"derivedFrom":makeQuery(id+"FlHhq8AFgQTEit1_1.opExtrude","SWEPT_EDGE",EDGE,{"disambiguationData":[OSD([subQ1,sQuery(id+"F3.wireOp",EDGE,"E5.6.0.1"),sQuery(id+"F3.wireOp",EDGE,"E5.6.0.2")])]})});var subQ3=makeQuery(id+"F5.imprint","INTERSECT",VERTEX,{"derivedFrom":[subQ2,subQ0]});Q117=makeQuery(id+"F5.imprint","IMPRINT",FACE,{"disambiguationData":[TD([[makeQuery(id+"F5.imprint","IMPRINT",EDGE,{"disambiguationData":[TD([[subQ3,1.0]])],"derivedFrom":subQ0}),1.0]])]});}
            var Q118;
            {var subQ0=sQuery(id+"F5.wireOp",EDGE,"E15.left");var subQ1=sQuery(id+"F0.wireOp",EDGE,"E0.left");var subQ2=makeQuery(id+"FlHhq8AFgQTEit1_1.boolean.opBoolean","COPY",EDGE,{"derivedFrom":makeQuery(id+"FlHhq8AFgQTEit1_1.opExtrude","SWEPT_EDGE",EDGE,{"disambiguationData":[OSD([subQ1,sQuery(id+"F3.wireOp",EDGE,"E5.10.0.1"),sQuery(id+"F3.wireOp",EDGE,"E5.10.0.2")])]})});var subQ3=makeQuery(id+"F5.imprint","INTERSECT",VERTEX,{"derivedFrom":[subQ2,subQ0]});Q118=makeQuery(id+"F5.imprint","IMPRINT",FACE,{"disambiguationData":[TD([[makeQuery(id+"F5.imprint","IMPRINT",EDGE,{"disambiguationData":[TD([[subQ3,1.0]])],"derivedFrom":subQ0}),1.0]])]});}
            var Q119;
            {var subQ0=sQuery(id+"F5.wireOp",EDGE,"E15.left");var subQ1=sQuery(id+"F3.wireOp",EDGE,"E5.6.0.1");var subQ2=sQuery(id+"F0.wireOp",EDGE,"E0.left");var subQ3=makeQuery(id+"FlHhq8AFgQTEit1_1.boolean.opBoolean","COPY",EDGE,{"derivedFrom":makeQuery(id+"FlHhq8AFgQTEit1_1.opExtrude","SWEPT_EDGE",EDGE,{"disambiguationData":[OSD([subQ2,sQuery(id+"F3.wireOp",EDGE,"E5.6.0.0"),subQ1])]})});var subQ4=makeQuery(id+"F5.imprint","INTERSECT",VERTEX,{"derivedFrom":[subQ3,subQ0]});Q119=makeQuery(id+"F5.imprint","IMPRINT",FACE,{"disambiguationData":[TD([[makeQuery(id+"F5.imprint","IMPRINT",EDGE,{"disambiguationData":[TD([[subQ4,1.0]])],"derivedFrom":subQ0}),1.0]])]});}
            var Q120;
            {var subQ0=sQuery(id+"F5.wireOp",EDGE,"E15.left");var subQ1=sQuery(id+"F3.wireOp",EDGE,"E5.5.0.1");var subQ2=sQuery(id+"F0.wireOp",EDGE,"E0.left");var subQ3=makeQuery(id+"FlHhq8AFgQTEit1_1.boolean.opBoolean","COPY",EDGE,{"derivedFrom":makeQuery(id+"FlHhq8AFgQTEit1_1.opExtrude","SWEPT_EDGE",EDGE,{"disambiguationData":[OSD([subQ2,sQuery(id+"F3.wireOp",EDGE,"E5.5.0.0"),subQ1])]})});var subQ4=makeQuery(id+"F5.imprint","INTERSECT",VERTEX,{"derivedFrom":[subQ3,subQ0]});Q120=makeQuery(id+"F5.imprint","IMPRINT",FACE,{"disambiguationData":[TD([[makeQuery(id+"F5.imprint","IMPRINT",EDGE,{"disambiguationData":[TD([[subQ4,1.0]])],"derivedFrom":subQ0}),1.0]])]});}
            var Q121;
            {var subQ0=sQuery(id+"F5.wireOp",EDGE,"E15.left");var subQ1=sQuery(id+"F0.wireOp",EDGE,"E0.left");var subQ2=makeQuery(id+"FlHhq8AFgQTEit1_1.boolean.opBoolean","COPY",EDGE,{"derivedFrom":makeQuery(id+"FlHhq8AFgQTEit1_1.opExtrude","SWEPT_EDGE",EDGE,{"disambiguationData":[OSD([subQ1,sQuery(id+"F3.wireOp",EDGE,"E5.4.0.1"),sQuery(id+"F3.wireOp",EDGE,"E5.4.0.2")])]})});var subQ3=makeQuery(id+"F5.imprint","INTERSECT",VERTEX,{"derivedFrom":[subQ2,subQ0]});Q121=makeQuery(id+"F5.imprint","IMPRINT",FACE,{"disambiguationData":[TD([[makeQuery(id+"F5.imprint","IMPRINT",EDGE,{"disambiguationData":[TD([[subQ3,1.0]])],"derivedFrom":subQ0}),1.0]])]});}
            var Q122;
            {var subQ0=sQuery(id+"F5.wireOp",EDGE,"E15.top");Q122=makeQuery(id+"F5.imprint","IMPRINT",FACE,{"disambiguationData":[TD([[makeQuery(id+"F5.imprint","IMPRINT",EDGE,{"derivedFrom":subQ0}),-1.0]])]});}
            var Q123;
            {var subQ0=sQuery(id+"F5.wireOp",EDGE,"E15.left");var subQ1=sQuery(id+"F0.wireOp",EDGE,"E0.left");var subQ2=makeQuery(id+"FlHhq8AFgQTEit1_1.boolean.opBoolean","COPY",EDGE,{"derivedFrom":makeQuery(id+"FlHhq8AFgQTEit1_1.opExtrude","SWEPT_EDGE",EDGE,{"disambiguationData":[OSD([subQ1,sQuery(id+"F3.wireOp",EDGE,"E5.8.0.1"),sQuery(id+"F3.wireOp",EDGE,"E5.8.0.2")])]})});var subQ3=makeQuery(id+"F5.imprint","INTERSECT",VERTEX,{"derivedFrom":[subQ2,subQ0]});Q123=makeQuery(id+"F5.imprint","IMPRINT",FACE,{"disambiguationData":[TD([[makeQuery(id+"F5.imprint","IMPRINT",EDGE,{"disambiguationData":[TD([[subQ3,1.0]])],"derivedFrom":subQ0}),1.0]])]});}
            var Q124;
            {var subQ0=sQuery(id+"F5.wireOp",EDGE,"E15.left");var subQ1=sQuery(id+"F0.wireOp",EDGE,"E0.left");var subQ2=makeQuery(id+"FlHhq8AFgQTEit1_1.boolean.opBoolean","COPY",EDGE,{"derivedFrom":makeQuery(id+"FlHhq8AFgQTEit1_1.opExtrude","SWEPT_EDGE",EDGE,{"disambiguationData":[OSD([subQ1,sQuery(id+"F3.wireOp",EDGE,"E5.9.0.1"),sQuery(id+"F3.wireOp",EDGE,"E5.9.0.2")])]})});var subQ3=makeQuery(id+"F5.imprint","INTERSECT",VERTEX,{"derivedFrom":[subQ2,subQ0]});Q124=makeQuery(id+"F5.imprint","IMPRINT",FACE,{"disambiguationData":[TD([[makeQuery(id+"F5.imprint","IMPRINT",EDGE,{"disambiguationData":[TD([[subQ3,1.0]])],"derivedFrom":subQ0}),1.0]])]});}
            var Q125;
            {var subQ0=sQuery(id+"F5.wireOp",EDGE,"E15.left");var subQ1=sQuery(id+"F0.wireOp",EDGE,"E0.left");var subQ2=makeQuery(id+"FlHhq8AFgQTEit1_1.boolean.opBoolean","COPY",EDGE,{"derivedFrom":makeQuery(id+"FlHhq8AFgQTEit1_1.opExtrude","SWEPT_EDGE",EDGE,{"disambiguationData":[OSD([subQ1,sQuery(id+"F3.wireOp",EDGE,"E5.2.0.1"),sQuery(id+"F3.wireOp",EDGE,"E5.2.0.2")])]})});var subQ3=makeQuery(id+"F5.imprint","INTERSECT",VERTEX,{"derivedFrom":[subQ2,subQ0]});Q125=makeQuery(id+"F5.imprint","IMPRINT",FACE,{"disambiguationData":[TD([[makeQuery(id+"F5.imprint","IMPRINT",EDGE,{"disambiguationData":[TD([[subQ3,1.0]])],"derivedFrom":subQ0}),1.0]])]});}
            var Q126;
            {var subQ0=sQuery(id+"F5.wireOp",EDGE,"E15.left");var subQ1=sQuery(id+"F0.wireOp",EDGE,"E0.left");var subQ2=makeQuery(id+"FlHhq8AFgQTEit1_1.boolean.opBoolean","COPY",EDGE,{"derivedFrom":makeQuery(id+"FlHhq8AFgQTEit1_1.opExtrude","SWEPT_EDGE",EDGE,{"disambiguationData":[OSD([subQ1,sQuery(id+"F3.wireOp",EDGE,"E5.5.0.1"),sQuery(id+"F3.wireOp",EDGE,"E5.5.0.2")])]})});var subQ3=makeQuery(id+"F5.imprint","INTERSECT",VERTEX,{"derivedFrom":[subQ2,subQ0]});Q126=makeQuery(id+"F5.imprint","IMPRINT",FACE,{"disambiguationData":[TD([[makeQuery(id+"F5.imprint","IMPRINT",EDGE,{"disambiguationData":[TD([[subQ3,1.0]])],"derivedFrom":subQ0}),1.0]])]});}
            var Q127;
            {var subQ0=sQuery(id+"F5.wireOp",EDGE,"E15.left");var subQ1=sQuery(id+"F0.wireOp",EDGE,"E0.left");var subQ2=makeQuery(id+"FlHhq8AFgQTEit1_1.boolean.opBoolean","COPY",EDGE,{"derivedFrom":makeQuery(id+"FlHhq8AFgQTEit1_1.opExtrude","SWEPT_EDGE",EDGE,{"disambiguationData":[OSD([subQ1,sQuery(id+"F3.wireOp",EDGE,"E5.3.0.1"),sQuery(id+"F3.wireOp",EDGE,"E5.3.0.2")])]})});var subQ3=makeQuery(id+"F5.imprint","INTERSECT",VERTEX,{"derivedFrom":[subQ2,subQ0]});Q127=makeQuery(id+"F5.imprint","IMPRINT",FACE,{"disambiguationData":[TD([[makeQuery(id+"F5.imprint","IMPRINT",EDGE,{"disambiguationData":[TD([[subQ3,1.0]])],"derivedFrom":subQ0}),1.0]])]});}
            var Q128;
            {var subQ0=sQuery(id+"F5.wireOp",EDGE,"E15.left");var subQ1=sQuery(id+"F0.wireOp",EDGE,"E0.left");var subQ2=makeQuery(id+"FlHhq8AFgQTEit1_1.boolean.opBoolean","COPY",EDGE,{"derivedFrom":makeQuery(id+"FlHhq8AFgQTEit1_1.opExtrude","SWEPT_EDGE",EDGE,{"disambiguationData":[OSD([subQ1,sQuery(id+"F3.wireOp",EDGE,"E5.1.0.1"),sQuery(id+"F3.wireOp",EDGE,"E5.1.0.2")])]})});var subQ3=makeQuery(id+"F5.imprint","INTERSECT",VERTEX,{"derivedFrom":[subQ2,subQ0]});Q128=makeQuery(id+"F5.imprint","IMPRINT",FACE,{"disambiguationData":[TD([[makeQuery(id+"F5.imprint","IMPRINT",EDGE,{"disambiguationData":[TD([[subQ3,1.0]])],"derivedFrom":subQ0}),1.0]])]});}
            var Q129;
            {var subQ0=sQuery(id+"F5.wireOp",EDGE,"E15.left");var subQ1=sQuery(id+"F3.wireOp",EDGE,"E5.4.0.1");var subQ2=sQuery(id+"F0.wireOp",EDGE,"E0.left");var subQ3=makeQuery(id+"FlHhq8AFgQTEit1_1.boolean.opBoolean","COPY",EDGE,{"derivedFrom":makeQuery(id+"FlHhq8AFgQTEit1_1.opExtrude","SWEPT_EDGE",EDGE,{"disambiguationData":[OSD([subQ2,sQuery(id+"F3.wireOp",EDGE,"E5.4.0.0"),subQ1])]})});var subQ4=makeQuery(id+"F5.imprint","INTERSECT",VERTEX,{"derivedFrom":[subQ3,subQ0]});Q129=makeQuery(id+"F5.imprint","IMPRINT",FACE,{"disambiguationData":[TD([[makeQuery(id+"F5.imprint","IMPRINT",EDGE,{"disambiguationData":[TD([[subQ4,1.0]])],"derivedFrom":subQ0}),1.0]])]});}
            var Q130;
            {var subQ0=sQuery(id+"F5.wireOp",EDGE,"E15.left");var subQ1=sQuery(id+"F3.wireOp",EDGE,"E5.10.0.1");var subQ2=sQuery(id+"F0.wireOp",EDGE,"E0.left");var subQ3=makeQuery(id+"FlHhq8AFgQTEit1_1.boolean.opBoolean","COPY",EDGE,{"derivedFrom":makeQuery(id+"FlHhq8AFgQTEit1_1.opExtrude","SWEPT_EDGE",EDGE,{"disambiguationData":[OSD([subQ2,sQuery(id+"F3.wireOp",EDGE,"E5.10.0.0"),subQ1])]})});var subQ4=makeQuery(id+"F5.imprint","INTERSECT",VERTEX,{"derivedFrom":[subQ3,subQ0]});Q130=makeQuery(id+"F5.imprint","IMPRINT",FACE,{"disambiguationData":[TD([[makeQuery(id+"F5.imprint","IMPRINT",EDGE,{"disambiguationData":[TD([[subQ4,1.0]])],"derivedFrom":subQ0}),1.0]])]});}
            var Q131;
            {var subQ0=sQuery(id+"F5.wireOp",EDGE,"E15.left");var subQ1=sQuery(id+"F3.wireOp",EDGE,"E5.3.0.1");var subQ2=sQuery(id+"F0.wireOp",EDGE,"E0.left");var subQ3=makeQuery(id+"FlHhq8AFgQTEit1_1.boolean.opBoolean","COPY",EDGE,{"derivedFrom":makeQuery(id+"FlHhq8AFgQTEit1_1.opExtrude","SWEPT_EDGE",EDGE,{"disambiguationData":[OSD([subQ2,sQuery(id+"F3.wireOp",EDGE,"E5.3.0.0"),subQ1])]})});var subQ4=makeQuery(id+"F5.imprint","INTERSECT",VERTEX,{"derivedFrom":[subQ3,subQ0]});Q131=makeQuery(id+"F5.imprint","IMPRINT",FACE,{"disambiguationData":[TD([[makeQuery(id+"F5.imprint","IMPRINT",EDGE,{"disambiguationData":[TD([[subQ4,1.0]])],"derivedFrom":subQ0}),1.0]])]});}
            var Q132;
            {var subQ0=sQuery(id+"F5.wireOp",EDGE,"E15.left");var subQ1=sQuery(id+"F3.wireOp",EDGE,"E5.8.0.1");var subQ2=sQuery(id+"F0.wireOp",EDGE,"E0.left");var subQ3=makeQuery(id+"FlHhq8AFgQTEit1_1.boolean.opBoolean","COPY",EDGE,{"derivedFrom":makeQuery(id+"FlHhq8AFgQTEit1_1.opExtrude","SWEPT_EDGE",EDGE,{"disambiguationData":[OSD([subQ2,sQuery(id+"F3.wireOp",EDGE,"E5.8.0.0"),subQ1])]})});var subQ4=makeQuery(id+"F5.imprint","INTERSECT",VERTEX,{"derivedFrom":[subQ3,subQ0]});Q132=makeQuery(id+"F5.imprint","IMPRINT",FACE,{"disambiguationData":[TD([[makeQuery(id+"F5.imprint","IMPRINT",EDGE,{"disambiguationData":[TD([[subQ4,1.0]])],"derivedFrom":subQ0}),1.0]])]});}
            var Q133;
            {var subQ0=sQuery(id+"F5.wireOp",EDGE,"E15.left");var subQ1=sQuery(id+"F0.wireOp",EDGE,"E0.left");var subQ2=makeQuery(id+"FlHhq8AFgQTEit1_1.boolean.opBoolean","COPY",EDGE,{"derivedFrom":makeQuery(id+"FlHhq8AFgQTEit1_1.opExtrude","SWEPT_EDGE",EDGE,{"disambiguationData":[OSD([subQ1,sQuery(id+"F3.wireOp",EDGE,"E5.7.0.1"),sQuery(id+"F3.wireOp",EDGE,"E5.7.0.2")])]})});var subQ3=makeQuery(id+"F5.imprint","INTERSECT",VERTEX,{"derivedFrom":[subQ2,subQ0]});Q133=makeQuery(id+"F5.imprint","IMPRINT",FACE,{"disambiguationData":[TD([[makeQuery(id+"F5.imprint","IMPRINT",EDGE,{"disambiguationData":[TD([[subQ3,1.0]])],"derivedFrom":subQ0}),1.0]])]});}
            var Q134;
            {var subQ0=sQuery(id+"F5.wireOp",EDGE,"E15.left");var subQ1=sQuery(id+"F3.wireOp",EDGE,"E5.7.0.1");var subQ2=sQuery(id+"F0.wireOp",EDGE,"E0.left");var subQ3=makeQuery(id+"FlHhq8AFgQTEit1_1.boolean.opBoolean","COPY",EDGE,{"derivedFrom":makeQuery(id+"FlHhq8AFgQTEit1_1.opExtrude","SWEPT_EDGE",EDGE,{"disambiguationData":[OSD([subQ2,sQuery(id+"F3.wireOp",EDGE,"E5.7.0.0"),subQ1])]})});var subQ4=makeQuery(id+"F5.imprint","INTERSECT",VERTEX,{"derivedFrom":[subQ3,subQ0]});Q134=makeQuery(id+"F5.imprint","IMPRINT",FACE,{"disambiguationData":[TD([[makeQuery(id+"F5.imprint","IMPRINT",EDGE,{"disambiguationData":[TD([[subQ4,1.0]])],"derivedFrom":subQ0}),1.0]])]});}
            var Q135;
            {var subQ0=sQuery(id+"F5.wireOp",EDGE,"E15.left");var subQ1=sQuery(id+"F3.wireOp",EDGE,"E5.9.0.1");var subQ2=sQuery(id+"F0.wireOp",EDGE,"E0.left");var subQ3=makeQuery(id+"FlHhq8AFgQTEit1_1.boolean.opBoolean","COPY",EDGE,{"derivedFrom":makeQuery(id+"FlHhq8AFgQTEit1_1.opExtrude","SWEPT_EDGE",EDGE,{"disambiguationData":[OSD([subQ2,sQuery(id+"F3.wireOp",EDGE,"E5.9.0.0"),subQ1])]})});var subQ4=makeQuery(id+"F5.imprint","INTERSECT",VERTEX,{"derivedFrom":[subQ3,subQ0]});Q135=makeQuery(id+"F5.imprint","IMPRINT",FACE,{"disambiguationData":[TD([[makeQuery(id+"F5.imprint","IMPRINT",EDGE,{"disambiguationData":[TD([[subQ4,1.0]])],"derivedFrom":subQ0}),1.0]])]});}
            var Q136;
            {var subQ0=sQuery(id+"F5.wireOp",EDGE,"E15.left");var subQ1=sQuery(id+"F3.wireOp",EDGE,"E5.2.0.1");var subQ2=sQuery(id+"F0.wireOp",EDGE,"E0.left");var subQ3=makeQuery(id+"FlHhq8AFgQTEit1_1.boolean.opBoolean","COPY",EDGE,{"derivedFrom":makeQuery(id+"FlHhq8AFgQTEit1_1.opExtrude","SWEPT_EDGE",EDGE,{"disambiguationData":[OSD([subQ2,sQuery(id+"F3.wireOp",EDGE,"E5.2.0.0"),subQ1])]})});var subQ4=makeQuery(id+"F5.imprint","INTERSECT",VERTEX,{"derivedFrom":[subQ3,subQ0]});Q136=makeQuery(id+"F5.imprint","IMPRINT",FACE,{"disambiguationData":[TD([[makeQuery(id+"F5.imprint","IMPRINT",EDGE,{"disambiguationData":[TD([[subQ4,1.0]])],"derivedFrom":subQ0}),1.0]])]});}
            var Q137;
            {var subQ0=sQuery(id+"F5.wireOp",EDGE,"E15.left");var subQ3=sQuery(id+"F5.wireOp",EDGE,"E17.bottom");var subQ4=makeQuery(id+"F5.imprint","INTERSECT",VERTEX,{"derivedFrom":[subQ0,subQ3]});Q137=makeQuery(id+"F5.imprint","IMPRINT",FACE,{"disambiguationData":[TD([[makeQuery(id+"F5.imprint","IMPRINT",EDGE,{"disambiguationData":[TD([[subQ4,-1.0]])],"derivedFrom":subQ3}),-1.0]])]});}
            var Q138;
            {var subQ0=sQuery(id+"F5.wireOp",EDGE,"E14.left");var subQ1=sQuery(id+"F0.wireOp",EDGE,"E0.left");var subQ2=makeQuery(id+"FlHhq8AFgQTEit1_1.boolean.opBoolean","COPY",EDGE,{"derivedFrom":makeQuery(id+"FlHhq8AFgQTEit1_1.opExtrude","SWEPT_EDGE",EDGE,{"disambiguationData":[OSD([subQ1,sQuery(id+"F3.wireOp",EDGE,"E5.9.0.0"),sQuery(id+"F3.wireOp",EDGE,"E5.9.0.1")])]})});var subQ3=makeQuery(id+"F5.imprint","INTERSECT",VERTEX,{"derivedFrom":[subQ2,subQ0]});Q138=makeQuery(id+"F5.imprint","IMPRINT",FACE,{"disambiguationData":[TD([[makeQuery(id+"F5.imprint","IMPRINT",EDGE,{"disambiguationData":[TD([[subQ3,-1.0]])],"derivedFrom":subQ0}),-1.0]])]});}
            var Q139;
            {var subQ0=sQuery(id+"F5.wireOp",EDGE,"E14.left");var subQ8=makeQuery(id+"F5.imprint","INTERSECT",VERTEX,{"derivedFrom":[sQuery(id+"F5.wireOp",EDGE,"E12.top"),subQ0]});Q139=makeQuery(id+"F5.imprint","IMPRINT",FACE,{"disambiguationData":[TD([[makeQuery(id+"F5.imprint","IMPRINT",EDGE,{"disambiguationData":[TD([[subQ8,1.0]])],"derivedFrom":subQ0}),-1.0]])]});}
            var Q140;
            {var subQ1=sQuery(id+"F0.wireOp",EDGE,"E0.left");var subQ4=makeQuery(id+"FlHhq8AFgQTEit1_1.boolean.opBoolean","COPY",EDGE,{"derivedFrom":makeQuery(id+"FlHhq8AFgQTEit1_1.opExtrude","SWEPT_EDGE",EDGE,{"disambiguationData":[OSD([subQ1,sQuery(id+"F3.wireOp",EDGE,"E5.11.0.0"),sQuery(id+"F3.wireOp",EDGE,"E5.11.0.1")])]})});var subQ6=sQuery(id+"F5.wireOp",EDGE,"E25.trimOffspring");var subQ7=makeQuery(id+"F5.imprint","INTERSECT",VERTEX,{"derivedFrom":[subQ4,subQ6]});Q140=makeQuery(id+"F5.imprint","IMPRINT",FACE,{"disambiguationData":[TD([[makeQuery(id+"F5.imprint","IMPRINT",EDGE,{"disambiguationData":[TD([[subQ7,-1.0]])],"derivedFrom":subQ6}),1.0]])]});}
            var Q141;
            {var subQ1=sQuery(id+"F3.wireOp",EDGE,"E5.10.0.1");var subQ2=sQuery(id+"F0.wireOp",EDGE,"E0.left");var subQ3=makeQuery(id+"FlHhq8AFgQTEit1_1.boolean.opBoolean","COPY",EDGE,{"derivedFrom":makeQuery(id+"FlHhq8AFgQTEit1_1.opExtrude","SWEPT_EDGE",EDGE,{"disambiguationData":[OSD([subQ2,subQ1,sQuery(id+"F3.wireOp",EDGE,"E5.10.0.2")])]})});var subQ7=sQuery(id+"F5.wireOp",EDGE,"E25.trimOffspring");var subQ8=makeQuery(id+"F5.imprint","INTERSECT",VERTEX,{"derivedFrom":[subQ3,subQ7]});Q141=makeQuery(id+"F5.imprint","IMPRINT",FACE,{"disambiguationData":[TD([[makeQuery(id+"F5.imprint","IMPRINT",EDGE,{"disambiguationData":[TD([[subQ8,-1.0]])],"derivedFrom":subQ7}),1.0]])]});}
            var Q142;
            {var subQ0=sQuery(id+"F5.wireOp",EDGE,"E14.left");var subQ1=sQuery(id+"F3.wireOp",EDGE,"E5.9.0.1");var subQ2=sQuery(id+"F0.wireOp",EDGE,"E0.left");var subQ3=makeQuery(id+"FlHhq8AFgQTEit1_1.boolean.opBoolean","COPY",EDGE,{"derivedFrom":makeQuery(id+"FlHhq8AFgQTEit1_1.opExtrude","SWEPT_EDGE",EDGE,{"disambiguationData":[OSD([subQ2,subQ1,sQuery(id+"F3.wireOp",EDGE,"E5.9.0.2")])]})});var subQ4=makeQuery(id+"F5.imprint","INTERSECT",VERTEX,{"derivedFrom":[subQ3,subQ0]});Q142=makeQuery(id+"F5.imprint","IMPRINT",FACE,{"disambiguationData":[TD([[makeQuery(id+"F5.imprint","IMPRINT",EDGE,{"disambiguationData":[TD([[subQ4,-1.0]])],"derivedFrom":subQ0}),-1.0]])]});}
            extrude(context, id + "F12", {"entities" : qUnion([Q0, Q1, Q2, Q3, Q4, Q5, Q6, Q7, Q8, Q9, Q10, Q11, Q12, Q13, Q14, Q15, Q16, Q17, Q18, Q19, Q20, Q21, Q22, Q23, Q24, Q25, Q26, Q27, Q28, Q29, Q30, Q31, Q32, Q33, Q34, Q35, Q36, Q37, Q38, Q39, Q40, Q41, Q42, Q43, Q44, Q45, Q46, Q47, Q48, Q49, Q50, Q51, Q52, Q53, Q54, Q55, Q56, Q57, Q58, Q59, Q60, Q61, Q62, Q63, Q64, Q65, Q66, Q67, Q68, Q69, Q70, Q71, Q72, Q73, Q74, Q75, Q76, Q77, Q78, Q79, Q80, Q81, Q82, Q83, Q84, Q85, Q86, Q87, Q88, Q89, Q90, Q91, Q92, Q93, Q94, Q95, Q96, Q97, Q98, Q99, Q100, Q101, Q102, Q103, Q104, Q105, Q106, Q107, Q108, Q109, Q110, Q111, Q112, Q113, Q114, Q115, Q116, Q117, Q118, Q119, Q120, Q121, Q122, Q123, Q124, Q125, Q126, Q127, Q128, Q129, Q130, Q131, Q132, Q133, Q134, Q135, Q136, Q137, Q138, Q139, Q140, Q141, Q142]), "depth" : 304.8 * mm, "offsetDistance" : 25.4 * mm});
        }
        {
            var Q0;
            Q0=makeQuery(id+"F12.opExtrude","CAP_FACE",FACE,{"disambiguationData":[OSD([sQuery(id+"F5.wireOp",EDGE,"E16.top"),sQuery(id+"F5.wireOp",EDGE,"E16.left"),sQuery(id+"F5.wireOp",EDGE,"E18.bottom"),sQuery(id+"F5.wireOp",EDGE,"E26.trimOffspring")])],"isStart":false});
            var sketch = newSketch(context, id + "F13", { "sketchPlane" : qUnion([Q0])});
            skLineSegment(sketch, "E30.bottom", {"start": v(0, 2451.1) * mm, "end": v(1829.94, 2451.1) * mm});
            skLineSegment(sketch, "E30.top", {"start": v(0, 2413) * mm, "end": v(1829.94, 2413) * mm});
            skLineSegment(sketch, "E30.left", {"start": v(0, 2451.1) * mm, "end": v(0, 2413) * mm});
            skLineSegment(sketch, "E30.right", {"start": v(5334, 2451.1) * mm, "end": v(5334, 2413) * mm});
            skLineSegment(sketch, "E31", {"start": v(1829.94, 2451.1) * mm, "end": v(1829.94, 2413) * mm});
            skLineSegment(sketch, "E32", {"start": v(3530.44, 2413) * mm, "end": v(3530.44, 2451.1) * mm});
            skLineSegment(sketch, "E33.trimOffspring", {"start": v(3530.44, 2451.1) * mm, "end": v(5334, 2451.1) * mm});
            skLineSegment(sketch, "E34.trimOffspring", {"start": v(3530.44, 2413) * mm, "end": v(5334, 2413) * mm});
            skSolve(sketch);
        }
        {
            var Q0;
            Q0 = qSketchRegion(id + "F13", true);
            extrude(context, id + "F14", {"entities" : qUnion([Q0]), "oppositeDirection" : true, "depth" : 304.8 * mm, "offsetDistance" : 25.4 * mm});
        }
        {
            var Q0;
            Q0=makeQuery(id+"F12.opExtrude","CAP_FACE",FACE,{"disambiguationData":[OSD([sQuery(id+"F0.wireOp",EDGE,"E0.top"),sQuery(id+"F5.wireOp",EDGE,"E18.bottom"),sQuery(id+"F5.wireOp",EDGE,"E19"),sQuery(id+"F5.wireOp",EDGE,"E20")])],"isStart":false});
            var sketch = newSketch(context, id + "F15", { "sketchPlane" : qUnion([Q0])});
            skLineSegment(sketch, "E35.bottom", {"start": v(933.45, 2015.73) * mm, "end": v(1790.7, 2015.73) * mm});
            skLineSegment(sketch, "E35.top", {"start": v(933.45, 1977.63) * mm, "end": v(1790.7, 1977.63) * mm});
            skLineSegment(sketch, "E35.left", {"start": v(933.45, 2015.73) * mm, "end": v(933.45, 1977.63) * mm});
            skLineSegment(sketch, "E35.right", {"start": v(1790.7, 2015.73) * mm, "end": v(1790.7, 1977.63) * mm});
            skLineSegment(sketch, "E36.bottom", {"start": v(895.35, 2015.73) * mm, "end": v(38.1, 2015.73) * mm});
            skLineSegment(sketch, "E36.top", {"start": v(895.35, 1977.63) * mm, "end": v(38.1, 1977.63) * mm});
            skLineSegment(sketch, "E36.left", {"start": v(895.35, 2015.73) * mm, "end": v(895.35, 1977.63) * mm});
            skLineSegment(sketch, "E36.right", {"start": v(38.1, 2015.73) * mm, "end": v(38.1, 1977.63) * mm});
            skLineSegment(sketch, "E37.0.1.0", {"start": v(38.1, 1718.55) * mm, "end": v(38.1, 1680.45) * mm});
            skLineSegment(sketch, "E37.0.1.1", {"start": v(895.35, 1718.55) * mm, "end": v(895.35, 1680.45) * mm});
            skLineSegment(sketch, "E37.0.1.2", {"start": v(895.35, 1680.45) * mm, "end": v(38.1, 1680.45) * mm});
            skLineSegment(sketch, "E37.0.1.3", {"start": v(895.35, 1718.55) * mm, "end": v(38.1, 1718.55) * mm});
            skLineSegment(sketch, "E37.0.1.4", {"start": v(1790.7, 1718.55) * mm, "end": v(1790.7, 1680.45) * mm});
            skLineSegment(sketch, "E37.0.1.5", {"start": v(933.45, 1718.55) * mm, "end": v(933.45, 1680.45) * mm});
            skLineSegment(sketch, "E37.0.1.6", {"start": v(933.45, 1680.45) * mm, "end": v(1790.7, 1680.45) * mm});
            skLineSegment(sketch, "E37.0.1.7", {"start": v(933.45, 1718.55) * mm, "end": v(1790.7, 1718.55) * mm});
            skLineSegment(sketch, "E37.0.2.0", {"start": v(38.1, 1421.37) * mm, "end": v(38.1, 1383.27) * mm});
            skLineSegment(sketch, "E37.0.2.1", {"start": v(895.35, 1421.37) * mm, "end": v(895.35, 1383.27) * mm});
            skLineSegment(sketch, "E37.0.2.2", {"start": v(895.35, 1383.27) * mm, "end": v(38.1, 1383.27) * mm});
            skLineSegment(sketch, "E37.0.2.3", {"start": v(895.35, 1421.37) * mm, "end": v(38.1, 1421.37) * mm});
            skLineSegment(sketch, "E37.0.2.4", {"start": v(1790.7, 1421.37) * mm, "end": v(1790.7, 1383.27) * mm});
            skLineSegment(sketch, "E37.0.2.5", {"start": v(933.45, 1421.37) * mm, "end": v(933.45, 1383.27) * mm});
            skLineSegment(sketch, "E37.0.2.6", {"start": v(933.45, 1383.27) * mm, "end": v(1790.7, 1383.27) * mm});
            skLineSegment(sketch, "E37.0.2.7", {"start": v(933.45, 1421.37) * mm, "end": v(1790.7, 1421.37) * mm});
            skLineSegment(sketch, "E37.0.3.0", {"start": v(38.1, 1124.2) * mm, "end": v(38.1, 1086.1) * mm});
            skLineSegment(sketch, "E37.0.3.1", {"start": v(895.35, 1124.2) * mm, "end": v(895.35, 1086.1) * mm});
            skLineSegment(sketch, "E37.0.3.2", {"start": v(895.35, 1086.1) * mm, "end": v(38.1, 1086.1) * mm});
            skLineSegment(sketch, "E37.0.3.3", {"start": v(895.35, 1124.2) * mm, "end": v(38.1, 1124.2) * mm});
            skLineSegment(sketch, "E37.0.3.4", {"start": v(1790.7, 1124.2) * mm, "end": v(1790.7, 1086.1) * mm});
            skLineSegment(sketch, "E37.0.3.5", {"start": v(933.45, 1124.2) * mm, "end": v(933.45, 1086.1) * mm});
            skLineSegment(sketch, "E37.0.3.6", {"start": v(933.45, 1086.1) * mm, "end": v(1790.7, 1086.1) * mm});
            skLineSegment(sketch, "E37.0.3.7", {"start": v(933.45, 1124.2) * mm, "end": v(1790.7, 1124.2) * mm});
            skLineSegment(sketch, "E37.direction1", {"start": v(38.1, 1977.63) * mm, "end": v(63.5, 1977.63) * mm, "construction": true});
            skLineSegment(sketch, "E37.direction2", {"start": v(38.1, 1977.63) * mm, "end": v(38.1, 1680.45) * mm, "construction": true});
            skSolve(sketch);
        }
        {
            var Q0;
            Q0 = qSketchRegion(id + "F15", true);
            extrude(context, id + "F16", {"entities" : qUnion([Q0]), "oppositeDirection" : true, "depth" : 304.8 * mm, "offsetDistance" : 25.4 * mm});
        }
        {
            var Q0;
            Q0=makeQuery(id+"F12.opExtrude","CAP_FACE",FACE,{"disambiguationData":[OSD([sQuery(id+"F0.wireOp",EDGE,"E0.top"),sQuery(id+"F5.wireOp",EDGE,"E17.bottom"),sQuery(id+"F5.wireOp",EDGE,"E21"),sQuery(id+"F5.wireOp",EDGE,"E22")])],"isStart":false});
            var sketch = newSketch(context, id + "F17", { "sketchPlane" : qUnion([Q0])});
            skLineSegment(sketch, "E38.bottom", {"start": v(4451.35, 2122.83) * mm, "end": v(5295.9, 2122.83) * mm});
            skLineSegment(sketch, "E38.top", {"start": v(4451.35, 2084.73) * mm, "end": v(5295.9, 2084.73) * mm});
            skLineSegment(sketch, "E38.left", {"start": v(4451.35, 2122.83) * mm, "end": v(4451.35, 2084.73) * mm});
            skLineSegment(sketch, "E38.right", {"start": v(5295.9, 2122.83) * mm, "end": v(5295.9, 2084.73) * mm});
            skLineSegment(sketch, "E39.bottom", {"start": v(4413.25, 2122.83) * mm, "end": v(3568.7, 2122.83) * mm});
            skLineSegment(sketch, "E39.top", {"start": v(4413.25, 2084.73) * mm, "end": v(3568.7, 2084.73) * mm});
            skLineSegment(sketch, "E39.left", {"start": v(4413.25, 2122.83) * mm, "end": v(4413.25, 2084.73) * mm});
            skLineSegment(sketch, "E39.right", {"start": v(3568.7, 2122.83) * mm, "end": v(3568.7, 2084.73) * mm});
            skLineSegment(sketch, "E40.0.1.0", {"start": v(4451.35, 1792.63) * mm, "end": v(5295.9, 1792.63) * mm});
            skLineSegment(sketch, "E40.0.1.1", {"start": v(4413.25, 1792.63) * mm, "end": v(4413.25, 1754.53) * mm});
            skLineSegment(sketch, "E40.0.1.2", {"start": v(4413.25, 1754.53) * mm, "end": v(3568.7, 1754.53) * mm});
            skLineSegment(sketch, "E40.0.1.3", {"start": v(4413.25, 1792.63) * mm, "end": v(3568.7, 1792.63) * mm});
            skLineSegment(sketch, "E40.0.1.4", {"start": v(5295.9, 1792.63) * mm, "end": v(5295.9, 1754.53) * mm});
            skLineSegment(sketch, "E40.0.1.5", {"start": v(4451.35, 1792.63) * mm, "end": v(4451.35, 1754.53) * mm});
            skLineSegment(sketch, "E40.0.1.6", {"start": v(4451.35, 1754.53) * mm, "end": v(5295.9, 1754.53) * mm});
            skLineSegment(sketch, "E40.0.1.7", {"start": v(3568.7, 1792.63) * mm, "end": v(3568.7, 1754.53) * mm});
            skLineSegment(sketch, "E40.0.2.0", {"start": v(4451.35, 1462.43) * mm, "end": v(5295.9, 1462.43) * mm});
            skLineSegment(sketch, "E40.0.2.1", {"start": v(4413.25, 1462.43) * mm, "end": v(4413.25, 1424.33) * mm});
            skLineSegment(sketch, "E40.0.2.2", {"start": v(4413.25, 1424.33) * mm, "end": v(3568.7, 1424.33) * mm});
            skLineSegment(sketch, "E40.0.2.3", {"start": v(4413.25, 1462.43) * mm, "end": v(3568.7, 1462.43) * mm});
            skLineSegment(sketch, "E40.0.2.4", {"start": v(5295.9, 1462.43) * mm, "end": v(5295.9, 1424.33) * mm});
            skLineSegment(sketch, "E40.0.2.5", {"start": v(4451.35, 1462.43) * mm, "end": v(4451.35, 1424.33) * mm});
            skLineSegment(sketch, "E40.0.2.6", {"start": v(4451.35, 1424.33) * mm, "end": v(5295.9, 1424.33) * mm});
            skLineSegment(sketch, "E40.0.2.7", {"start": v(3568.7, 1462.43) * mm, "end": v(3568.7, 1424.33) * mm});
            skLineSegment(sketch, "E40.0.3.0", {"start": v(4451.35, 1132.23) * mm, "end": v(5295.9, 1132.23) * mm});
            skLineSegment(sketch, "E40.0.3.1", {"start": v(4413.25, 1132.23) * mm, "end": v(4413.25, 1094.13) * mm});
            skLineSegment(sketch, "E40.0.3.2", {"start": v(4413.25, 1094.13) * mm, "end": v(3568.7, 1094.13) * mm});
            skLineSegment(sketch, "E40.0.3.3", {"start": v(4413.25, 1132.23) * mm, "end": v(3568.7, 1132.23) * mm});
            skLineSegment(sketch, "E40.0.3.4", {"start": v(5295.9, 1132.23) * mm, "end": v(5295.9, 1094.13) * mm});
            skLineSegment(sketch, "E40.0.3.5", {"start": v(4451.35, 1132.23) * mm, "end": v(4451.35, 1094.13) * mm});
            skLineSegment(sketch, "E40.0.3.6", {"start": v(4451.35, 1094.13) * mm, "end": v(5295.9, 1094.13) * mm});
            skLineSegment(sketch, "E40.0.3.7", {"start": v(3568.7, 1132.23) * mm, "end": v(3568.7, 1094.13) * mm});
            skLineSegment(sketch, "E40.direction1", {"start": v(3568.7, 2084.73) * mm, "end": v(3594.1, 2084.73) * mm, "construction": true});
            skLineSegment(sketch, "E40.direction2", {"start": v(3568.7, 2084.73) * mm, "end": v(3568.7, 1754.53) * mm, "construction": true});
            skSolve(sketch);
        }
        {
            var Q0;
            Q0 = qSketchRegion(id + "F17", true);
            extrude(context, id + "F18", {"entities" : qUnion([Q0]), "oppositeDirection" : true, "depth" : 304.8 * mm, "offsetDistance" : 25.4 * mm});
        }
        {
            var Q0;
            Q0=makeQuery(id+"F11.opExtrude","CAP_FACE",FACE,{"disambiguationData":[OSD([sQuery(id+"F5.wireOp",EDGE,"E14.bottom"),sQuery(id+"F5.wireOp",EDGE,"E14.left"),sQuery(id+"F5.wireOp",EDGE,"E14.right"),sQuery(id+"F5.wireOp",EDGE,"E15.bottom"),sQuery(id+"F5.wireOp",EDGE,"E15.left"),sQuery(id+"F5.wireOp",EDGE,"E15.right"),sQuery(id+"F5.wireOp",EDGE,"E17.bottom"),sQuery(id+"F5.wireOp",EDGE,"E17.top"),sQuery(id+"F5.wireOp",EDGE,"E29.top"),sQuery(id+"F5.wireOp",EDGE,"E29.left"),sQuery(id+"F5.wireOp",EDGE,"E29.right")])],"isStart":false});
            var sketch = newSketch(context, id + "F19", { "sketchPlane" : qUnion([Q0])});
            skLineSegment(sketch, "E41.bottom", {"start": v(3568.7, 876.3) * mm, "end": v(3625.85, 876.3) * mm});
            skLineSegment(sketch, "E41.top", {"start": v(3568.7, 317.5) * mm, "end": v(3625.85, 317.5) * mm});
            skLineSegment(sketch, "E41.left", {"start": v(3568.7, 876.3) * mm, "end": v(3568.7, 317.5) * mm});
            skLineSegment(sketch, "E41.right", {"start": v(3625.85, 819.15) * mm, "end": v(3625.85, 374.65) * mm});
            skLineSegment(sketch, "E42.bottom", {"start": v(3568.7, 876.3) * mm, "end": v(3990.98, 876.3) * mm});
            skLineSegment(sketch, "E42.top", {"start": v(3625.85, 819.15) * mm, "end": v(3990.98, 819.15) * mm});
            skLineSegment(sketch, "E42.left", {"start": v(3568.7, 876.3) * mm, "end": v(3568.7, 819.15) * mm});
            skLineSegment(sketch, "E42.right", {"start": v(3990.98, 876.3) * mm, "end": v(3990.98, 819.15) * mm});
            skLineSegment(sketch, "E43.bottom", {"start": v(3990.98, 876.3) * mm, "end": v(3933.83, 876.3) * mm});
            skLineSegment(sketch, "E43.top", {"start": v(3990.98, 317.5) * mm, "end": v(3933.83, 317.5) * mm});
            skLineSegment(sketch, "E43.left", {"start": v(3990.98, 876.3) * mm, "end": v(3990.98, 317.5) * mm});
            skLineSegment(sketch, "E43.right", {"start": v(3933.83, 819.15) * mm, "end": v(3933.83, 374.65) * mm});
            skLineSegment(sketch, "E44.bottom", {"start": v(3990.98, 317.5) * mm, "end": v(3568.7, 317.5) * mm});
            skLineSegment(sketch, "E44.top", {"start": v(3933.83, 374.65) * mm, "end": v(3625.85, 374.65) * mm});
            skLineSegment(sketch, "E44.left", {"start": v(3990.98, 317.5) * mm, "end": v(3990.98, 374.65) * mm});
            skLineSegment(sketch, "E44.right", {"start": v(3568.7, 317.5) * mm, "end": v(3568.7, 374.65) * mm});
            skLineSegment(sketch, "E45.bottom", {"start": v(4454.52, 875.2) * mm, "end": v(4511.67, 875.2) * mm});
            skLineSegment(sketch, "E45.top", {"start": v(4454.52, 316.4) * mm, "end": v(4511.67, 316.4) * mm});
            skLineSegment(sketch, "E45.left", {"start": v(4454.52, 875.2) * mm, "end": v(4454.52, 316.4) * mm});
            skLineSegment(sketch, "E45.right", {"start": v(4511.67, 818.06) * mm, "end": v(4511.67, 373.56) * mm});
            skLineSegment(sketch, "E46.bottom", {"start": v(4454.52, 875.2) * mm, "end": v(4876.8, 875.2) * mm});
            skLineSegment(sketch, "E46.top", {"start": v(4511.67, 818.06) * mm, "end": v(4876.8, 818.06) * mm});
            skLineSegment(sketch, "E46.left", {"start": v(4454.52, 875.2) * mm, "end": v(4454.52, 818.06) * mm});
            skLineSegment(sketch, "E46.right", {"start": v(4876.8, 875.2) * mm, "end": v(4876.8, 818.06) * mm});
            skLineSegment(sketch, "E47.bottom", {"start": v(4876.8, 875.2) * mm, "end": v(4819.65, 875.2) * mm});
            skLineSegment(sketch, "E47.top", {"start": v(4876.8, 316.4) * mm, "end": v(4819.65, 316.4) * mm});
            skLineSegment(sketch, "E47.left", {"start": v(4876.8, 875.2) * mm, "end": v(4876.8, 316.4) * mm});
            skLineSegment(sketch, "E47.right", {"start": v(4819.65, 818.06) * mm, "end": v(4819.65, 373.56) * mm});
            skLineSegment(sketch, "E48.bottom", {"start": v(4876.8, 316.4) * mm, "end": v(4454.52, 316.4) * mm});
            skLineSegment(sketch, "E48.top", {"start": v(4819.65, 373.56) * mm, "end": v(4511.67, 373.56) * mm});
            skLineSegment(sketch, "E48.left", {"start": v(4876.8, 316.4) * mm, "end": v(4876.8, 373.56) * mm});
            skLineSegment(sketch, "E48.right", {"start": v(4454.52, 316.4) * mm, "end": v(4454.52, 373.56) * mm});
            skLineSegment(sketch, "E49.1.0.0", {"start": v(4413.25, 317.5) * mm, "end": v(3990.98, 317.5) * mm});
            skLineSegment(sketch, "E49.1.0.1", {"start": v(4413.25, 876.3) * mm, "end": v(4356.1, 876.3) * mm});
            skLineSegment(sketch, "E49.1.0.2", {"start": v(4356.1, 819.15) * mm, "end": v(4356.1, 374.65) * mm});
            skLineSegment(sketch, "E49.1.0.3", {"start": v(4413.25, 876.3) * mm, "end": v(4413.25, 317.5) * mm});
            skLineSegment(sketch, "E49.1.0.4", {"start": v(4048.13, 819.15) * mm, "end": v(4413.25, 819.15) * mm});
            skLineSegment(sketch, "E49.1.0.5", {"start": v(3990.98, 876.3) * mm, "end": v(4413.25, 876.3) * mm});
            skLineSegment(sketch, "E49.1.0.6", {"start": v(4048.13, 819.15) * mm, "end": v(4048.13, 374.65) * mm});
            skLineSegment(sketch, "E49.1.0.8", {"start": v(4356.1, 374.65) * mm, "end": v(4048.13, 374.65) * mm});
            skLineSegment(sketch, "E49.1.0.9", {"start": v(4413.25, 317.5) * mm, "end": v(4356.1, 317.5) * mm});
            skLineSegment(sketch, "E49.1.0.10", {"start": v(4413.25, 876.3) * mm, "end": v(4413.25, 819.15) * mm});
            skLineSegment(sketch, "E49.1.0.12", {"start": v(3990.98, 317.5) * mm, "end": v(4048.13, 317.5) * mm});
            skLineSegment(sketch, "E49.1.0.13", {"start": v(3990.98, 876.3) * mm, "end": v(4048.13, 876.3) * mm});
            skLineSegment(sketch, "E49.1.0.15", {"start": v(4413.25, 317.5) * mm, "end": v(4413.25, 374.65) * mm});
            skLineSegment(sketch, "E49.1.0.16", {"start": v(5299.07, 875.2) * mm, "end": v(5241.92, 875.2) * mm});
            skLineSegment(sketch, "E49.1.0.18", {"start": v(5299.07, 316.4) * mm, "end": v(4876.8, 316.4) * mm});
            skLineSegment(sketch, "E49.1.0.19", {"start": v(5299.07, 316.4) * mm, "end": v(5241.92, 316.4) * mm});
            skLineSegment(sketch, "E49.1.0.20", {"start": v(4933.95, 818.06) * mm, "end": v(4933.95, 373.56) * mm});
            skLineSegment(sketch, "E49.1.0.21", {"start": v(4933.95, 818.06) * mm, "end": v(5299.07, 818.06) * mm});
            skLineSegment(sketch, "E49.1.0.22", {"start": v(5299.07, 316.4) * mm, "end": v(5299.07, 373.56) * mm});
            skLineSegment(sketch, "E49.1.0.23", {"start": v(5241.92, 373.56) * mm, "end": v(4933.95, 373.56) * mm});
            skLineSegment(sketch, "E49.1.0.24", {"start": v(5299.07, 875.2) * mm, "end": v(5299.07, 316.4) * mm});
            skLineSegment(sketch, "E49.1.0.25", {"start": v(5241.92, 818.06) * mm, "end": v(5241.92, 373.56) * mm});
            skLineSegment(sketch, "E49.1.0.26", {"start": v(4876.8, 875.2) * mm, "end": v(4933.95, 875.2) * mm});
            skLineSegment(sketch, "E49.1.0.27", {"start": v(4876.8, 875.2) * mm, "end": v(5299.07, 875.2) * mm});
            skLineSegment(sketch, "E49.1.0.30", {"start": v(4876.8, 316.4) * mm, "end": v(4933.95, 316.4) * mm});
            skLineSegment(sketch, "E49.1.0.31", {"start": v(5299.07, 875.2) * mm, "end": v(5299.07, 818.06) * mm});
            skLineSegment(sketch, "E49.direction1", {"start": v(3568.7, 317.5) * mm, "end": v(3990.98, 317.5) * mm, "construction": true});
            skLineSegment(sketch, "E50.bottom", {"start": v(5299.07, 875.2) * mm, "end": v(4451.35, 875.2) * mm});
            skLineSegment(sketch, "E50.top", {"start": v(5299.07, 0) * mm, "end": v(4451.35, 0) * mm});
            skLineSegment(sketch, "E50.left", {"start": v(5299.07, 875.2) * mm, "end": v(5299.07, 0) * mm});
            skLineSegment(sketch, "E50.right", {"start": v(4451.35, 875.2) * mm, "end": v(4451.35, 0) * mm});
            skLineSegment(sketch, "E51.bottom", {"start": v(4413.25, 876.3) * mm, "end": v(3568.7, 876.3) * mm});
            skLineSegment(sketch, "E51.top", {"start": v(4413.25, 0) * mm, "end": v(3568.7, 0) * mm});
            skLineSegment(sketch, "E51.left", {"start": v(4413.25, 876.3) * mm, "end": v(4413.25, 0) * mm});
            skLineSegment(sketch, "E51.right", {"start": v(3568.7, 876.3) * mm, "end": v(3568.7, 0) * mm});
            skSolve(sketch);
        }
        {
            var Q0;
            Q0 = qSketchRegion(id + "F19", true);
            var Q1;
            {var subQ0=sQuery(id+"F19.wireOp",EDGE,"E41.right");Q1=makeQuery(id+"F19.imprint","IMPRINT",FACE,{"disambiguationData":[TD([[makeQuery(id+"F19.imprint","IMPRINT",EDGE,{"derivedFrom":subQ0}),1.0]])]});}
            var Q2;
            {var subQ0=sQuery(id+"F19.wireOp",EDGE,"E49.1.0.2");Q2=makeQuery(id+"F19.imprint","IMPRINT",FACE,{"disambiguationData":[TD([[makeQuery(id+"F19.imprint","IMPRINT",EDGE,{"derivedFrom":subQ0}),-1.0]])]});}
            var Q3;
            {var subQ0=sQuery(id+"F19.wireOp",EDGE,"E45.right");Q3=makeQuery(id+"F19.imprint","IMPRINT",FACE,{"disambiguationData":[TD([[makeQuery(id+"F19.imprint","IMPRINT",EDGE,{"derivedFrom":subQ0}),1.0]])]});}
            var Q4;
            {var subQ0=sQuery(id+"F19.wireOp",EDGE,"E49.1.0.20");Q4=makeQuery(id+"F19.imprint","IMPRINT",FACE,{"disambiguationData":[TD([[makeQuery(id+"F19.imprint","IMPRINT",EDGE,{"derivedFrom":subQ0}),1.0]])]});}
            extrude(context, id + "F20", {"entities" : qUnion([Q0, Q1, Q2, Q3, Q4]), "oppositeDirection" : true, "depth" : 19.05 * mm, "offsetDistance" : 25.4 * mm});
        }
        {
            var Q0;
            Q0=makeQuery(id+"F11.opExtrude","CAP_FACE",FACE,{"disambiguationData":[OSD([sQuery(id+"F5.wireOp",EDGE,"E13.bottom"),sQuery(id+"F5.wireOp",EDGE,"E13.left"),sQuery(id+"F5.wireOp",EDGE,"E13.right"),sQuery(id+"F5.wireOp",EDGE,"E16.bottom"),sQuery(id+"F5.wireOp",EDGE,"E16.left"),sQuery(id+"F5.wireOp",EDGE,"E16.right"),sQuery(id+"F5.wireOp",EDGE,"E18.bottom"),sQuery(id+"F5.wireOp",EDGE,"E18.top"),sQuery(id+"F5.wireOp",EDGE,"E28.top"),sQuery(id+"F5.wireOp",EDGE,"E28.left"),sQuery(id+"F5.wireOp",EDGE,"E28.right")])],"isStart":false});
            var sketch = newSketch(context, id + "F21", { "sketchPlane" : qUnion([Q0])});
            skLineSegment(sketch, "E52.bottom", {"start": v(38.1, 876.3) * mm, "end": v(466.73, 876.3) * mm});
            skLineSegment(sketch, "E52.top", {"start": v(38.1, 317.5) * mm, "end": v(466.73, 317.5) * mm});
            skLineSegment(sketch, "E52.left", {"start": v(38.1, 876.3) * mm, "end": v(38.1, 317.5) * mm});
            skLineSegment(sketch, "E52.right", {"start": v(466.73, 876.3) * mm, "end": v(466.73, 317.5) * mm});
            skLineSegment(sketch, "E53.bottom", {"start": v(95.25, 819.15) * mm, "end": v(409.58, 819.15) * mm});
            skLineSegment(sketch, "E53.top", {"start": v(95.25, 374.65) * mm, "end": v(409.58, 374.65) * mm});
            skLineSegment(sketch, "E53.left", {"start": v(95.25, 819.15) * mm, "end": v(95.25, 374.65) * mm});
            skLineSegment(sketch, "E53.right", {"start": v(409.58, 819.15) * mm, "end": v(409.58, 374.65) * mm});
            skLineSegment(sketch, "E54.bottom", {"start": v(933.73, 874.95) * mm, "end": v(1362.36, 874.95) * mm});
            skLineSegment(sketch, "E54.top", {"start": v(933.73, 316.15) * mm, "end": v(1362.36, 316.15) * mm});
            skLineSegment(sketch, "E54.left", {"start": v(933.73, 874.95) * mm, "end": v(933.73, 316.15) * mm});
            skLineSegment(sketch, "E54.right", {"start": v(1362.36, 874.95) * mm, "end": v(1362.36, 316.15) * mm});
            skLineSegment(sketch, "E55.bottom", {"start": v(990.88, 817.8) * mm, "end": v(1305.2, 817.8) * mm});
            skLineSegment(sketch, "E55.top", {"start": v(990.88, 373.3) * mm, "end": v(1305.2, 373.3) * mm});
            skLineSegment(sketch, "E55.left", {"start": v(990.88, 817.8) * mm, "end": v(990.88, 373.3) * mm});
            skLineSegment(sketch, "E55.right", {"start": v(1305.2, 817.8) * mm, "end": v(1305.2, 373.3) * mm});
            skLineSegment(sketch, "E56.1.0.0", {"start": v(466.73, 317.5) * mm, "end": v(895.35, 317.5) * mm});
            skLineSegment(sketch, "E56.1.0.1", {"start": v(466.73, 876.3) * mm, "end": v(895.35, 876.3) * mm});
            skLineSegment(sketch, "E56.1.0.2", {"start": v(838.2, 819.15) * mm, "end": v(838.2, 374.65) * mm});
            skLineSegment(sketch, "E56.1.0.3", {"start": v(523.88, 819.15) * mm, "end": v(523.88, 374.65) * mm});
            skLineSegment(sketch, "E56.1.0.4", {"start": v(523.88, 374.65) * mm, "end": v(838.2, 374.65) * mm});
            skLineSegment(sketch, "E56.1.0.5", {"start": v(523.88, 819.15) * mm, "end": v(838.2, 819.15) * mm});
            skLineSegment(sketch, "E56.1.0.6", {"start": v(895.35, 876.3) * mm, "end": v(895.35, 317.5) * mm});
            skLineSegment(sketch, "E56.1.0.8", {"start": v(1419.5, 817.8) * mm, "end": v(1733.83, 817.8) * mm});
            skLineSegment(sketch, "E56.1.0.9", {"start": v(1790.98, 874.95) * mm, "end": v(1790.98, 316.15) * mm});
            skLineSegment(sketch, "E56.1.0.10", {"start": v(1419.5, 373.3) * mm, "end": v(1733.83, 373.3) * mm});
            skLineSegment(sketch, "E56.1.0.11", {"start": v(1419.5, 817.8) * mm, "end": v(1419.5, 373.3) * mm});
            skLineSegment(sketch, "E56.1.0.12", {"start": v(1733.83, 817.8) * mm, "end": v(1733.83, 373.3) * mm});
            skLineSegment(sketch, "E56.1.0.14", {"start": v(1362.36, 316.15) * mm, "end": v(1790.98, 316.15) * mm});
            skLineSegment(sketch, "E56.1.0.15", {"start": v(1362.36, 874.95) * mm, "end": v(1790.98, 874.95) * mm});
            skLineSegment(sketch, "E56.direction1", {"start": v(38.1, 317.5) * mm, "end": v(466.73, 317.5) * mm, "construction": true});
            skLineSegment(sketch, "E57.bottom", {"start": v(1790.98, 874.95) * mm, "end": v(933.45, 874.95) * mm});
            skLineSegment(sketch, "E57.top", {"start": v(1790.98, 0) * mm, "end": v(933.45, 0) * mm});
            skLineSegment(sketch, "E57.left", {"start": v(1790.98, 874.95) * mm, "end": v(1790.98, 0) * mm});
            skLineSegment(sketch, "E57.right", {"start": v(933.45, 874.95) * mm, "end": v(933.45, 0) * mm});
            skLineSegment(sketch, "E58.bottom", {"start": v(895.35, 876.3) * mm, "end": v(38.1, 876.3) * mm});
            skLineSegment(sketch, "E58.top", {"start": v(895.35, 0) * mm, "end": v(38.1, 0) * mm});
            skLineSegment(sketch, "E58.left", {"start": v(895.35, 876.3) * mm, "end": v(895.35, 0) * mm});
            skLineSegment(sketch, "E58.right", {"start": v(38.1, 876.3) * mm, "end": v(38.1, 0) * mm});
            skSolve(sketch);
        }
        {
            var Q0;
            Q0=makeQuery(id+"F21.imprint","IMPRINT",FACE,{"disambiguationData":[TD([[makeQuery(id+"F21.imprint","IMPRINT",EDGE,{"derivedFrom":sQuery(id+"F21.wireOp",EDGE,"E52.bottom")}),-1.0]])]});
            var Q1;
            Q1=makeQuery(id+"F21.imprint","IMPRINT",FACE,{"disambiguationData":[TD([[makeQuery(id+"F21.imprint","IMPRINT",EDGE,{"derivedFrom":sQuery(id+"F21.wireOp",EDGE,"E56.1.0.0")}),1.0]])]});
            var Q2;
            Q2=makeQuery(id+"F21.imprint","IMPRINT",FACE,{"disambiguationData":[TD([[makeQuery(id+"F21.imprint","IMPRINT",EDGE,{"derivedFrom":sQuery(id+"F21.wireOp",EDGE,"E54.bottom")}),-1.0]])]});
            var Q3;
            Q3=makeQuery(id+"F21.imprint","IMPRINT",FACE,{"disambiguationData":[TD([[makeQuery(id+"F21.imprint","IMPRINT",EDGE,{"derivedFrom":sQuery(id+"F21.wireOp",EDGE,"E56.1.0.8")}),1.0]])]});
            var Q4;
            Q4=makeQuery(id+"F21.imprint","IMPRINT",FACE,{"disambiguationData":[TD([[makeQuery(id+"F21.imprint","IMPRINT",EDGE,{"derivedFrom":sQuery(id+"F21.wireOp",EDGE,"E53.bottom")}),-1.0]])]});
            var Q5;
            {var subQ0=sQuery(id+"F21.wireOp",EDGE,"E52.top");Q5=makeQuery(id+"F21.imprint","IMPRINT",FACE,{"disambiguationData":[TD([[makeQuery(id+"F21.imprint","IMPRINT",EDGE,{"derivedFrom":subQ0}),1.0]])]});}
            var Q6;
            Q6=makeQuery(id+"F21.imprint","IMPRINT",FACE,{"disambiguationData":[TD([[makeQuery(id+"F21.imprint","IMPRINT",EDGE,{"derivedFrom":sQuery(id+"F21.wireOp",EDGE,"E54.top")}),1.0]])]});
            var Q7;
            Q7=makeQuery(id+"F21.imprint","IMPRINT",FACE,{"disambiguationData":[TD([[makeQuery(id+"F21.imprint","IMPRINT",EDGE,{"derivedFrom":sQuery(id+"F21.wireOp",EDGE,"E55.bottom")}),-1.0]])]});
            var Q8;
            {var subQ3=sQuery(id+"F21.wireOp",EDGE,"E54.top");Q8=makeQuery(id+"F21.imprint","IMPRINT",FACE,{"disambiguationData":[TD([[makeQuery(id+"F21.imprint","IMPRINT",EDGE,{"derivedFrom":subQ3}),-1.0]])]});}
            var Q9;
            {var subQ3=sQuery(id+"F21.wireOp",EDGE,"E52.top");Q9=makeQuery(id+"F21.imprint","IMPRINT",FACE,{"disambiguationData":[TD([[makeQuery(id+"F21.imprint","IMPRINT",EDGE,{"derivedFrom":subQ3}),-1.0]])]});}
            var Q10;
            Q10=makeQuery(id+"F21.imprint","IMPRINT",FACE,{"disambiguationData":[TD([[makeQuery(id+"F21.imprint","IMPRINT",EDGE,{"derivedFrom":sQuery(id+"F21.wireOp",EDGE,"E56.1.0.2")}),-1.0]])]});
            var Q11;
            Q11=makeQuery(id+"F21.imprint","IMPRINT",FACE,{"disambiguationData":[TD([[makeQuery(id+"F21.imprint","IMPRINT",EDGE,{"derivedFrom":sQuery(id+"F21.wireOp",EDGE,"E56.1.0.8")}),-1.0]])]});
            extrude(context, id + "F22", {"entities" : qUnion([Q0, Q1, Q2, Q3, Q4, Q5, Q6, Q7, Q8, Q9, Q10, Q11]), "oppositeDirection" : true, "depth" : 19.05 * mm, "offsetDistance" : 25.4 * mm});
        }
    });
